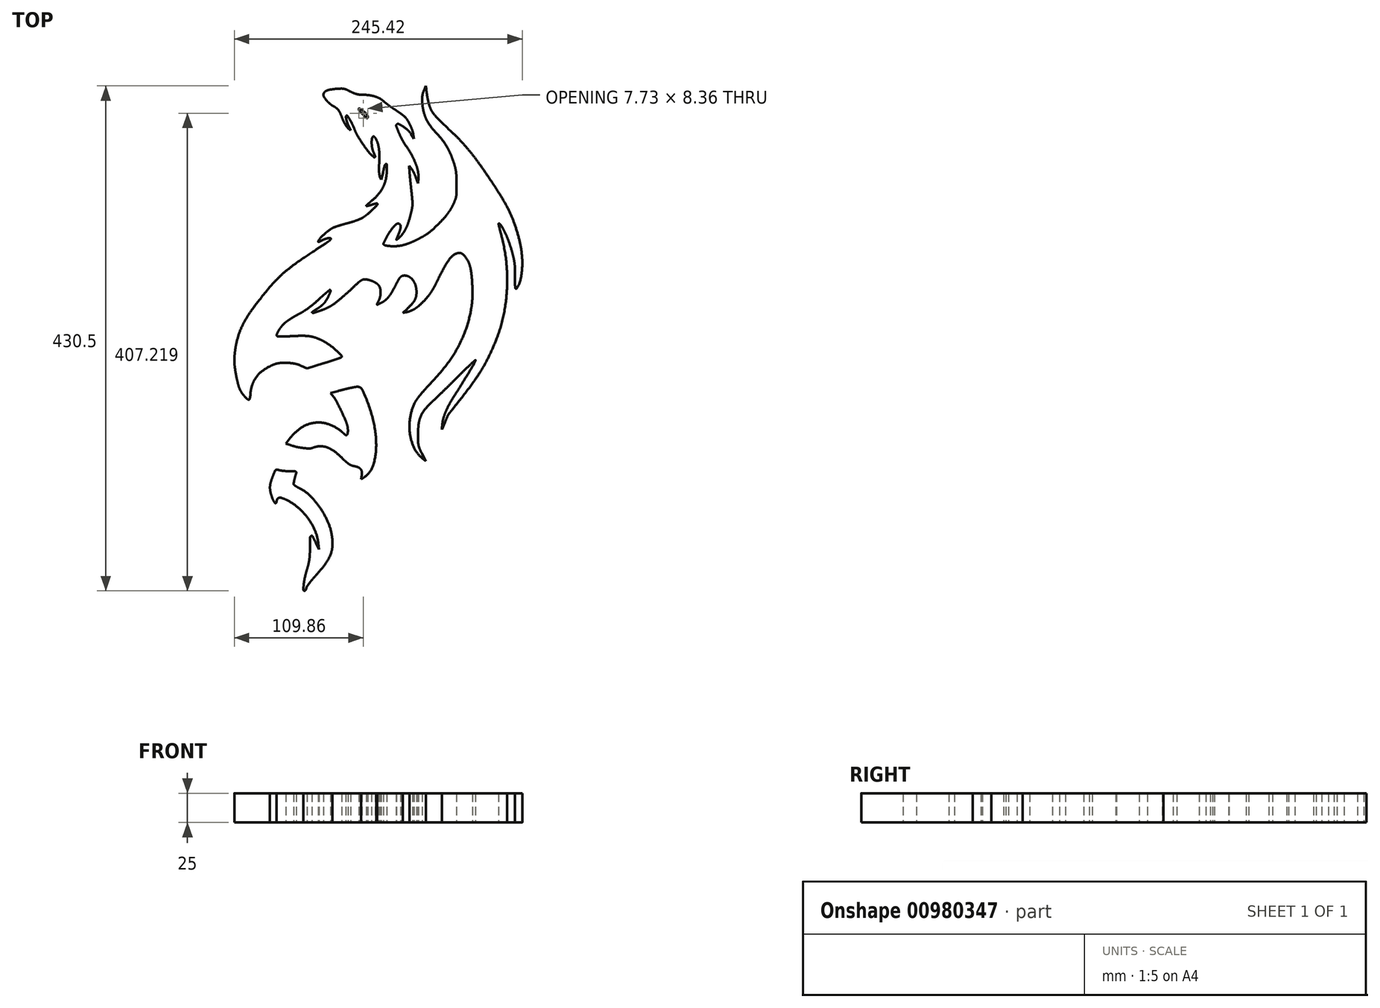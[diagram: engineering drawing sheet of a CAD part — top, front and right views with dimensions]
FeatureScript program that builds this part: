
annotation { "Feature Type Name" : "Feature", "Feature Type Description" : "" }
export const myFeature = defineFeature(function(context is Context, id is Id, definition is map)
    precondition{}
    {
        {
            var Q0;
            Q0=qCreatedBy(makeId("Top.planeOp"),FACE);
            var sketch = newSketch(context, id + "F0", { "sketchPlane" : qUnion([Q0])});
            skArc(sketch, "E0", {"start": v(-99.45, 218.84) * mm, "mid": v(-100.08, 215.3) * mm, "end": v(-100.96, 211.83) * mm});
            skArc(sketch, "E1", {"start": v(-100.96, 211.83) * mm, "mid": v(-102.01, 208.72) * mm, "end": v(-103.34, 205.71) * mm});
            skArc(sketch, "E2", {"start": v(-103.34, 205.71) * mm, "mid": v(-104.82, 203.07) * mm, "end": v(-106.56, 200.58) * mm});
            skArc(sketch, "E3", {"start": v(-106.56, 200.58) * mm, "mid": v(-108.44, 198.42) * mm, "end": v(-110.57, 196.5) * mm});
            skArc(sketch, "E4", {"start": v(-110.57, 196.5) * mm, "mid": v(-116.32, 191.62) * mm, "end": v(-121.83, 186.47) * mm});
            skArc(sketch, "E5", {"start": v(-121.83, 186.47) * mm, "mid": v(-127.23, 180.92) * mm, "end": v(-132.38, 175.14) * mm});
            skArc(sketch, "E6", {"start": v(-132.38, 175.14) * mm, "mid": v(-137.89, 168.4) * mm, "end": v(-143.13, 161.47) * mm});
            skArc(sketch, "E7", {"start": v(-143.13, 161.47) * mm, "mid": v(-149.17, 152.93) * mm, "end": v(-155.02, 144.26) * mm});
            skArc(sketch, "E8", {"start": v(-155.02, 144.26) * mm, "mid": v(-158.95, 138.2) * mm, "end": v(-162.8, 132.1) * mm});
            skArc(sketch, "E9", {"start": v(-162.8, 132.1) * mm, "mid": v(-165.38, 127.8) * mm, "end": v(-167.8, 123.4) * mm});
            skArc(sketch, "E10", {"start": v(-167.8, 123.4) * mm, "mid": v(-169.72, 119.51) * mm, "end": v(-171.47, 115.55) * mm});
            skArc(sketch, "E11", {"start": v(-171.47, 115.55) * mm, "mid": v(-173.24, 111.05) * mm, "end": v(-174.86, 106.5) * mm});
            skArc(sketch, "E12", {"start": v(-174.86, 106.5) * mm, "mid": v(-177.2, 98.78) * mm, "end": v(-179.04, 90.92) * mm});
            skArc(sketch, "E13", {"start": v(-179.04, 90.92) * mm, "mid": v(-180.15, 83.72) * mm, "end": v(-180.64, 76.45) * mm});
            skArc(sketch, "E14", {"start": v(-180.64, 76.45) * mm, "mid": v(-180.47, 70.2) * mm, "end": v(-179.66, 64) * mm});
            skArc(sketch, "E15", {"start": v(-179.66, 64) * mm, "mid": v(-178.3, 59.07) * mm, "end": v(-176.06, 54.49) * mm});
            skArc(sketch, "E16", {"start": v(-176.06, 54.49) * mm, "mid": v(-175.6, 53.86) * mm, "end": v(-175.06, 53.32) * mm});
            skArc(sketch, "E17", {"start": v(-175.06, 53.32) * mm, "mid": v(-174.72, 53.26) * mm, "end": v(-174.5, 53.53) * mm});
            skArc(sketch, "E18", {"start": v(-174.5, 53.53) * mm, "mid": v(-174.34, 54.59) * mm, "end": v(-174.29, 55.66) * mm});
            skArc(sketch, "E19", {"start": v(-174.29, 55.66) * mm, "mid": v(-174.25, 59.9) * mm, "end": v(-174.24, 64.16) * mm});
            skArc(sketch, "E20", {"start": v(-174.24, 64.16) * mm, "mid": v(-174.13, 68.8) * mm, "end": v(-173.83, 73.43) * mm});
            skArc(sketch, "E21", {"start": v(-173.83, 73.43) * mm, "mid": v(-173.35, 77.66) * mm, "end": v(-172.66, 81.86) * mm});
            skArc(sketch, "E22", {"start": v(-172.66, 81.86) * mm, "mid": v(-171.76, 85.9) * mm, "end": v(-170.64, 89.88) * mm});
            skArc(sketch, "E23", {"start": v(-170.64, 89.88) * mm, "mid": v(-169.27, 93.92) * mm, "end": v(-167.7, 97.9) * mm});
            skArc(sketch, "E24", {"start": v(-167.7, 97.9) * mm, "mid": v(-166.81, 99.86) * mm, "end": v(-165.84, 101.79) * mm});
            skArc(sketch, "E25", {"start": v(-165.84, 101.79) * mm, "mid": v(-164.65, 103.93) * mm, "end": v(-163.39, 106.04) * mm});
            skArc(sketch, "E26", {"start": v(-163.39, 106.04) * mm, "mid": v(-162.15, 108.01) * mm, "end": v(-160.9, 109.96) * mm});
            skArc(sketch, "E27", {"start": v(-160.9, 109.96) * mm, "mid": v(-160.57, 110.16) * mm, "end": v(-160.21, 110.03) * mm});
            skArc(sketch, "E28", {"start": v(-160.21, 110.03) * mm, "mid": v(-160.1, 109.86) * mm, "end": v(-160.1, 109.66) * mm});
            skArc(sketch, "E29", {"start": v(-160.1, 109.66) * mm, "mid": v(-160.37, 108.42) * mm, "end": v(-160.65, 107.19) * mm});
            skArc(sketch, "E30", {"start": v(-160.65, 107.19) * mm, "mid": v(-161, 105.74) * mm, "end": v(-161.37, 104.3) * mm});
            skArc(sketch, "E31", {"start": v(-161.37, 104.3) * mm, "mid": v(-161.83, 102.61) * mm, "end": v(-162.3, 100.94) * mm});
            skArc(sketch, "E32", {"start": v(-162.3, 100.94) * mm, "mid": v(-164.82, 90.83) * mm, "end": v(-166.55, 80.56) * mm});
            skArc(sketch, "E33", {"start": v(-166.55, 80.56) * mm, "mid": v(-167.54, 69.86) * mm, "end": v(-167.78, 59.13) * mm});
            skArc(sketch, "E34", {"start": v(-167.78, 59.13) * mm, "mid": v(-167.26, 48.52) * mm, "end": v(-166, 37.98) * mm});
            skArc(sketch, "E35", {"start": v(-166, 37.98) * mm, "mid": v(-164.03, 28.1) * mm, "end": v(-161.24, 18.42) * mm});
            skArc(sketch, "E36", {"start": v(-161.24, 18.42) * mm, "mid": v(-158.4, 10.5) * mm, "end": v(-155.21, 2.72) * mm});
            skArc(sketch, "E37", {"start": v(-155.21, 2.72) * mm, "mid": v(-151.85, -4.45) * mm, "end": v(-148.11, -11.43) * mm});
            skArc(sketch, "E38", {"start": v(-148.11, -11.43) * mm, "mid": v(-143.76, -18.65) * mm, "end": v(-139.05, -25.64) * mm});
            skArc(sketch, "E39", {"start": v(-139.05, -25.64) * mm, "mid": v(-133.15, -33.7) * mm, "end": v(-127.02, -41.57) * mm});
            skArc(sketch, "E40", {"start": v(-127.02, -41.57) * mm, "mid": v(-125.2, -43.88) * mm, "end": v(-123.4, -46.21) * mm});
            skArc(sketch, "E41", {"start": v(-123.4, -46.21) * mm, "mid": v(-121.7, -48.5) * mm, "end": v(-120.04, -50.8) * mm});
            skArc(sketch, "E42", {"start": v(-120.04, -50.8) * mm, "mid": v(-118.65, -52.78) * mm, "end": v(-117.3, -54.79) * mm});
            skArc(sketch, "E43", {"start": v(-117.3, -54.79) * mm, "mid": v(-116.62, -55.9) * mm, "end": v(-116.03, -57.07) * mm});
            skArc(sketch, "E44", {"start": v(-116.03, -57.07) * mm, "mid": v(-115.63, -57.96) * mm, "end": v(-115.23, -58.85) * mm});
            skArc(sketch, "E45", {"start": v(-115.23, -58.85) * mm, "mid": v(-114.8, -59.8) * mm, "end": v(-114.38, -60.75) * mm});
            skArc(sketch, "E46", {"start": v(-114.38, -60.75) * mm, "mid": v(-113.98, -61.62) * mm, "end": v(-113.6, -62.5) * mm});
            skArc(sketch, "E47", {"start": v(-113.6, -62.5) * mm, "mid": v(-113.31, -63.11) * mm, "end": v(-113.03, -63.74) * mm});
            skLineSegment(sketch, "E48", {"start": v(-113.03, -63.74) * mm, "end": v(-111.9, -66.24) * mm});
            skLineSegment(sketch, "E49", {"start": v(-111.9, -66.24) * mm, "end": v(-111.84, -63.6) * mm});
            skArc(sketch, "E50", {"start": v(-111.84, -63.6) * mm, "mid": v(-111.94, -61.46) * mm, "end": v(-112.34, -59.35) * mm});
            skArc(sketch, "E51", {"start": v(-112.34, -59.35) * mm, "mid": v(-113.21, -56.34) * mm, "end": v(-114.23, -53.36) * mm});
            skArc(sketch, "E52", {"start": v(-114.23, -53.36) * mm, "mid": v(-115.5, -50.13) * mm, "end": v(-116.93, -46.97) * mm});
            skArc(sketch, "E53", {"start": v(-116.93, -46.97) * mm, "mid": v(-118.42, -44.06) * mm, "end": v(-120.08, -41.24) * mm});
            skArc(sketch, "E54", {"start": v(-120.08, -41.24) * mm, "mid": v(-121.13, -39.55) * mm, "end": v(-122.19, -37.86) * mm});
            skArc(sketch, "E55", {"start": v(-122.19, -37.86) * mm, "mid": v(-123.59, -35.62) * mm, "end": v(-124.99, -33.39) * mm});
            skArc(sketch, "E56", {"start": v(-124.99, -33.39) * mm, "mid": v(-126.48, -31.01) * mm, "end": v(-127.96, -28.64) * mm});
            skArc(sketch, "E57", {"start": v(-127.96, -28.64) * mm, "mid": v(-129.31, -26.49) * mm, "end": v(-130.67, -24.34) * mm});
            skArc(sketch, "E58", {"start": v(-130.67, -24.34) * mm, "mid": v(-132.7, -21.07) * mm, "end": v(-134.7, -17.79) * mm});
            skArc(sketch, "E59", {"start": v(-134.7, -17.79) * mm, "mid": v(-136.33, -15.02) * mm, "end": v(-137.93, -12.23) * mm});
            skArc(sketch, "E60", {"start": v(-137.93, -12.23) * mm, "mid": v(-139.2, -9.95) * mm, "end": v(-140.43, -7.66) * mm});
            skArc(sketch, "E61", {"start": v(-140.43, -7.66) * mm, "mid": v(-140.69, -7) * mm, "end": v(-140.77, -6.3) * mm});
            skArc(sketch, "E62", {"start": v(-140.77, -6.3) * mm, "mid": v(-140.72, -6.23) * mm, "end": v(-140.64, -6.25) * mm});
            skArc(sketch, "E63", {"start": v(-140.64, -6.25) * mm, "mid": v(-139.25, -7.67) * mm, "end": v(-137.88, -9.1) * mm});
            skArc(sketch, "E64", {"start": v(-137.88, -9.1) * mm, "mid": v(-136.28, -10.76) * mm, "end": v(-134.7, -12.44) * mm});
            skArc(sketch, "E65", {"start": v(-134.7, -12.44) * mm, "mid": v(-132.8, -14.48) * mm, "end": v(-130.9, -16.52) * mm});
            skArc(sketch, "E66", {"start": v(-130.9, -16.52) * mm, "mid": v(-128.75, -18.83) * mm, "end": v(-126.56, -21.1) * mm});
            skArc(sketch, "E67", {"start": v(-126.56, -21.1) * mm, "mid": v(-124.1, -23.56) * mm, "end": v(-121.63, -26) * mm});
            skArc(sketch, "E68", {"start": v(-121.63, -26) * mm, "mid": v(-119.27, -28.26) * mm, "end": v(-116.89, -30.5) * mm});
            skArc(sketch, "E69", {"start": v(-116.89, -30.5) * mm, "mid": v(-115.06, -32.14) * mm, "end": v(-113.18, -33.74) * mm});
            skArc(sketch, "E70", {"start": v(-113.18, -33.74) * mm, "mid": v(-108.13, -38.06) * mm, "end": v(-103.23, -42.55) * mm});
            skArc(sketch, "E71", {"start": v(-103.23, -42.55) * mm, "mid": v(-100.1, -45.84) * mm, "end": v(-97.34, -49.44) * mm});
            skArc(sketch, "E72", {"start": v(-97.34, -49.44) * mm, "mid": v(-95.33, -52.8) * mm, "end": v(-93.78, -56.4) * mm});
            skArc(sketch, "E73", {"start": v(-93.78, -56.4) * mm, "mid": v(-92.45, -60.73) * mm, "end": v(-91.5, -65.15) * mm});
            skArc(sketch, "E74", {"start": v(-91.5, -65.15) * mm, "mid": v(-91.15, -68.11) * mm, "end": v(-91.11, -71.1) * mm});
            skArc(sketch, "E75", {"start": v(-91.11, -71.1) * mm, "mid": v(-91.37, -74.36) * mm, "end": v(-91.9, -77.6) * mm});
            skArc(sketch, "E76", {"start": v(-91.9, -77.6) * mm, "mid": v(-92.66, -80.74) * mm, "end": v(-93.68, -83.82) * mm});
            skArc(sketch, "E77", {"start": v(-93.68, -83.82) * mm, "mid": v(-94.85, -86.46) * mm, "end": v(-96.3, -88.96) * mm});
            skArc(sketch, "E78", {"start": v(-96.3, -88.96) * mm, "mid": v(-97.27, -90.48) * mm, "end": v(-98.17, -92.03) * mm});
            skArc(sketch, "E79", {"start": v(-98.17, -92.03) * mm, "mid": v(-98.14, -92.43) * mm, "end": v(-97.77, -92.59) * mm});
            skArc(sketch, "E80", {"start": v(-97.77, -92.59) * mm, "mid": v(-97, -92.33) * mm, "end": v(-96.34, -91.84) * mm});
            skArc(sketch, "E81", {"start": v(-96.34, -91.84) * mm, "mid": v(-94.67, -90.14) * mm, "end": v(-93.04, -88.4) * mm});
            skArc(sketch, "E82", {"start": v(-93.04, -88.4) * mm, "mid": v(-90.57, -85.33) * mm, "end": v(-88.55, -81.95) * mm});
            skArc(sketch, "E83", {"start": v(-88.55, -81.95) * mm, "mid": v(-86.84, -78.05) * mm, "end": v(-85.56, -74) * mm});
            skArc(sketch, "E84", {"start": v(-85.56, -74) * mm, "mid": v(-84.68, -69.61) * mm, "end": v(-84.26, -65.17) * mm});
            skArc(sketch, "E85", {"start": v(-84.26, -65.17) * mm, "mid": v(-84.3, -60.64) * mm, "end": v(-84.8, -56.14) * mm});
            skArc(sketch, "E86", {"start": v(-84.8, -56.14) * mm, "mid": v(-85.56, -52.3) * mm, "end": v(-86.64, -48.53) * mm});
            skArc(sketch, "E87", {"start": v(-86.64, -48.53) * mm, "mid": v(-87.93, -45.26) * mm, "end": v(-89.57, -42.15) * mm});
            skArc(sketch, "E88", {"start": v(-89.57, -42.15) * mm, "mid": v(-91.86, -38.67) * mm, "end": v(-94.44, -35.4) * mm});
            skArc(sketch, "E89", {"start": v(-94.44, -35.4) * mm, "mid": v(-98.54, -30.75) * mm, "end": v(-102.76, -26.21) * mm});
            skArc(sketch, "E90", {"start": v(-102.76, -26.21) * mm, "mid": v(-108.64, -19.8) * mm, "end": v(-114.24, -13.15) * mm});
            skArc(sketch, "E91", {"start": v(-114.24, -13.15) * mm, "mid": v(-118.72, -7.2) * mm, "end": v(-122.79, -0.97) * mm});
            skArc(sketch, "E92", {"start": v(-122.79, -0.97) * mm, "mid": v(-126.22, 5.19) * mm, "end": v(-129.2, 11.58) * mm});
            skArc(sketch, "E93", {"start": v(-129.2, 11.58) * mm, "mid": v(-131.93, 18.58) * mm, "end": v(-134.24, 25.73) * mm});
            skArc(sketch, "E94", {"start": v(-134.24, 25.73) * mm, "mid": v(-136.2, 33.78) * mm, "end": v(-137.48, 41.96) * mm});
            skArc(sketch, "E95", {"start": v(-137.48, 41.96) * mm, "mid": v(-138.1, 50.37) * mm, "end": v(-138.03, 58.8) * mm});
            skArc(sketch, "E96", {"start": v(-138.03, 58.8) * mm, "mid": v(-137.38, 66.14) * mm, "end": v(-136.1, 73.39) * mm});
            skArc(sketch, "E97", {"start": v(-136.1, 73.39) * mm, "mid": v(-134.41, 78) * mm, "end": v(-131.57, 81.98) * mm});
            skArc(sketch, "E98", {"start": v(-131.57, 81.98) * mm, "mid": v(-130.3, 83.09) * mm, "end": v(-128.84, 83.92) * mm});
            skArc(sketch, "E99", {"start": v(-128.84, 83.92) * mm, "mid": v(-127.47, 84.27) * mm, "end": v(-126.06, 84.16) * mm});
            skArc(sketch, "E100", {"start": v(-126.06, 84.16) * mm, "mid": v(-124.42, 83.55) * mm, "end": v(-122.95, 82.58) * mm});
            skArc(sketch, "E101", {"start": v(-122.95, 82.58) * mm, "mid": v(-120.97, 80.81) * mm, "end": v(-119.12, 78.9) * mm});
            skArc(sketch, "E102", {"start": v(-119.12, 78.9) * mm, "mid": v(-117.45, 77) * mm, "end": v(-115.85, 75.04) * mm});
            skArc(sketch, "E103", {"start": v(-115.85, 75.04) * mm, "mid": v(-114.67, 73.45) * mm, "end": v(-113.6, 71.78) * mm});
            skArc(sketch, "E104", {"start": v(-113.6, 71.78) * mm, "mid": v(-112.41, 69.67) * mm, "end": v(-111.32, 67.5) * mm});
            skArc(sketch, "E105", {"start": v(-111.32, 67.5) * mm, "mid": v(-109.38, 63.4) * mm, "end": v(-107.47, 59.26) * mm});
            skArc(sketch, "E106", {"start": v(-107.47, 59.26) * mm, "mid": v(-105.9, 56) * mm, "end": v(-104.2, 52.79) * mm});
            skArc(sketch, "E107", {"start": v(-104.2, 52.79) * mm, "mid": v(-102.63, 50.16) * mm, "end": v(-100.89, 47.64) * mm});
            skArc(sketch, "E108", {"start": v(-100.89, 47.64) * mm, "mid": v(-99.12, 45.42) * mm, "end": v(-97.2, 43.32) * mm});
            skArc(sketch, "E109", {"start": v(-97.2, 43.32) * mm, "mid": v(-95.03, 41.26) * mm, "end": v(-92.75, 39.34) * mm});
            skArc(sketch, "E110", {"start": v(-92.75, 39.34) * mm, "mid": v(-90.94, 38) * mm, "end": v(-89.03, 36.79) * mm});
            skArc(sketch, "E111", {"start": v(-89.03, 36.79) * mm, "mid": v(-87.04, 35.7) * mm, "end": v(-84.98, 34.74) * mm});
            skArc(sketch, "E112", {"start": v(-84.98, 34.74) * mm, "mid": v(-83.2, 34.04) * mm, "end": v(-81.4, 33.45) * mm});
            skArc(sketch, "E113", {"start": v(-81.4, 33.45) * mm, "mid": v(-80.57, 33.44) * mm, "end": v(-79.85, 33.85) * mm});
            skArc(sketch, "E114", {"start": v(-79.85, 33.85) * mm, "mid": v(-79.77, 34.03) * mm, "end": v(-79.82, 34.21) * mm});
            skArc(sketch, "E115", {"start": v(-79.82, 34.21) * mm, "mid": v(-80.18, 34.7) * mm, "end": v(-80.55, 35.16) * mm});
            skArc(sketch, "E116", {"start": v(-80.55, 35.16) * mm, "mid": v(-81.07, 35.75) * mm, "end": v(-81.62, 36.31) * mm});
            skArc(sketch, "E117", {"start": v(-81.62, 36.31) * mm, "mid": v(-82.3, 36.95) * mm, "end": v(-82.99, 37.57) * mm});
            skArc(sketch, "E118", {"start": v(-82.99, 37.57) * mm, "mid": v(-85.28, 39.78) * mm, "end": v(-87.34, 42.21) * mm});
            skArc(sketch, "E119", {"start": v(-87.34, 42.21) * mm, "mid": v(-88.82, 44.51) * mm, "end": v(-89.92, 47.02) * mm});
            skArc(sketch, "E120", {"start": v(-89.92, 47.02) * mm, "mid": v(-90.52, 49.45) * mm, "end": v(-90.69, 51.95) * mm});
            skArc(sketch, "E121", {"start": v(-90.69, 51.95) * mm, "mid": v(-90.4, 54.49) * mm, "end": v(-89.7, 56.95) * mm});
            skArc(sketch, "E122", {"start": v(-89.7, 56.95) * mm, "mid": v(-89, 58.56) * mm, "end": v(-88.12, 60.1) * mm});
            skArc(sketch, "E123", {"start": v(-88.12, 60.1) * mm, "mid": v(-87.2, 61.32) * mm, "end": v(-86.08, 62.4) * mm});
            skArc(sketch, "E124", {"start": v(-86.08, 62.4) * mm, "mid": v(-84.91, 63.2) * mm, "end": v(-83.63, 63.78) * mm});
            skArc(sketch, "E125", {"start": v(-83.63, 63.78) * mm, "mid": v(-82.24, 64.14) * mm, "end": v(-80.82, 64.26) * mm});
            skArc(sketch, "E126", {"start": v(-80.82, 64.26) * mm, "mid": v(-79.16, 64.15) * mm, "end": v(-77.53, 63.8) * mm});
            skArc(sketch, "E127", {"start": v(-77.53, 63.8) * mm, "mid": v(-76.14, 63.25) * mm, "end": v(-74.88, 62.45) * mm});
            skArc(sketch, "E128", {"start": v(-74.88, 62.45) * mm, "mid": v(-73.56, 61.25) * mm, "end": v(-72.42, 59.87) * mm});
            skArc(sketch, "E129", {"start": v(-72.42, 59.87) * mm, "mid": v(-70.97, 57.72) * mm, "end": v(-69.63, 55.5) * mm});
            skArc(sketch, "E130", {"start": v(-69.63, 55.5) * mm, "mid": v(-68.1, 52.98) * mm, "end": v(-66.43, 50.54) * mm});
            skArc(sketch, "E131", {"start": v(-66.43, 50.54) * mm, "mid": v(-64.59, 48.13) * mm, "end": v(-62.63, 45.8) * mm});
            skArc(sketch, "E132", {"start": v(-62.63, 45.8) * mm, "mid": v(-60.76, 43.81) * mm, "end": v(-58.8, 41.91) * mm});
            skArc(sketch, "E133", {"start": v(-58.8, 41.91) * mm, "mid": v(-57.26, 40.68) * mm, "end": v(-55.58, 39.66) * mm});
            skArc(sketch, "E134", {"start": v(-55.58, 39.66) * mm, "mid": v(-54.58, 39.18) * mm, "end": v(-53.57, 38.76) * mm});
            skArc(sketch, "E135", {"start": v(-53.57, 38.76) * mm, "mid": v(-53.2, 38.78) * mm, "end": v(-52.97, 39.06) * mm});
            skArc(sketch, "E136", {"start": v(-52.97, 39.06) * mm, "mid": v(-52.9, 39.62) * mm, "end": v(-53, 40.17) * mm});
            skArc(sketch, "E137", {"start": v(-53, 40.17) * mm, "mid": v(-53.65, 42.17) * mm, "end": v(-54.34, 44.16) * mm});
            skArc(sketch, "E138", {"start": v(-54.34, 44.16) * mm, "mid": v(-54.65, 45.16) * mm, "end": v(-54.91, 46.16) * mm});
            skArc(sketch, "E139", {"start": v(-54.91, 46.16) * mm, "mid": v(-55.12, 47.18) * mm, "end": v(-55.27, 48.2) * mm});
            skArc(sketch, "E140", {"start": v(-55.27, 48.2) * mm, "mid": v(-55.35, 49.15) * mm, "end": v(-55.38, 50.1) * mm});
            skArc(sketch, "E141", {"start": v(-55.38, 50.1) * mm, "mid": v(-55.34, 50.89) * mm, "end": v(-55.21, 51.66) * mm});
            skArc(sketch, "E142", {"start": v(-55.21, 51.66) * mm, "mid": v(-54.32, 54.66) * mm, "end": v(-52.96, 57.47) * mm});
            skArc(sketch, "E143", {"start": v(-52.96, 57.47) * mm, "mid": v(-51.3, 59.62) * mm, "end": v(-49.18, 61.3) * mm});
            skArc(sketch, "E144", {"start": v(-49.18, 61.3) * mm, "mid": v(-46.7, 62.44) * mm, "end": v(-44, 62.94) * mm});
            skArc(sketch, "E145", {"start": v(-44, 62.94) * mm, "mid": v(-40.84, 62.89) * mm, "end": v(-37.72, 62.34) * mm});
            skLineSegment(sketch, "E146", {"start": v(-37.72, 62.34) * mm, "end": v(-32.77, 61.08) * mm});
            skLineSegment(sketch, "E147", {"start": v(-32.77, 61.08) * mm, "end": v(-25.7, 67.63) * mm});
            skArc(sketch, "E148", {"start": v(-25.7, 67.63) * mm, "mid": v(-24.05, 69.11) * mm, "end": v(-22.36, 70.56) * mm});
            skArc(sketch, "E149", {"start": v(-22.36, 70.56) * mm, "mid": v(-20.27, 72.27) * mm, "end": v(-18.15, 73.95) * mm});
            skArc(sketch, "E150", {"start": v(-18.15, 73.95) * mm, "mid": v(-15.98, 75.63) * mm, "end": v(-13.78, 77.27) * mm});
            skArc(sketch, "E151", {"start": v(-13.78, 77.27) * mm, "mid": v(-11.88, 78.64) * mm, "end": v(-9.95, 79.96) * mm});
            skArc(sketch, "E152", {"start": v(-9.95, 79.96) * mm, "mid": v(-8.27, 81.08) * mm, "end": v(-6.59, 82.2) * mm});
            skArc(sketch, "E153", {"start": v(-6.59, 82.2) * mm, "mid": v(-5.13, 83.17) * mm, "end": v(-3.67, 84.15) * mm});
            skArc(sketch, "E154", {"start": v(-3.67, 84.15) * mm, "mid": v(-2.42, 84.99) * mm, "end": v(-1.16, 85.83) * mm});
            skArc(sketch, "E155", {"start": v(-1.16, 85.83) * mm, "mid": v(-0.96, 85.96) * mm, "end": v(-0.77, 86.1) * mm});
            skArc(sketch, "E156", {"start": v(-0.77, 86.1) * mm, "mid": v(-0.7, 86.24) * mm, "end": v(-0.74, 86.4) * mm});
            skArc(sketch, "E157", {"start": v(-0.74, 86.4) * mm, "mid": v(-1.36, 87.1) * mm, "end": v(-2, 87.8) * mm});
            skArc(sketch, "E158", {"start": v(-2, 87.8) * mm, "mid": v(-2.8, 88.65) * mm, "end": v(-3.61, 89.47) * mm});
            skArc(sketch, "E159", {"start": v(-3.61, 89.47) * mm, "mid": v(-4.62, 90.44) * mm, "end": v(-5.63, 91.4) * mm});
            skArc(sketch, "E160", {"start": v(-5.63, 91.4) * mm, "mid": v(-7.1, 92.67) * mm, "end": v(-8.62, 93.85) * mm});
            skArc(sketch, "E161", {"start": v(-8.62, 93.85) * mm, "mid": v(-10.45, 95.14) * mm, "end": v(-12.33, 96.35) * mm});
            skArc(sketch, "E162", {"start": v(-12.33, 96.35) * mm, "mid": v(-14.48, 97.64) * mm, "end": v(-16.68, 98.86) * mm});
            skArc(sketch, "E163", {"start": v(-16.68, 98.86) * mm, "mid": v(-19.14, 100.14) * mm, "end": v(-21.63, 101.35) * mm});
            skArc(sketch, "E164", {"start": v(-21.63, 101.35) * mm, "mid": v(-28.13, 104.44) * mm, "end": v(-34.6, 107.57) * mm});
            skArc(sketch, "E165", {"start": v(-34.6, 107.57) * mm, "mid": v(-37.72, 109.18) * mm, "end": v(-40.78, 110.91) * mm});
            skArc(sketch, "E166", {"start": v(-40.78, 110.91) * mm, "mid": v(-43.03, 112.37) * mm, "end": v(-45.16, 113.99) * mm});
            skArc(sketch, "E167", {"start": v(-45.16, 113.99) * mm, "mid": v(-47.63, 116.1) * mm, "end": v(-50.01, 118.3) * mm});
            skArc(sketch, "E168", {"start": v(-50.01, 118.3) * mm, "mid": v(-52.33, 120.59) * mm, "end": v(-54.6, 122.92) * mm});
            skArc(sketch, "E169", {"start": v(-54.6, 122.92) * mm, "mid": v(-55.63, 124.15) * mm, "end": v(-56.47, 125.52) * mm});
            skArc(sketch, "E170", {"start": v(-56.47, 125.52) * mm, "mid": v(-56.48, 126.07) * mm, "end": v(-56.05, 126.4) * mm});
            skArc(sketch, "E171", {"start": v(-56.05, 126.4) * mm, "mid": v(-55.12, 126.45) * mm, "end": v(-54.2, 126.24) * mm});
            skArc(sketch, "E172", {"start": v(-54.2, 126.24) * mm, "mid": v(-53.64, 126.04) * mm, "end": v(-53.07, 125.87) * mm});
            skArc(sketch, "E173", {"start": v(-53.07, 125.87) * mm, "mid": v(-52.41, 125.7) * mm, "end": v(-51.76, 125.56) * mm});
            skArc(sketch, "E174", {"start": v(-51.76, 125.56) * mm, "mid": v(-51.12, 125.45) * mm, "end": v(-50.48, 125.36) * mm});
            skArc(sketch, "E175", {"start": v(-50.48, 125.36) * mm, "mid": v(-49.97, 125.32) * mm, "end": v(-49.46, 125.31) * mm});
            skArc(sketch, "E176", {"start": v(-49.46, 125.31) * mm, "mid": v(-48.76, 125.34) * mm, "end": v(-48.07, 125.38) * mm});
            skArc(sketch, "E177", {"start": v(-48.07, 125.38) * mm, "mid": v(-47.94, 125.44) * mm, "end": v(-47.9, 125.59) * mm});
            skArc(sketch, "E178", {"start": v(-47.9, 125.59) * mm, "mid": v(-47.98, 125.77) * mm, "end": v(-48.12, 125.9) * mm});
            skArc(sketch, "E179", {"start": v(-48.12, 125.9) * mm, "mid": v(-48.94, 126.48) * mm, "end": v(-49.77, 127.04) * mm});
            skArc(sketch, "E180", {"start": v(-49.77, 127.04) * mm, "mid": v(-53.46, 129.9) * mm, "end": v(-56.7, 133.26) * mm});
            skArc(sketch, "E181", {"start": v(-56.7, 133.26) * mm, "mid": v(-59.6, 137.2) * mm, "end": v(-62, 141.48) * mm});
            skArc(sketch, "E182", {"start": v(-62, 141.48) * mm, "mid": v(-63.76, 145.8) * mm, "end": v(-64.94, 150.31) * mm});
            skArc(sketch, "E183", {"start": v(-64.94, 150.31) * mm, "mid": v(-65.3, 154.31) * mm, "end": v(-64.87, 158.31) * mm});
            skLineSegment(sketch, "E184", {"start": v(-64.87, 158.31) * mm, "end": v(-64.14, 161.76) * mm});
            skLineSegment(sketch, "E185", {"start": v(-64.14, 161.76) * mm, "end": v(-63, 156.76) * mm});
            skArc(sketch, "E186", {"start": v(-63, 156.76) * mm, "mid": v(-62.76, 155.68) * mm, "end": v(-62.52, 154.6) * mm});
            skArc(sketch, "E187", {"start": v(-62.52, 154.6) * mm, "mid": v(-62.25, 153.4) * mm, "end": v(-62, 152.2) * mm});
            skArc(sketch, "E188", {"start": v(-62, 152.2) * mm, "mid": v(-61.75, 151.08) * mm, "end": v(-61.5, 149.95) * mm});
            skArc(sketch, "E189", {"start": v(-61.5, 149.95) * mm, "mid": v(-61.33, 149.1) * mm, "end": v(-61.15, 148.26) * mm});
            skArc(sketch, "E190", {"start": v(-61.15, 148.26) * mm, "mid": v(-60.91, 147.1) * mm, "end": v(-60.66, 145.95) * mm});
            skArc(sketch, "E191", {"start": v(-60.66, 145.95) * mm, "mid": v(-60.58, 145.76) * mm, "end": v(-60.43, 145.6) * mm});
            skArc(sketch, "E192", {"start": v(-60.43, 145.6) * mm, "mid": v(-60.3, 145.59) * mm, "end": v(-60.2, 145.69) * mm});
            skArc(sketch, "E193", {"start": v(-60.2, 145.69) * mm, "mid": v(-59.94, 146.47) * mm, "end": v(-59.7, 147.26) * mm});
            skArc(sketch, "E194", {"start": v(-59.7, 147.26) * mm, "mid": v(-59.52, 148.05) * mm, "end": v(-59.41, 148.85) * mm});
            skArc(sketch, "E195", {"start": v(-59.41, 148.85) * mm, "mid": v(-59.27, 150.7) * mm, "end": v(-59.15, 152.55) * mm});
            skArc(sketch, "E196", {"start": v(-59.15, 152.55) * mm, "mid": v(-59.03, 154.77) * mm, "end": v(-58.94, 156.98) * mm});
            skArc(sketch, "E197", {"start": v(-58.94, 156.98) * mm, "mid": v(-58.87, 159.37) * mm, "end": v(-58.83, 161.76) * mm});
            skArc(sketch, "E198", {"start": v(-58.83, 161.76) * mm, "mid": v(-58.7, 165.95) * mm, "end": v(-58.42, 170.14) * mm});
            skArc(sketch, "E199", {"start": v(-58.42, 170.14) * mm, "mid": v(-58.02, 173.63) * mm, "end": v(-57.4, 177.1) * mm});
            skArc(sketch, "E200", {"start": v(-57.4, 177.1) * mm, "mid": v(-56.76, 179.7) * mm, "end": v(-55.95, 182.24) * mm});
            skArc(sketch, "E201", {"start": v(-55.95, 182.24) * mm, "mid": v(-55.25, 183.33) * mm, "end": v(-54.14, 183.99) * mm});
            skArc(sketch, "E202", {"start": v(-54.14, 183.99) * mm, "mid": v(-53.53, 183.94) * mm, "end": v(-53.12, 183.48) * mm});
            skArc(sketch, "E203", {"start": v(-53.12, 183.48) * mm, "mid": v(-52.68, 182.08) * mm, "end": v(-52.35, 180.64) * mm});
            skArc(sketch, "E204", {"start": v(-52.35, 180.64) * mm, "mid": v(-52.11, 178.88) * mm, "end": v(-52.02, 177.1) * mm});
            skArc(sketch, "E205", {"start": v(-52.02, 177.1) * mm, "mid": v(-52.09, 175.5) * mm, "end": v(-52.33, 173.93) * mm});
            skArc(sketch, "E206", {"start": v(-52.33, 173.93) * mm, "mid": v(-52.5, 173.22) * mm, "end": v(-52.7, 172.52) * mm});
            skArc(sketch, "E207", {"start": v(-52.7, 172.52) * mm, "mid": v(-52.95, 171.7) * mm, "end": v(-53.23, 170.88) * mm});
            skArc(sketch, "E208", {"start": v(-53.23, 170.88) * mm, "mid": v(-53.52, 170.09) * mm, "end": v(-53.83, 169.3) * mm});
            skArc(sketch, "E209", {"start": v(-53.83, 169.3) * mm, "mid": v(-54.11, 168.65) * mm, "end": v(-54.42, 168.01) * mm});
            skArc(sketch, "E210", {"start": v(-54.42, 168.01) * mm, "mid": v(-54.67, 167.5) * mm, "end": v(-54.9, 166.96) * mm});
            skArc(sketch, "E211", {"start": v(-54.9, 166.96) * mm, "mid": v(-55.05, 166.52) * mm, "end": v(-55.17, 166.07) * mm});
            skArc(sketch, "E212", {"start": v(-55.17, 166.07) * mm, "mid": v(-55.21, 165.77) * mm, "end": v(-55.21, 165.46) * mm});
            skArc(sketch, "E213", {"start": v(-55.21, 165.46) * mm, "mid": v(-55.14, 165.32) * mm, "end": v(-55, 165.26) * mm});
            skArc(sketch, "E214", {"start": v(-55, 165.26) * mm, "mid": v(-53.4, 165.64) * mm, "end": v(-52.15, 166.7) * mm});
            skArc(sketch, "E215", {"start": v(-52.15, 166.7) * mm, "mid": v(-48.82, 171.3) * mm, "end": v(-45.58, 175.98) * mm});
            skArc(sketch, "E216", {"start": v(-45.58, 175.98) * mm, "mid": v(-42.49, 180.73) * mm, "end": v(-39.56, 185.58) * mm});
            skArc(sketch, "E217", {"start": v(-39.56, 185.58) * mm, "mid": v(-37.89, 188.91) * mm, "end": v(-36.6, 192.42) * mm});
            skArc(sketch, "E218", {"start": v(-36.6, 192.42) * mm, "mid": v(-36.32, 193.27) * mm, "end": v(-35.97, 194.1) * mm});
            skArc(sketch, "E219", {"start": v(-35.97, 194.1) * mm, "mid": v(-35.48, 195.09) * mm, "end": v(-34.96, 196.05) * mm});
            skArc(sketch, "E220", {"start": v(-34.96, 196.05) * mm, "mid": v(-34.38, 197) * mm, "end": v(-33.77, 197.94) * mm});
            skArc(sketch, "E221", {"start": v(-33.77, 197.94) * mm, "mid": v(-33.2, 198.73) * mm, "end": v(-32.57, 199.48) * mm});
            skLineSegment(sketch, "E222", {"start": v(-32.57, 199.48) * mm, "end": v(-29.67, 202.76) * mm});
            skLineSegment(sketch, "E223", {"start": v(-29.67, 202.76) * mm, "end": v(-30.3, 197.9) * mm});
            skArc(sketch, "E224", {"start": v(-30.3, 197.9) * mm, "mid": v(-30.5, 196.05) * mm, "end": v(-30.6, 194.18) * mm});
            skArc(sketch, "E225", {"start": v(-30.6, 194.18) * mm, "mid": v(-30.39, 193.78) * mm, "end": v(-29.93, 193.8) * mm});
            skArc(sketch, "E226", {"start": v(-29.93, 193.8) * mm, "mid": v(-29.25, 194.42) * mm, "end": v(-28.77, 195.21) * mm});
            skArc(sketch, "E227", {"start": v(-28.77, 195.21) * mm, "mid": v(-27.75, 197.74) * mm, "end": v(-26.77, 200.27) * mm});
            skArc(sketch, "E228", {"start": v(-26.77, 200.27) * mm, "mid": v(-25.97, 202.25) * mm, "end": v(-25.06, 204.17) * mm});
            skArc(sketch, "E229", {"start": v(-25.06, 204.17) * mm, "mid": v(-24.24, 205.57) * mm, "end": v(-23.25, 206.86) * mm});
            skArc(sketch, "E230", {"start": v(-23.25, 206.86) * mm, "mid": v(-22.1, 208.02) * mm, "end": v(-20.82, 209.03) * mm});
            skArc(sketch, "E231", {"start": v(-20.82, 209.03) * mm, "mid": v(-19, 210.23) * mm, "end": v(-17.12, 211.33) * mm});
            skArc(sketch, "E232", {"start": v(-17.12, 211.33) * mm, "mid": v(-16.48, 211.72) * mm, "end": v(-15.89, 212.19) * mm});
            skArc(sketch, "E233", {"start": v(-15.89, 212.19) * mm, "mid": v(-15.2, 212.83) * mm, "end": v(-14.53, 213.51) * mm});
            skArc(sketch, "E234", {"start": v(-14.53, 213.51) * mm, "mid": v(-13.88, 214.26) * mm, "end": v(-13.27, 215.05) * mm});
            skArc(sketch, "E235", {"start": v(-13.27, 215.05) * mm, "mid": v(-12.76, 215.79) * mm, "end": v(-12.3, 216.57) * mm});
            skArc(sketch, "E236", {"start": v(-12.3, 216.57) * mm, "mid": v(-11.73, 217.66) * mm, "end": v(-11.19, 218.77) * mm});
            skArc(sketch, "E237", {"start": v(-11.19, 218.77) * mm, "mid": v(-10.99, 219.33) * mm, "end": v(-10.89, 219.92) * mm});
            skArc(sketch, "E238", {"start": v(-10.89, 219.92) * mm, "mid": v(-10.93, 220.38) * mm, "end": v(-11.1, 220.8) * mm});
            skArc(sketch, "E239", {"start": v(-11.1, 220.8) * mm, "mid": v(-11.48, 221.34) * mm, "end": v(-11.92, 221.83) * mm});
            skArc(sketch, "E240", {"start": v(-11.92, 221.83) * mm, "mid": v(-12.42, 222.24) * mm, "end": v(-13, 222.54) * mm});
            skArc(sketch, "E241", {"start": v(-13, 222.54) * mm, "mid": v(-14.07, 222.91) * mm, "end": v(-15.15, 223.24) * mm});
            skArc(sketch, "E242", {"start": v(-15.15, 223.24) * mm, "mid": v(-16.5, 223.58) * mm, "end": v(-17.88, 223.87) * mm});
            skArc(sketch, "E243", {"start": v(-17.88, 223.87) * mm, "mid": v(-19.44, 224.14) * mm, "end": v(-21.01, 224.36) * mm});
            skArc(sketch, "E244", {"start": v(-21.01, 224.36) * mm, "mid": v(-23.38, 224.62) * mm, "end": v(-25.75, 224.84) * mm});
            skArc(sketch, "E245", {"start": v(-25.75, 224.84) * mm, "mid": v(-27.02, 224.87) * mm, "end": v(-28.28, 224.75) * mm});
            skArc(sketch, "E246", {"start": v(-28.28, 224.75) * mm, "mid": v(-29.46, 224.48) * mm, "end": v(-30.59, 224.06) * mm});
            skArc(sketch, "E247", {"start": v(-30.59, 224.06) * mm, "mid": v(-32.43, 223.2) * mm, "end": v(-34.25, 222.27) * mm});
            skArc(sketch, "E248", {"start": v(-34.25, 222.27) * mm, "mid": v(-35.88, 221.46) * mm, "end": v(-37.55, 220.7) * mm});
            skArc(sketch, "E249", {"start": v(-37.55, 220.7) * mm, "mid": v(-38.86, 220.2) * mm, "end": v(-40.21, 219.82) * mm});
            skArc(sketch, "E250", {"start": v(-40.21, 219.82) * mm, "mid": v(-41.63, 219.55) * mm, "end": v(-43.06, 219.4) * mm});
            skArc(sketch, "E251", {"start": v(-43.06, 219.4) * mm, "mid": v(-45.02, 219.3) * mm, "end": v(-46.97, 219.26) * mm});
            skArc(sketch, "E252", {"start": v(-46.97, 219.26) * mm, "mid": v(-49.6, 219.18) * mm, "end": v(-52.22, 218.92) * mm});
            skArc(sketch, "E253", {"start": v(-52.22, 218.92) * mm, "mid": v(-54.44, 218.52) * mm, "end": v(-56.62, 217.89) * mm});
            skArc(sketch, "E254", {"start": v(-56.62, 217.89) * mm, "mid": v(-58.35, 217.17) * mm, "end": v(-59.99, 216.24) * mm});
            skArc(sketch, "E255", {"start": v(-59.99, 216.24) * mm, "mid": v(-61.17, 215.26) * mm, "end": v(-62.11, 214.04) * mm});
            skArc(sketch, "E256", {"start": v(-62.11, 214.04) * mm, "mid": v(-62.48, 213.54) * mm, "end": v(-62.92, 213.1) * mm});
            skArc(sketch, "E257", {"start": v(-62.92, 213.1) * mm, "mid": v(-63.8, 212.36) * mm, "end": v(-64.7, 211.65) * mm});
            skArc(sketch, "E258", {"start": v(-64.7, 211.65) * mm, "mid": v(-65.78, 210.84) * mm, "end": v(-66.9, 210.06) * mm});
            skArc(sketch, "E259", {"start": v(-66.9, 210.06) * mm, "mid": v(-68.07, 209.3) * mm, "end": v(-69.27, 208.55) * mm});
            skArc(sketch, "E260", {"start": v(-69.27, 208.55) * mm, "mid": v(-70.58, 207.75) * mm, "end": v(-71.85, 206.92) * mm});
            skArc(sketch, "E261", {"start": v(-71.85, 206.92) * mm, "mid": v(-73.26, 205.95) * mm, "end": v(-74.65, 204.96) * mm});
            skArc(sketch, "E262", {"start": v(-74.65, 204.96) * mm, "mid": v(-75.95, 204) * mm, "end": v(-77.24, 203) * mm});
            skArc(sketch, "E263", {"start": v(-77.24, 203) * mm, "mid": v(-78.2, 202.2) * mm, "end": v(-79.14, 201.36) * mm});
            skArc(sketch, "E264", {"start": v(-79.14, 201.36) * mm, "mid": v(-80.82, 199.63) * mm, "end": v(-82.32, 197.74) * mm});
            skArc(sketch, "E265", {"start": v(-82.32, 197.74) * mm, "mid": v(-83.8, 195.49) * mm, "end": v(-85.13, 193.13) * mm});
            skArc(sketch, "E266", {"start": v(-85.13, 193.13) * mm, "mid": v(-86.2, 190.83) * mm, "end": v(-87.12, 188.46) * mm});
            skArc(sketch, "E267", {"start": v(-87.12, 188.46) * mm, "mid": v(-87.56, 186.64) * mm, "end": v(-87.69, 184.76) * mm});
            skArc(sketch, "E268", {"start": v(-87.69, 184.76) * mm, "mid": v(-87.66, 184.23) * mm, "end": v(-87.63, 183.7) * mm});
            skArc(sketch, "E269", {"start": v(-87.63, 183.7) * mm, "mid": v(-87.57, 183.38) * mm, "end": v(-87.48, 183.08) * mm});
            skArc(sketch, "E270", {"start": v(-87.48, 183.08) * mm, "mid": v(-87.4, 183) * mm, "end": v(-87.28, 183.02) * mm});
            skArc(sketch, "E271", {"start": v(-87.28, 183.02) * mm, "mid": v(-87.15, 183.12) * mm, "end": v(-87.07, 183.26) * mm});
            skArc(sketch, "E272", {"start": v(-87.07, 183.26) * mm, "mid": v(-86.23, 184.99) * mm, "end": v(-85.05, 186.5) * mm});
            skArc(sketch, "E273", {"start": v(-85.05, 186.5) * mm, "mid": v(-82.89, 188.6) * mm, "end": v(-80.6, 190.58) * mm});
            skArc(sketch, "E274", {"start": v(-80.6, 190.58) * mm, "mid": v(-78.3, 192.38) * mm, "end": v(-75.92, 194.06) * mm});
            skArc(sketch, "E275", {"start": v(-75.92, 194.06) * mm, "mid": v(-74.96, 194.3) * mm, "end": v(-74.06, 193.88) * mm});
            skArc(sketch, "E276", {"start": v(-74.06, 193.88) * mm, "mid": v(-73.6, 193.09) * mm, "end": v(-73.58, 192.17) * mm});
            skArc(sketch, "E277", {"start": v(-73.58, 192.17) * mm, "mid": v(-74.1, 190.26) * mm, "end": v(-74.75, 188.38) * mm});
            skArc(sketch, "E278", {"start": v(-74.75, 188.38) * mm, "mid": v(-75.76, 186) * mm, "end": v(-76.91, 183.7) * mm});
            skArc(sketch, "E279", {"start": v(-76.91, 183.7) * mm, "mid": v(-78.38, 181.12) * mm, "end": v(-79.96, 178.6) * mm});
            skArc(sketch, "E280", {"start": v(-79.96, 178.6) * mm, "mid": v(-83.2, 173.43) * mm, "end": v(-86.22, 168.14) * mm});
            skArc(sketch, "E281", {"start": v(-86.22, 168.14) * mm, "mid": v(-88.48, 163.65) * mm, "end": v(-90.42, 159.01) * mm});
            skArc(sketch, "E282", {"start": v(-90.42, 159.01) * mm, "mid": v(-91.64, 155.3) * mm, "end": v(-92.55, 151.48) * mm});
            skArc(sketch, "E283", {"start": v(-92.55, 151.48) * mm, "mid": v(-92.72, 148.78) * mm, "end": v(-92.23, 146.12) * mm});
            skArc(sketch, "E284", {"start": v(-92.23, 146.12) * mm, "mid": v(-92.03, 145.58) * mm, "end": v(-91.78, 145.06) * mm});
            skArc(sketch, "E285", {"start": v(-91.78, 145.06) * mm, "mid": v(-91.6, 144.94) * mm, "end": v(-91.4, 145.03) * mm});
            skArc(sketch, "E286", {"start": v(-91.4, 145.03) * mm, "mid": v(-91.16, 145.4) * mm, "end": v(-91, 145.82) * mm});
            skArc(sketch, "E287", {"start": v(-91, 145.82) * mm, "mid": v(-90.62, 147.22) * mm, "end": v(-90.26, 148.62) * mm});
            skArc(sketch, "E288", {"start": v(-90.26, 148.62) * mm, "mid": v(-89.96, 149.66) * mm, "end": v(-89.6, 150.67) * mm});
            skArc(sketch, "E289", {"start": v(-89.6, 150.67) * mm, "mid": v(-89.14, 151.75) * mm, "end": v(-88.62, 152.8) * mm});
            skArc(sketch, "E290", {"start": v(-88.62, 152.8) * mm, "mid": v(-88.09, 153.79) * mm, "end": v(-87.5, 154.74) * mm});
            skArc(sketch, "E291", {"start": v(-87.5, 154.74) * mm, "mid": v(-86.99, 155.44) * mm, "end": v(-86.4, 156.09) * mm});
            skArc(sketch, "E292", {"start": v(-86.4, 156.09) * mm, "mid": v(-85.56, 156.84) * mm, "end": v(-84.64, 157.49) * mm});
            skArc(sketch, "E293", {"start": v(-84.64, 157.49) * mm, "mid": v(-84.2, 157.51) * mm, "end": v(-83.94, 157.15) * mm});
            skArc(sketch, "E294", {"start": v(-83.94, 157.15) * mm, "mid": v(-83.88, 156.05) * mm, "end": v(-83.96, 154.95) * mm});
            skArc(sketch, "E295", {"start": v(-83.96, 154.95) * mm, "mid": v(-84.6, 150.35) * mm, "end": v(-85.26, 145.76) * mm});
            skArc(sketch, "E296", {"start": v(-85.26, 145.76) * mm, "mid": v(-85.9, 140.84) * mm, "end": v(-86.4, 135.9) * mm});
            skArc(sketch, "E297", {"start": v(-86.4, 135.9) * mm, "mid": v(-86.65, 131.9) * mm, "end": v(-86.68, 127.88) * mm});
            skArc(sketch, "E298", {"start": v(-86.68, 127.88) * mm, "mid": v(-86.5, 124.42) * mm, "end": v(-86.1, 120.98) * mm});
            skArc(sketch, "E299", {"start": v(-86.1, 120.98) * mm, "mid": v(-85.5, 117.77) * mm, "end": v(-84.66, 114.62) * mm});
            skArc(sketch, "E300", {"start": v(-84.66, 114.62) * mm, "mid": v(-83.69, 111.62) * mm, "end": v(-82.63, 108.64) * mm});
            skArc(sketch, "E301", {"start": v(-82.63, 108.64) * mm, "mid": v(-81.71, 106.4) * mm, "end": v(-80.65, 104.23) * mm});
            skArc(sketch, "E302", {"start": v(-80.65, 104.23) * mm, "mid": v(-79.63, 102.45) * mm, "end": v(-78.47, 100.76) * mm});
            skArc(sketch, "E303", {"start": v(-78.47, 100.76) * mm, "mid": v(-77.2, 99.2) * mm, "end": v(-75.8, 97.77) * mm});
            skLineSegment(sketch, "E304", {"start": v(-75.8, 97.77) * mm, "end": v(-72.65, 94.77) * mm});
            skLineSegment(sketch, "E305", {"start": v(-72.65, 94.77) * mm, "end": v(-74.7, 99.27) * mm});
            skArc(sketch, "E306", {"start": v(-74.7, 99.27) * mm, "mid": v(-75.45, 101.1) * mm, "end": v(-76.1, 102.97) * mm});
            skArc(sketch, "E307", {"start": v(-76.1, 102.97) * mm, "mid": v(-76.47, 104.53) * mm, "end": v(-76.67, 106.12) * mm});
            skArc(sketch, "E308", {"start": v(-76.67, 106.12) * mm, "mid": v(-76.64, 107.29) * mm, "end": v(-76.42, 108.43) * mm});
            skArc(sketch, "E309", {"start": v(-76.42, 108.43) * mm, "mid": v(-76.02, 109.14) * mm, "end": v(-75.34, 109.6) * mm});
            skArc(sketch, "E310", {"start": v(-75.34, 109.6) * mm, "mid": v(-73.96, 109.7) * mm, "end": v(-72.76, 109) * mm});
            skArc(sketch, "E311", {"start": v(-72.76, 109) * mm, "mid": v(-70.34, 106.21) * mm, "end": v(-68.06, 103.32) * mm});
            skArc(sketch, "E312", {"start": v(-68.06, 103.32) * mm, "mid": v(-65.89, 100.24) * mm, "end": v(-63.9, 97.04) * mm});
            skArc(sketch, "E313", {"start": v(-63.9, 97.04) * mm, "mid": v(-63.06, 95) * mm, "end": v(-62.77, 92.82) * mm});
            skArc(sketch, "E314", {"start": v(-62.77, 92.82) * mm, "mid": v(-63.59, 90.85) * mm, "end": v(-65.55, 90.03) * mm});
            skArc(sketch, "E315", {"start": v(-65.55, 90.03) * mm, "mid": v(-70.64, 90.21) * mm, "end": v(-75.7, 90.84) * mm});
            skArc(sketch, "E316", {"start": v(-75.7, 90.84) * mm, "mid": v(-81.95, 92.15) * mm, "end": v(-88.08, 93.96) * mm});
            skArc(sketch, "E317", {"start": v(-88.08, 93.96) * mm, "mid": v(-93.85, 96.2) * mm, "end": v(-99.4, 98.96) * mm});
            skArc(sketch, "E318", {"start": v(-99.4, 98.96) * mm, "mid": v(-102.4, 100.81) * mm, "end": v(-105.19, 102.96) * mm});
            skArc(sketch, "E319", {"start": v(-105.19, 102.96) * mm, "mid": v(-108.56, 106) * mm, "end": v(-111.78, 109.19) * mm});
            skArc(sketch, "E320", {"start": v(-111.78, 109.19) * mm, "mid": v(-114.83, 112.5) * mm, "end": v(-117.72, 115.98) * mm});
            skArc(sketch, "E321", {"start": v(-117.72, 115.98) * mm, "mid": v(-119.7, 118.77) * mm, "end": v(-121.35, 121.76) * mm});
            skArc(sketch, "E322", {"start": v(-121.35, 121.76) * mm, "mid": v(-122.24, 123.69) * mm, "end": v(-123.03, 125.65) * mm});
            skArc(sketch, "E323", {"start": v(-123.03, 125.65) * mm, "mid": v(-123.52, 127.16) * mm, "end": v(-123.84, 128.7) * mm});
            skArc(sketch, "E324", {"start": v(-123.84, 128.7) * mm, "mid": v(-124.07, 130.63) * mm, "end": v(-124.17, 132.56) * mm});
            skArc(sketch, "E325", {"start": v(-124.17, 132.56) * mm, "mid": v(-124.22, 136.41) * mm, "end": v(-124.22, 140.26) * mm});
            skArc(sketch, "E326", {"start": v(-124.22, 140.26) * mm, "mid": v(-124.18, 144) * mm, "end": v(-124.08, 147.73) * mm});
            skArc(sketch, "E327", {"start": v(-124.08, 147.73) * mm, "mid": v(-123.94, 150.02) * mm, "end": v(-123.66, 152.29) * mm});
            skArc(sketch, "E328", {"start": v(-123.66, 152.29) * mm, "mid": v(-123.27, 154.39) * mm, "end": v(-122.75, 156.45) * mm});
            skArc(sketch, "E329", {"start": v(-122.75, 156.45) * mm, "mid": v(-121.86, 159.37) * mm, "end": v(-120.91, 162.26) * mm});
            skArc(sketch, "E330", {"start": v(-120.91, 162.26) * mm, "mid": v(-119.46, 166.3) * mm, "end": v(-117.89, 170.28) * mm});
            skArc(sketch, "E331", {"start": v(-117.89, 170.28) * mm, "mid": v(-116.53, 173.28) * mm, "end": v(-114.97, 176.19) * mm});
            skArc(sketch, "E332", {"start": v(-114.97, 176.19) * mm, "mid": v(-113.3, 178.86) * mm, "end": v(-111.43, 181.41) * mm});
            skArc(sketch, "E333", {"start": v(-111.43, 181.41) * mm, "mid": v(-109.01, 184.35) * mm, "end": v(-106.48, 187.2) * mm});
            skArc(sketch, "E334", {"start": v(-106.48, 187.2) * mm, "mid": v(-105.24, 188.57) * mm, "end": v(-104.05, 189.98) * mm});
            skArc(sketch, "E335", {"start": v(-104.05, 189.98) * mm, "mid": v(-102.85, 191.48) * mm, "end": v(-101.7, 193.01) * mm});
            skArc(sketch, "E336", {"start": v(-101.7, 193.01) * mm, "mid": v(-100.69, 194.42) * mm, "end": v(-99.72, 195.86) * mm});
            skArc(sketch, "E337", {"start": v(-99.72, 195.86) * mm, "mid": v(-99.1, 196.9) * mm, "end": v(-98.58, 197.97) * mm});
            skArc(sketch, "E338", {"start": v(-98.58, 197.97) * mm, "mid": v(-97.28, 201.38) * mm, "end": v(-96.35, 204.92) * mm});
            skArc(sketch, "E339", {"start": v(-96.35, 204.92) * mm, "mid": v(-95.67, 208.94) * mm, "end": v(-95.3, 213) * mm});
            skArc(sketch, "E340", {"start": v(-95.3, 213) * mm, "mid": v(-95.26, 216.7) * mm, "end": v(-95.5, 220.4) * mm});
            skArc(sketch, "E341", {"start": v(-95.5, 220.4) * mm, "mid": v(-96.05, 222.72) * mm, "end": v(-97.2, 224.82) * mm});
            skArc(sketch, "E342", {"start": v(-97.2, 224.82) * mm, "mid": v(-97.46, 225.03) * mm, "end": v(-97.8, 225.06) * mm});
            skArc(sketch, "E343", {"start": v(-97.8, 225.06) * mm, "mid": v(-98.13, 224.91) * mm, "end": v(-98.34, 224.62) * mm});
            skArc(sketch, "E344", {"start": v(-98.34, 224.62) * mm, "mid": v(-98.62, 223.74) * mm, "end": v(-98.82, 222.84) * mm});
            skArc(sketch, "E345", {"start": v(-98.82, 222.84) * mm, "mid": v(-99.14, 220.84) * mm, "end": v(-99.45, 218.84) * mm});
            skArc(sketch, "E346", {"start": v(-41.65, 206.51) * mm, "mid": v(-42.31, 205.43) * mm, "end": v(-43.1, 204.44) * mm});
            skArc(sketch, "E347", {"start": v(-43.1, 204.44) * mm, "mid": v(-44.17, 203.31) * mm, "end": v(-45.3, 202.26) * mm});
            skArc(sketch, "E348", {"start": v(-45.3, 202.26) * mm, "mid": v(-46.4, 201.37) * mm, "end": v(-47.52, 200.53) * mm});
            skArc(sketch, "E349", {"start": v(-47.52, 200.53) * mm, "mid": v(-48, 200.4) * mm, "end": v(-48.45, 200.6) * mm});
            skArc(sketch, "E350", {"start": v(-48.45, 200.6) * mm, "mid": v(-48.56, 200.83) * mm, "end": v(-48.53, 201.07) * mm});
            skArc(sketch, "E351", {"start": v(-48.53, 201.07) * mm, "mid": v(-48.25, 201.6) * mm, "end": v(-47.94, 202.11) * mm});
            skArc(sketch, "E352", {"start": v(-47.94, 202.11) * mm, "mid": v(-47.5, 202.77) * mm, "end": v(-47, 203.4) * mm});
            skArc(sketch, "E353", {"start": v(-47, 203.4) * mm, "mid": v(-46.4, 204.1) * mm, "end": v(-45.76, 204.78) * mm});
            skArc(sketch, "E354", {"start": v(-45.76, 204.78) * mm, "mid": v(-44.57, 205.97) * mm, "end": v(-43.34, 207.12) * mm});
            skArc(sketch, "E355", {"start": v(-43.34, 207.12) * mm, "mid": v(-42.6, 207.68) * mm, "end": v(-41.77, 208.12) * mm});
            skArc(sketch, "E356", {"start": v(-41.77, 208.12) * mm, "mid": v(-41.43, 208.08) * mm, "end": v(-41.29, 207.78) * mm});
            skArc(sketch, "E357", {"start": v(-41.29, 207.78) * mm, "mid": v(-41.4, 207.13) * mm, "end": v(-41.65, 206.51) * mm});
            skArc(sketch, "E358", {"start": v(96.78, 222.76) * mm, "mid": v(96.3, 221.6) * mm, "end": v(95.92, 220.42) * mm});
            skArc(sketch, "E359", {"start": v(95.92, 220.42) * mm, "mid": v(95.64, 219.27) * mm, "end": v(95.46, 218.1) * mm});
            skArc(sketch, "E360", {"start": v(95.46, 218.1) * mm, "mid": v(95.36, 216.71) * mm, "end": v(95.34, 215.33) * mm});
            skArc(sketch, "E361", {"start": v(95.34, 215.33) * mm, "mid": v(95.4, 213.42) * mm, "end": v(95.53, 211.52) * mm});
            skArc(sketch, "E362", {"start": v(95.53, 211.52) * mm, "mid": v(95.93, 208.09) * mm, "end": v(96.61, 204.7) * mm});
            skArc(sketch, "E363", {"start": v(96.61, 204.7) * mm, "mid": v(97.54, 201.59) * mm, "end": v(98.78, 198.58) * mm});
            skArc(sketch, "E364", {"start": v(98.78, 198.58) * mm, "mid": v(100.35, 195.6) * mm, "end": v(102.2, 192.8) * mm});
            skArc(sketch, "E365", {"start": v(102.2, 192.8) * mm, "mid": v(104.54, 189.8) * mm, "end": v(107.08, 186.96) * mm});
            skArc(sketch, "E366", {"start": v(107.08, 186.96) * mm, "mid": v(109.65, 184.14) * mm, "end": v(112.1, 181.22) * mm});
            skArc(sketch, "E367", {"start": v(112.1, 181.22) * mm, "mid": v(114.1, 178.53) * mm, "end": v(115.95, 175.72) * mm});
            skArc(sketch, "E368", {"start": v(115.95, 175.72) * mm, "mid": v(117.6, 172.81) * mm, "end": v(119.05, 169.8) * mm});
            skArc(sketch, "E369", {"start": v(119.05, 169.8) * mm, "mid": v(120.52, 166.31) * mm, "end": v(121.83, 162.76) * mm});
            skArc(sketch, "E370", {"start": v(121.83, 162.76) * mm, "mid": v(122.6, 160.4) * mm, "end": v(123.28, 158.03) * mm});
            skArc(sketch, "E371", {"start": v(123.28, 158.03) * mm, "mid": v(123.75, 156.1) * mm, "end": v(124.1, 154.13) * mm});
            skArc(sketch, "E372", {"start": v(124.1, 154.13) * mm, "mid": v(124.35, 151.95) * mm, "end": v(124.5, 149.75) * mm});
            skArc(sketch, "E373", {"start": v(124.5, 149.75) * mm, "mid": v(124.6, 146.5) * mm, "end": v(124.65, 143.26) * mm});
            skArc(sketch, "E374", {"start": v(124.65, 143.26) * mm, "mid": v(124.65, 139.64) * mm, "end": v(124.6, 136.02) * mm});
            skArc(sketch, "E375", {"start": v(124.6, 136.02) * mm, "mid": v(124.5, 134.19) * mm, "end": v(124.25, 132.37) * mm});
            skArc(sketch, "E376", {"start": v(124.25, 132.37) * mm, "mid": v(123.88, 130.8) * mm, "end": v(123.34, 129.27) * mm});
            skArc(sketch, "E377", {"start": v(123.34, 129.27) * mm, "mid": v(122.36, 127) * mm, "end": v(121.32, 124.76) * mm});
            skArc(sketch, "E378", {"start": v(121.32, 124.76) * mm, "mid": v(120.32, 122.85) * mm, "end": v(119.23, 120.99) * mm});
            skArc(sketch, "E379", {"start": v(119.23, 120.99) * mm, "mid": v(118.03, 119.16) * mm, "end": v(116.75, 117.4) * mm});
            skArc(sketch, "E380", {"start": v(116.75, 117.4) * mm, "mid": v(115.2, 115.47) * mm, "end": v(113.56, 113.6) * mm});
            skArc(sketch, "E381", {"start": v(113.56, 113.6) * mm, "mid": v(111.46, 111.36) * mm, "end": v(109.32, 109.16) * mm});
            skArc(sketch, "E382", {"start": v(109.32, 109.16) * mm, "mid": v(106.9, 106.79) * mm, "end": v(104.42, 104.47) * mm});
            skArc(sketch, "E383", {"start": v(104.42, 104.47) * mm, "mid": v(102.52, 102.83) * mm, "end": v(100.54, 101.29) * mm});
            skArc(sketch, "E384", {"start": v(100.54, 101.29) * mm, "mid": v(98.56, 99.92) * mm, "end": v(96.5, 98.67) * mm});
            skArc(sketch, "E385", {"start": v(96.5, 98.67) * mm, "mid": v(93.84, 97.2) * mm, "end": v(91.14, 95.82) * mm});
            skArc(sketch, "E386", {"start": v(91.14, 95.82) * mm, "mid": v(88.85, 94.72) * mm, "end": v(86.52, 93.67) * mm});
            skArc(sketch, "E387", {"start": v(86.52, 93.67) * mm, "mid": v(84.5, 92.83) * mm, "end": v(82.46, 92.07) * mm});
            skArc(sketch, "E388", {"start": v(82.46, 92.07) * mm, "mid": v(80.66, 91.49) * mm, "end": v(78.85, 90.98) * mm});
            skArc(sketch, "E389", {"start": v(78.85, 90.98) * mm, "mid": v(77.25, 90.63) * mm, "end": v(75.63, 90.38) * mm});
            skArc(sketch, "E390", {"start": v(75.63, 90.38) * mm, "mid": v(73.6, 90.2) * mm, "end": v(71.56, 90.11) * mm});
            skArc(sketch, "E391", {"start": v(71.56, 90.11) * mm, "mid": v(69.54, 90.13) * mm, "end": v(67.53, 90.26) * mm});
            skArc(sketch, "E392", {"start": v(67.53, 90.26) * mm, "mid": v(65.84, 90.45) * mm, "end": v(64.15, 90.73) * mm});
            skArc(sketch, "E393", {"start": v(64.15, 90.73) * mm, "mid": v(63.32, 91.02) * mm, "end": v(62.6, 91.55) * mm});
            skArc(sketch, "E394", {"start": v(62.6, 91.55) * mm, "mid": v(62.35, 92.05) * mm, "end": v(62.42, 92.6) * mm});
            skArc(sketch, "E395", {"start": v(62.42, 92.6) * mm, "mid": v(63.4, 94.64) * mm, "end": v(64.43, 96.66) * mm});
            skArc(sketch, "E396", {"start": v(64.43, 96.66) * mm, "mid": v(65.63, 98.87) * mm, "end": v(66.9, 101.03) * mm});
            skArc(sketch, "E397", {"start": v(66.9, 101.03) * mm, "mid": v(68.2, 103.03) * mm, "end": v(69.6, 104.98) * mm});
            skArc(sketch, "E398", {"start": v(69.6, 104.98) * mm, "mid": v(71.3, 107.03) * mm, "end": v(73.22, 108.87) * mm});
            skArc(sketch, "E399", {"start": v(73.22, 108.87) * mm, "mid": v(74.5, 109.41) * mm, "end": v(75.87, 109.1) * mm});
            skArc(sketch, "E400", {"start": v(75.87, 109.1) * mm, "mid": v(76.83, 108.06) * mm, "end": v(77.03, 106.66) * mm});
            skArc(sketch, "E401", {"start": v(77.03, 106.66) * mm, "mid": v(76.45, 104.03) * mm, "end": v(75.6, 101.48) * mm});
            skArc(sketch, "E402", {"start": v(75.6, 101.48) * mm, "mid": v(75.22, 100.54) * mm, "end": v(74.85, 99.6) * mm});
            skArc(sketch, "E403", {"start": v(74.85, 99.6) * mm, "mid": v(74.5, 98.73) * mm, "end": v(74.16, 97.86) * mm});
            skArc(sketch, "E404", {"start": v(74.16, 97.86) * mm, "mid": v(73.87, 97.13) * mm, "end": v(73.58, 96.4) * mm});
            skArc(sketch, "E405", {"start": v(73.58, 96.4) * mm, "mid": v(73.46, 96.08) * mm, "end": v(73.34, 95.77) * mm});
            skArc(sketch, "E406", {"start": v(73.34, 95.77) * mm, "mid": v(73.36, 95.66) * mm, "end": v(73.45, 95.63) * mm});
            skArc(sketch, "E407", {"start": v(73.45, 95.63) * mm, "mid": v(73.67, 95.7) * mm, "end": v(73.87, 95.8) * mm});
            skArc(sketch, "E408", {"start": v(73.87, 95.8) * mm, "mid": v(74.27, 96.07) * mm, "end": v(74.66, 96.37) * mm});
            skArc(sketch, "E409", {"start": v(74.66, 96.37) * mm, "mid": v(75.18, 96.8) * mm, "end": v(75.68, 97.26) * mm});
            skArc(sketch, "E410", {"start": v(75.68, 97.26) * mm, "mid": v(77.25, 98.85) * mm, "end": v(78.66, 100.6) * mm});
            skArc(sketch, "E411", {"start": v(78.66, 100.6) * mm, "mid": v(80, 102.62) * mm, "end": v(81.2, 104.75) * mm});
            skArc(sketch, "E412", {"start": v(81.2, 104.75) * mm, "mid": v(82.37, 107.3) * mm, "end": v(83.38, 109.9) * mm});
            skArc(sketch, "E413", {"start": v(83.38, 109.9) * mm, "mid": v(84.4, 113.06) * mm, "end": v(85.3, 116.26) * mm});
            skArc(sketch, "E414", {"start": v(85.3, 116.26) * mm, "mid": v(85.96, 118.92) * mm, "end": v(86.56, 121.6) * mm});
            skArc(sketch, "E415", {"start": v(86.56, 121.6) * mm, "mid": v(86.86, 123.39) * mm, "end": v(87.01, 125.2) * mm});
            skArc(sketch, "E416", {"start": v(87.01, 125.2) * mm, "mid": v(87.04, 127.18) * mm, "end": v(86.94, 129.16) * mm});
            skArc(sketch, "E417", {"start": v(86.94, 129.16) * mm, "mid": v(86.62, 132.72) * mm, "end": v(86.26, 136.26) * mm});
            skArc(sketch, "E418", {"start": v(86.26, 136.26) * mm, "mid": v(86, 138.67) * mm, "end": v(85.74, 141.07) * mm});
            skArc(sketch, "E419", {"start": v(85.74, 141.07) * mm, "mid": v(85.48, 143.53) * mm, "end": v(85.23, 146) * mm});
            skArc(sketch, "E420", {"start": v(85.23, 146) * mm, "mid": v(85.02, 148.2) * mm, "end": v(84.8, 150.39) * mm});
            skArc(sketch, "E421", {"start": v(84.8, 150.39) * mm, "mid": v(84.67, 151.83) * mm, "end": v(84.55, 153.26) * mm});
            skLineSegment(sketch, "E422", {"start": v(84.55, 153.26) * mm, "end": v(84.1, 158.76) * mm});
            skLineSegment(sketch, "E423", {"start": v(84.1, 158.76) * mm, "end": v(86.14, 156.26) * mm});
            skArc(sketch, "E424", {"start": v(86.14, 156.26) * mm, "mid": v(86.62, 155.63) * mm, "end": v(87.05, 154.96) * mm});
            skArc(sketch, "E425", {"start": v(87.05, 154.96) * mm, "mid": v(87.59, 154) * mm, "end": v(88.1, 153.03) * mm});
            skArc(sketch, "E426", {"start": v(88.1, 153.03) * mm, "mid": v(88.63, 151.95) * mm, "end": v(89.13, 150.86) * mm});
            skArc(sketch, "E427", {"start": v(89.13, 150.86) * mm, "mid": v(89.56, 149.82) * mm, "end": v(89.95, 148.76) * mm});
            skLineSegment(sketch, "E428", {"start": v(89.95, 148.76) * mm, "end": v(91.73, 143.76) * mm});
            skLineSegment(sketch, "E429", {"start": v(91.73, 143.76) * mm, "end": v(92.05, 148.26) * mm});
            skArc(sketch, "E430", {"start": v(92.05, 148.26) * mm, "mid": v(92.07, 151.2) * mm, "end": v(91.69, 154.13) * mm});
            skArc(sketch, "E431", {"start": v(91.69, 154.13) * mm, "mid": v(90.88, 157.43) * mm, "end": v(89.79, 160.66) * mm});
            skArc(sketch, "E432", {"start": v(89.79, 160.66) * mm, "mid": v(88.19, 164.37) * mm, "end": v(86.32, 167.96) * mm});
            skArc(sketch, "E433", {"start": v(86.32, 167.96) * mm, "mid": v(83.83, 172.15) * mm, "end": v(81.17, 176.22) * mm});
            skArc(sketch, "E434", {"start": v(81.17, 176.22) * mm, "mid": v(79.59, 178.69) * mm, "end": v(78.15, 181.24) * mm});
            skArc(sketch, "E435", {"start": v(78.15, 181.24) * mm, "mid": v(76.71, 184.1) * mm, "end": v(75.4, 187) * mm});
            skArc(sketch, "E436", {"start": v(75.4, 187) * mm, "mid": v(74.3, 189.7) * mm, "end": v(73.28, 192.41) * mm});
            skArc(sketch, "E437", {"start": v(73.28, 192.41) * mm, "mid": v(73.22, 193.26) * mm, "end": v(73.63, 194) * mm});
            skArc(sketch, "E438", {"start": v(73.63, 194) * mm, "mid": v(74.46, 194.43) * mm, "end": v(75.38, 194.28) * mm});
            skArc(sketch, "E439", {"start": v(75.38, 194.28) * mm, "mid": v(77.39, 193.2) * mm, "end": v(79.33, 191.99) * mm});
            skArc(sketch, "E440", {"start": v(79.33, 191.99) * mm, "mid": v(81.36, 190.52) * mm, "end": v(83.29, 188.9) * mm});
            skArc(sketch, "E441", {"start": v(83.29, 188.9) * mm, "mid": v(84.67, 187.47) * mm, "end": v(85.84, 185.85) * mm});
            skLineSegment(sketch, "E442", {"start": v(85.84, 185.85) * mm, "end": v(88.39, 181.76) * mm});
            skLineSegment(sketch, "E443", {"start": v(88.39, 181.76) * mm, "end": v(87.72, 185.7) * mm});
            skArc(sketch, "E444", {"start": v(87.72, 185.7) * mm, "mid": v(87.3, 187.71) * mm, "end": v(86.67, 189.67) * mm});
            skArc(sketch, "E445", {"start": v(86.67, 189.67) * mm, "mid": v(85.77, 191.92) * mm, "end": v(84.74, 194.12) * mm});
            skArc(sketch, "E446", {"start": v(84.74, 194.12) * mm, "mid": v(83.62, 196.18) * mm, "end": v(82.4, 198.18) * mm});
            skArc(sketch, "E447", {"start": v(82.4, 198.18) * mm, "mid": v(81.32, 199.6) * mm, "end": v(80.07, 200.89) * mm});
            skArc(sketch, "E448", {"start": v(80.07, 200.89) * mm, "mid": v(79.44, 201.43) * mm, "end": v(78.78, 201.95) * mm});
            skArc(sketch, "E449", {"start": v(78.78, 201.95) * mm, "mid": v(77.72, 202.74) * mm, "end": v(76.65, 203.5) * mm});
            skArc(sketch, "E450", {"start": v(76.65, 203.5) * mm, "mid": v(75.43, 204.37) * mm, "end": v(74.2, 205.21) * mm});
            skArc(sketch, "E451", {"start": v(74.2, 205.21) * mm, "mid": v(72.97, 206.03) * mm, "end": v(71.73, 206.83) * mm});
            skArc(sketch, "E452", {"start": v(71.73, 206.83) * mm, "mid": v(70.44, 207.67) * mm, "end": v(69.17, 208.53) * mm});
            skArc(sketch, "E453", {"start": v(69.17, 208.53) * mm, "mid": v(67.8, 209.5) * mm, "end": v(66.45, 210.5) * mm});
            skArc(sketch, "E454", {"start": v(66.45, 210.5) * mm, "mid": v(65.2, 211.44) * mm, "end": v(63.97, 212.41) * mm});
            skArc(sketch, "E455", {"start": v(63.97, 212.41) * mm, "mid": v(63.07, 213.16) * mm, "end": v(62.2, 213.94) * mm});
            skArc(sketch, "E456", {"start": v(62.2, 213.94) * mm, "mid": v(60.64, 215.2) * mm, "end": v(58.91, 216.24) * mm});
            skArc(sketch, "E457", {"start": v(58.91, 216.24) * mm, "mid": v(56.83, 217.18) * mm, "end": v(54.66, 217.91) * mm});
            skArc(sketch, "E458", {"start": v(54.66, 217.91) * mm, "mid": v(52.11, 218.53) * mm, "end": v(49.53, 218.93) * mm});
            skArc(sketch, "E459", {"start": v(49.53, 218.93) * mm, "mid": v(46.55, 219.18) * mm, "end": v(43.57, 219.26) * mm});
            skArc(sketch, "E460", {"start": v(43.57, 219.26) * mm, "mid": v(42.45, 219.3) * mm, "end": v(41.34, 219.44) * mm});
            skArc(sketch, "E461", {"start": v(41.34, 219.44) * mm, "mid": v(40.14, 219.67) * mm, "end": v(38.97, 219.97) * mm});
            skArc(sketch, "E462", {"start": v(38.97, 219.97) * mm, "mid": v(37.71, 220.38) * mm, "end": v(36.49, 220.85) * mm});
            skArc(sketch, "E463", {"start": v(36.49, 220.85) * mm, "mid": v(35.2, 221.43) * mm, "end": v(33.92, 222.07) * mm});
            skArc(sketch, "E464", {"start": v(33.92, 222.07) * mm, "mid": v(32.31, 222.9) * mm, "end": v(30.67, 223.65) * mm});
            skArc(sketch, "E465", {"start": v(30.67, 223.65) * mm, "mid": v(29.54, 224.07) * mm, "end": v(28.36, 224.34) * mm});
            skArc(sketch, "E466", {"start": v(28.36, 224.34) * mm, "mid": v(27.09, 224.5) * mm, "end": v(25.8, 224.51) * mm});
            skArc(sketch, "E467", {"start": v(25.8, 224.51) * mm, "mid": v(23.64, 224.4) * mm, "end": v(21.48, 224.22) * mm});
            skArc(sketch, "E468", {"start": v(21.48, 224.22) * mm, "mid": v(19.01, 223.94) * mm, "end": v(16.57, 223.57) * mm});
            skArc(sketch, "E469", {"start": v(16.57, 223.57) * mm, "mid": v(15, 223.18) * mm, "end": v(13.52, 222.58) * mm});
            skArc(sketch, "E470", {"start": v(13.52, 222.58) * mm, "mid": v(12.6, 221.97) * mm, "end": v(11.84, 221.16) * mm});
            skArc(sketch, "E471", {"start": v(11.84, 221.16) * mm, "mid": v(11.38, 220.24) * mm, "end": v(11.23, 219.22) * mm});
            skArc(sketch, "E472", {"start": v(11.23, 219.22) * mm, "mid": v(11.38, 218.1) * mm, "end": v(11.84, 217.09) * mm});
            skArc(sketch, "E473", {"start": v(11.84, 217.09) * mm, "mid": v(12.85, 215.62) * mm, "end": v(13.97, 214.22) * mm});
            skArc(sketch, "E474", {"start": v(13.97, 214.22) * mm, "mid": v(15.3, 212.8) * mm, "end": v(16.75, 211.48) * mm});
            skArc(sketch, "E475", {"start": v(16.75, 211.48) * mm, "mid": v(18.12, 210.44) * mm, "end": v(19.6, 209.57) * mm});
            skArc(sketch, "E476", {"start": v(19.6, 209.57) * mm, "mid": v(20.92, 208.82) * mm, "end": v(22.18, 207.96) * mm});
            skArc(sketch, "E477", {"start": v(22.18, 207.96) * mm, "mid": v(23.12, 207.13) * mm, "end": v(23.93, 206.18) * mm});
            skArc(sketch, "E478", {"start": v(23.93, 206.18) * mm, "mid": v(24.75, 204.93) * mm, "end": v(25.42, 203.6) * mm});
            skArc(sketch, "E479", {"start": v(25.42, 203.6) * mm, "mid": v(26.37, 201.37) * mm, "end": v(27.26, 199.1) * mm});
            skArc(sketch, "E480", {"start": v(27.26, 199.1) * mm, "mid": v(27.74, 197.93) * mm, "end": v(28.26, 196.77) * mm});
            skArc(sketch, "E481", {"start": v(28.26, 196.77) * mm, "mid": v(28.85, 195.59) * mm, "end": v(29.5, 194.43) * mm});
            skArc(sketch, "E482", {"start": v(29.5, 194.43) * mm, "mid": v(30.1, 193.41) * mm, "end": v(30.76, 192.42) * mm});
            skArc(sketch, "E483", {"start": v(30.76, 192.42) * mm, "mid": v(31.27, 191.75) * mm, "end": v(31.85, 191.15) * mm});
            skLineSegment(sketch, "E484", {"start": v(31.85, 191.15) * mm, "end": v(34.3, 188.85) * mm});
            skLineSegment(sketch, "E485", {"start": v(34.3, 188.85) * mm, "end": v(32.2, 193.6) * mm});
            skArc(sketch, "E486", {"start": v(32.2, 193.6) * mm, "mid": v(31.79, 194.57) * mm, "end": v(31.42, 195.57) * mm});
            skArc(sketch, "E487", {"start": v(31.42, 195.57) * mm, "mid": v(31.1, 196.57) * mm, "end": v(30.8, 197.58) * mm});
            skArc(sketch, "E488", {"start": v(30.8, 197.58) * mm, "mid": v(30.6, 198.46) * mm, "end": v(30.43, 199.36) * mm});
            skArc(sketch, "E489", {"start": v(30.43, 199.36) * mm, "mid": v(30.37, 199.92) * mm, "end": v(30.41, 200.5) * mm});
            skArc(sketch, "E490", {"start": v(30.41, 200.5) * mm, "mid": v(30.52, 200.99) * mm, "end": v(30.7, 201.46) * mm});
            skArc(sketch, "E491", {"start": v(30.7, 201.46) * mm, "mid": v(30.87, 201.62) * mm, "end": v(31.11, 201.6) * mm});
            skArc(sketch, "E492", {"start": v(31.11, 201.6) * mm, "mid": v(31.48, 201.3) * mm, "end": v(31.78, 200.95) * mm});
            skArc(sketch, "E493", {"start": v(31.78, 200.95) * mm, "mid": v(32.54, 199.83) * mm, "end": v(33.28, 198.7) * mm});
            skArc(sketch, "E494", {"start": v(33.28, 198.7) * mm, "mid": v(33.85, 197.78) * mm, "end": v(34.4, 196.83) * mm});
            skArc(sketch, "E495", {"start": v(34.4, 196.83) * mm, "mid": v(35.02, 195.65) * mm, "end": v(35.63, 194.45) * mm});
            skArc(sketch, "E496", {"start": v(35.63, 194.45) * mm, "mid": v(36.22, 193.21) * mm, "end": v(36.79, 191.96) * mm});
            skArc(sketch, "E497", {"start": v(36.79, 191.96) * mm, "mid": v(37.25, 190.87) * mm, "end": v(37.68, 189.76) * mm});
            skArc(sketch, "E498", {"start": v(37.68, 189.76) * mm, "mid": v(38.73, 187.24) * mm, "end": v(40, 184.82) * mm});
            skArc(sketch, "E499", {"start": v(40, 184.82) * mm, "mid": v(41.97, 181.5) * mm, "end": v(44.04, 178.26) * mm});
            skArc(sketch, "E500", {"start": v(44.04, 178.26) * mm, "mid": v(46.22, 175.07) * mm, "end": v(48.5, 171.95) * mm});
            skArc(sketch, "E501", {"start": v(48.5, 171.95) * mm, "mid": v(50.27, 169.79) * mm, "end": v(52.21, 167.77) * mm});
            skArc(sketch, "E502", {"start": v(52.21, 167.77) * mm, "mid": v(53.28, 166.8) * mm, "end": v(54.38, 165.85) * mm});
            skArc(sketch, "E503", {"start": v(54.38, 165.85) * mm, "mid": v(54.75, 165.76) * mm, "end": v(55.06, 165.99) * mm});
            skArc(sketch, "E504", {"start": v(55.06, 165.99) * mm, "mid": v(55.21, 166.51) * mm, "end": v(55.13, 167.05) * mm});
            skArc(sketch, "E505", {"start": v(55.13, 167.05) * mm, "mid": v(54.45, 168.84) * mm, "end": v(53.73, 170.6) * mm});
            skArc(sketch, "E506", {"start": v(53.73, 170.6) * mm, "mid": v(53.16, 172.2) * mm, "end": v(52.75, 173.83) * mm});
            skArc(sketch, "E507", {"start": v(52.75, 173.83) * mm, "mid": v(52.45, 175.68) * mm, "end": v(52.3, 177.55) * mm});
            skArc(sketch, "E508", {"start": v(52.3, 177.55) * mm, "mid": v(52.28, 179.27) * mm, "end": v(52.39, 180.99) * mm});
            skArc(sketch, "E509", {"start": v(52.39, 180.99) * mm, "mid": v(52.63, 182.1) * mm, "end": v(53.13, 183.14) * mm});
            skArc(sketch, "E510", {"start": v(53.13, 183.14) * mm, "mid": v(53.36, 183.45) * mm, "end": v(53.64, 183.7) * mm});
            skArc(sketch, "E511", {"start": v(53.64, 183.7) * mm, "mid": v(53.89, 183.8) * mm, "end": v(54.14, 183.76) * mm});
            skArc(sketch, "E512", {"start": v(54.14, 183.76) * mm, "mid": v(54.46, 183.58) * mm, "end": v(54.72, 183.32) * mm});
            skArc(sketch, "E513", {"start": v(54.72, 183.32) * mm, "mid": v(55.15, 182.74) * mm, "end": v(55.56, 182.14) * mm});
            skArc(sketch, "E514", {"start": v(55.56, 182.14) * mm, "mid": v(56.56, 180.36) * mm, "end": v(57.3, 178.45) * mm});
            skArc(sketch, "E515", {"start": v(57.3, 178.45) * mm, "mid": v(57.95, 176.02) * mm, "end": v(58.43, 173.54) * mm});
            skArc(sketch, "E516", {"start": v(58.43, 173.54) * mm, "mid": v(58.77, 170.63) * mm, "end": v(58.93, 167.7) * mm});
            skArc(sketch, "E517", {"start": v(58.93, 167.7) * mm, "mid": v(58.92, 164.47) * mm, "end": v(58.75, 161.23) * mm});
            skArc(sketch, "E518", {"start": v(58.75, 161.23) * mm, "mid": v(58.63, 159.27) * mm, "end": v(58.54, 157.31) * mm});
            skArc(sketch, "E519", {"start": v(58.54, 157.31) * mm, "mid": v(58.52, 155.7) * mm, "end": v(58.57, 154.1) * mm});
            skArc(sketch, "E520", {"start": v(58.57, 154.1) * mm, "mid": v(58.66, 152.81) * mm, "end": v(58.8, 151.54) * mm});
            skArc(sketch, "E521", {"start": v(58.8, 151.54) * mm, "mid": v(59, 150.62) * mm, "end": v(59.3, 149.73) * mm});
            skLineSegment(sketch, "E522", {"start": v(59.3, 149.73) * mm, "end": v(60.47, 146.76) * mm});
            skLineSegment(sketch, "E523", {"start": v(60.47, 146.76) * mm, "end": v(61.84, 152.6) * mm});
            skArc(sketch, "E524", {"start": v(61.84, 152.6) * mm, "mid": v(62.6, 155.72) * mm, "end": v(63.4, 158.83) * mm});
            skArc(sketch, "E525", {"start": v(63.4, 158.83) * mm, "mid": v(63.75, 159.61) * mm, "end": v(64.33, 160.24) * mm});
            skArc(sketch, "E526", {"start": v(64.33, 160.24) * mm, "mid": v(64.79, 160.29) * mm, "end": v(65.05, 159.9) * mm});
            skArc(sketch, "E527", {"start": v(65.05, 159.9) * mm, "mid": v(65.15, 157.52) * mm, "end": v(65.2, 155.14) * mm});
            skArc(sketch, "E528", {"start": v(65.2, 155.14) * mm, "mid": v(65, 151.2) * mm, "end": v(64.38, 147.33) * mm});
            skArc(sketch, "E529", {"start": v(64.38, 147.33) * mm, "mid": v(63.37, 143.74) * mm, "end": v(61.91, 140.3) * mm});
            skArc(sketch, "E530", {"start": v(61.91, 140.3) * mm, "mid": v(60, 137.02) * mm, "end": v(57.7, 134) * mm});
            skArc(sketch, "E531", {"start": v(57.7, 134) * mm, "mid": v(54.85, 131) * mm, "end": v(51.73, 128.3) * mm});
            skArc(sketch, "E532", {"start": v(51.73, 128.3) * mm, "mid": v(50.89, 127.63) * mm, "end": v(50.06, 126.95) * mm});
            skArc(sketch, "E533", {"start": v(50.06, 126.95) * mm, "mid": v(49.39, 126.35) * mm, "end": v(48.73, 125.74) * mm});
            skArc(sketch, "E534", {"start": v(48.73, 125.74) * mm, "mid": v(48.21, 125.24) * mm, "end": v(47.71, 124.72) * mm});
            skArc(sketch, "E535", {"start": v(47.71, 124.72) * mm, "mid": v(47.66, 124.58) * mm, "end": v(47.72, 124.44) * mm});
            skArc(sketch, "E536", {"start": v(47.72, 124.44) * mm, "mid": v(47.87, 124.35) * mm, "end": v(48.05, 124.34) * mm});
            skArc(sketch, "E537", {"start": v(48.05, 124.34) * mm, "mid": v(48.7, 124.47) * mm, "end": v(49.34, 124.61) * mm});
            skArc(sketch, "E538", {"start": v(49.34, 124.61) * mm, "mid": v(50.12, 124.8) * mm, "end": v(50.9, 125.02) * mm});
            skArc(sketch, "E539", {"start": v(50.9, 125.02) * mm, "mid": v(51.79, 125.3) * mm, "end": v(52.67, 125.59) * mm});
            skArc(sketch, "E540", {"start": v(52.67, 125.59) * mm, "mid": v(53.54, 125.87) * mm, "end": v(54.42, 126.13) * mm});
            skArc(sketch, "E541", {"start": v(54.42, 126.13) * mm, "mid": v(55.15, 126.3) * mm, "end": v(55.89, 126.44) * mm});
            skArc(sketch, "E542", {"start": v(55.89, 126.44) * mm, "mid": v(56.43, 126.52) * mm, "end": v(56.98, 126.56) * mm});
            skArc(sketch, "E543", {"start": v(56.98, 126.56) * mm, "mid": v(57.15, 126.5) * mm, "end": v(57.23, 126.32) * mm});
            skArc(sketch, "E544", {"start": v(57.23, 126.32) * mm, "mid": v(57.07, 125.55) * mm, "end": v(56.64, 124.9) * mm});
            skArc(sketch, "E545", {"start": v(56.64, 124.9) * mm, "mid": v(54.65, 122.9) * mm, "end": v(52.62, 120.93) * mm});
            skArc(sketch, "E546", {"start": v(52.62, 120.93) * mm, "mid": v(50.53, 119) * mm, "end": v(48.38, 117.11) * mm});
            skArc(sketch, "E547", {"start": v(48.38, 117.11) * mm, "mid": v(46.7, 115.79) * mm, "end": v(44.93, 114.58) * mm});
            skArc(sketch, "E548", {"start": v(44.93, 114.58) * mm, "mid": v(43.91, 114) * mm, "end": v(42.85, 113.5) * mm});
            skArc(sketch, "E549", {"start": v(42.85, 113.5) * mm, "mid": v(41.16, 112.8) * mm, "end": v(39.45, 112.16) * mm});
            skArc(sketch, "E550", {"start": v(39.45, 112.16) * mm, "mid": v(37.5, 111.47) * mm, "end": v(35.53, 110.83) * mm});
            skArc(sketch, "E551", {"start": v(35.53, 110.83) * mm, "mid": v(33.57, 110.24) * mm, "end": v(31.6, 109.7) * mm});
            skArc(sketch, "E552", {"start": v(31.6, 109.7) * mm, "mid": v(29.66, 109.19) * mm, "end": v(27.72, 108.64) * mm});
            skArc(sketch, "E553", {"start": v(27.72, 108.64) * mm, "mid": v(25.85, 108.08) * mm, "end": v(23.98, 107.5) * mm});
            skArc(sketch, "E554", {"start": v(23.98, 107.5) * mm, "mid": v(22.39, 106.98) * mm, "end": v(20.8, 106.43) * mm});
            skArc(sketch, "E555", {"start": v(20.8, 106.43) * mm, "mid": v(19.93, 106.09) * mm, "end": v(19.08, 105.69) * mm});
            skArc(sketch, "E556", {"start": v(19.08, 105.69) * mm, "mid": v(17.51, 104.79) * mm, "end": v(16.03, 103.75) * mm});
            skArc(sketch, "E557", {"start": v(16.03, 103.75) * mm, "mid": v(14.11, 102.22) * mm, "end": v(12.25, 100.63) * mm});
            skArc(sketch, "E558", {"start": v(12.25, 100.63) * mm, "mid": v(10.5, 99.02) * mm, "end": v(8.8, 97.34) * mm});
            skArc(sketch, "E559", {"start": v(8.8, 97.34) * mm, "mid": v(7.87, 96.26) * mm, "end": v(7.1, 95.05) * mm});
            skArc(sketch, "E560", {"start": v(7.1, 95.05) * mm, "mid": v(6.86, 94.54) * mm, "end": v(6.65, 94.01) * mm});
            skArc(sketch, "E561", {"start": v(6.65, 94.01) * mm, "mid": v(6.68, 93.83) * mm, "end": v(6.86, 93.75) * mm});
            skArc(sketch, "E562", {"start": v(6.86, 93.75) * mm, "mid": v(7.24, 93.81) * mm, "end": v(7.6, 93.95) * mm});
            skArc(sketch, "E563", {"start": v(7.6, 93.95) * mm, "mid": v(8.92, 94.6) * mm, "end": v(10.24, 95.27) * mm});
            skArc(sketch, "E564", {"start": v(10.24, 95.27) * mm, "mid": v(11.12, 95.69) * mm, "end": v(12.02, 96.05) * mm});
            skArc(sketch, "E565", {"start": v(12.02, 96.05) * mm, "mid": v(12.97, 96.39) * mm, "end": v(13.95, 96.67) * mm});
            skArc(sketch, "E566", {"start": v(13.95, 96.67) * mm, "mid": v(14.84, 96.88) * mm, "end": v(15.74, 97.05) * mm});
            skArc(sketch, "E567", {"start": v(15.74, 97.05) * mm, "mid": v(16.39, 97.1) * mm, "end": v(17.05, 97.07) * mm});
            skArc(sketch, "E568", {"start": v(17.05, 97.07) * mm, "mid": v(17.44, 96.82) * mm, "end": v(17.48, 96.36) * mm});
            skArc(sketch, "E569", {"start": v(17.48, 96.36) * mm, "mid": v(17.12, 95.67) * mm, "end": v(16.59, 95.1) * mm});
            skArc(sketch, "E570", {"start": v(16.59, 95.1) * mm, "mid": v(14.94, 93.82) * mm, "end": v(13.22, 92.62) * mm});
            skArc(sketch, "E571", {"start": v(13.22, 92.62) * mm, "mid": v(9.23, 89.98) * mm, "end": v(5.22, 87.37) * mm});
            skArc(sketch, "E572", {"start": v(5.22, 87.37) * mm, "mid": v(-3.07, 81.89) * mm, "end": v(-11.27, 76.26) * mm});
            skArc(sketch, "E573", {"start": v(-11.27, 76.26) * mm, "mid": v(-16.79, 72.2) * mm, "end": v(-22.1, 67.85) * mm});
            skArc(sketch, "E574", {"start": v(-22.1, 67.85) * mm, "mid": v(-26.67, 63.67) * mm, "end": v(-30.98, 59.22) * mm});
            skArc(sketch, "E575", {"start": v(-30.98, 59.22) * mm, "mid": v(-35.96, 53.58) * mm, "end": v(-40.75, 47.77) * mm});
            skArc(sketch, "E576", {"start": v(-40.75, 47.77) * mm, "mid": v(-45.6, 41.51) * mm, "end": v(-50.31, 35.14) * mm});
            skArc(sketch, "E577", {"start": v(-50.31, 35.14) * mm, "mid": v(-53.53, 30.37) * mm, "end": v(-56.44, 25.4) * mm});
            skArc(sketch, "E578", {"start": v(-56.44, 25.4) * mm, "mid": v(-58.62, 21.03) * mm, "end": v(-60.44, 16.5) * mm});
            skArc(sketch, "E579", {"start": v(-60.44, 16.5) * mm, "mid": v(-61.98, 11.66) * mm, "end": v(-63.19, 6.73) * mm});
            skArc(sketch, "E580", {"start": v(-63.19, 6.73) * mm, "mid": v(-63.51, 5.05) * mm, "end": v(-63.8, 3.36) * mm});
            skArc(sketch, "E581", {"start": v(-63.8, 3.36) * mm, "mid": v(-64.07, 1.46) * mm, "end": v(-64.3, -0.44) * mm});
            skArc(sketch, "E582", {"start": v(-64.3, -0.44) * mm, "mid": v(-64.5, -2.25) * mm, "end": v(-64.66, -4.07) * mm});
            skArc(sketch, "E583", {"start": v(-64.66, -4.07) * mm, "mid": v(-64.75, -5.48) * mm, "end": v(-64.77, -6.89) * mm});
            skArc(sketch, "E584", {"start": v(-64.77, -6.89) * mm, "mid": v(-64.69, -9.73) * mm, "end": v(-64.42, -12.56) * mm});
            skArc(sketch, "E585", {"start": v(-64.42, -12.56) * mm, "mid": v(-63.9, -16.18) * mm, "end": v(-63.3, -19.78) * mm});
            skArc(sketch, "E586", {"start": v(-63.3, -19.78) * mm, "mid": v(-62.58, -23.3) * mm, "end": v(-61.76, -26.8) * mm});
            skArc(sketch, "E587", {"start": v(-61.76, -26.8) * mm, "mid": v(-61.04, -29.3) * mm, "end": v(-60.13, -31.74) * mm});
            skArc(sketch, "E588", {"start": v(-60.13, -31.74) * mm, "mid": v(-59.42, -33.23) * mm, "end": v(-58.57, -34.65) * mm});
            skArc(sketch, "E589", {"start": v(-58.57, -34.65) * mm, "mid": v(-57.47, -36.2) * mm, "end": v(-56.27, -37.67) * mm});
            skArc(sketch, "E590", {"start": v(-56.27, -37.67) * mm, "mid": v(-55.11, -38.93) * mm, "end": v(-53.89, -40.13) * mm});
            skArc(sketch, "E591", {"start": v(-53.89, -40.13) * mm, "mid": v(-53.17, -40.58) * mm, "end": v(-52.34, -40.73) * mm});
            skArc(sketch, "E592", {"start": v(-52.34, -40.73) * mm, "mid": v(-52.08, -40.65) * mm, "end": v(-51.91, -40.45) * mm});
            skArc(sketch, "E593", {"start": v(-51.91, -40.45) * mm, "mid": v(-51.7, -39.88) * mm, "end": v(-51.52, -39.3) * mm});
            skArc(sketch, "E594", {"start": v(-51.52, -39.3) * mm, "mid": v(-51.34, -38.53) * mm, "end": v(-51.2, -37.75) * mm});
            skArc(sketch, "E595", {"start": v(-51.2, -37.75) * mm, "mid": v(-51.1, -36.83) * mm, "end": v(-51.04, -35.9) * mm});
            skArc(sketch, "E596", {"start": v(-51.04, -35.9) * mm, "mid": v(-50.62, -32.22) * mm, "end": v(-49.72, -28.63) * mm});
            skArc(sketch, "E597", {"start": v(-49.72, -28.63) * mm, "mid": v(-48.37, -25.3) * mm, "end": v(-46.56, -22.2) * mm});
            skArc(sketch, "E598", {"start": v(-46.56, -22.2) * mm, "mid": v(-44.27, -19.31) * mm, "end": v(-41.6, -16.78) * mm});
            skArc(sketch, "E599", {"start": v(-41.6, -16.78) * mm, "mid": v(-38.43, -14.47) * mm, "end": v(-35, -12.53) * mm});
            skArc(sketch, "E600", {"start": v(-35, -12.53) * mm, "mid": v(-33.06, -11.6) * mm, "end": v(-31.08, -10.75) * mm});
            skArc(sketch, "E601", {"start": v(-31.08, -10.75) * mm, "mid": v(-29.66, -10.23) * mm, "end": v(-28.2, -9.83) * mm});
            skArc(sketch, "E602", {"start": v(-28.2, -9.83) * mm, "mid": v(-26.7, -9.56) * mm, "end": v(-25.18, -9.42) * mm});
            skArc(sketch, "E603", {"start": v(-25.18, -9.42) * mm, "mid": v(-23, -9.35) * mm, "end": v(-20.81, -9.34) * mm});
            skArc(sketch, "E604", {"start": v(-20.81, -9.34) * mm, "mid": v(-18.89, -9.39) * mm, "end": v(-16.97, -9.5) * mm});
            skArc(sketch, "E605", {"start": v(-16.97, -9.5) * mm, "mid": v(-15.37, -9.67) * mm, "end": v(-13.77, -9.92) * mm});
            skArc(sketch, "E606", {"start": v(-13.77, -9.92) * mm, "mid": v(-12.32, -10.24) * mm, "end": v(-10.88, -10.64) * mm});
            skArc(sketch, "E607", {"start": v(-10.88, -10.64) * mm, "mid": v(-9.4, -11.15) * mm, "end": v(-7.96, -11.73) * mm});
            skLineSegment(sketch, "E608", {"start": v(-7.96, -11.73) * mm, "end": v(-2.65, -14.04) * mm});
            skLineSegment(sketch, "E609", {"start": v(-2.65, -14.04) * mm, "end": v(11.21, -9.74) * mm});
            skArc(sketch, "E610", {"start": v(11.21, -9.74) * mm, "mid": v(13.92, -8.9) * mm, "end": v(16.62, -8.04) * mm});
            skArc(sketch, "E611", {"start": v(16.62, -8.04) * mm, "mid": v(19, -7.27) * mm, "end": v(21.38, -6.48) * mm});
            skArc(sketch, "E612", {"start": v(21.38, -6.48) * mm, "mid": v(23.4, -5.8) * mm, "end": v(25.4, -5.11) * mm});
            skArc(sketch, "E613", {"start": v(25.4, -5.11) * mm, "mid": v(25.89, -4.91) * mm, "end": v(26.36, -4.66) * mm});
            skArc(sketch, "E614", {"start": v(26.36, -4.66) * mm, "mid": v(26.82, -3.94) * mm, "end": v(26.56, -3.13) * mm});
            skArc(sketch, "E615", {"start": v(26.56, -3.13) * mm, "mid": v(24.37, -0.9) * mm, "end": v(22.1, 1.25) * mm});
            skArc(sketch, "E616", {"start": v(22.1, 1.25) * mm, "mid": v(19.35, 3.6) * mm, "end": v(16.5, 5.8) * mm});
            skArc(sketch, "E617", {"start": v(16.5, 5.8) * mm, "mid": v(13.76, 7.66) * mm, "end": v(10.9, 9.33) * mm});
            skArc(sketch, "E618", {"start": v(10.9, 9.33) * mm, "mid": v(7.9, 10.8) * mm, "end": v(4.78, 12.04) * mm});
            skArc(sketch, "E619", {"start": v(4.78, 12.04) * mm, "mid": v(1.96, 12.88) * mm, "end": v(-0.94, 13.4) * mm});
            skArc(sketch, "E620", {"start": v(-0.94, 13.4) * mm, "mid": v(-4.63, 13.7) * mm, "end": v(-8.34, 13.74) * mm});
            skArc(sketch, "E621", {"start": v(-8.34, 13.74) * mm, "mid": v(-14.65, 13.51) * mm, "end": v(-20.95, 13.18) * mm});
            skArc(sketch, "E622", {"start": v(-20.95, 13.18) * mm, "mid": v(-22.25, 13.12) * mm, "end": v(-23.55, 13.07) * mm});
            skArc(sketch, "E623", {"start": v(-23.55, 13.07) * mm, "mid": v(-24.7, 13.06) * mm, "end": v(-25.85, 13.08) * mm});
            skArc(sketch, "E624", {"start": v(-25.85, 13.08) * mm, "mid": v(-26.8, 13.12) * mm, "end": v(-27.74, 13.18) * mm});
            skArc(sketch, "E625", {"start": v(-27.74, 13.18) * mm, "mid": v(-28.02, 13.25) * mm, "end": v(-28.26, 13.41) * mm});
            skArc(sketch, "E626", {"start": v(-28.26, 13.41) * mm, "mid": v(-28.64, 14.11) * mm, "end": v(-28.58, 14.9) * mm});
            skArc(sketch, "E627", {"start": v(-28.58, 14.9) * mm, "mid": v(-27.9, 16.5) * mm, "end": v(-27.1, 18.03) * mm});
            skArc(sketch, "E628", {"start": v(-27.1, 18.03) * mm, "mid": v(-26.02, 19.8) * mm, "end": v(-24.8, 21.46) * mm});
            skArc(sketch, "E629", {"start": v(-24.8, 21.46) * mm, "mid": v(-23.49, 22.99) * mm, "end": v(-22.05, 24.4) * mm});
            skArc(sketch, "E630", {"start": v(-22.05, 24.4) * mm, "mid": v(-21.02, 25.27) * mm, "end": v(-19.94, 26.09) * mm});
            skArc(sketch, "E631", {"start": v(-19.94, 26.09) * mm, "mid": v(-18.37, 27.18) * mm, "end": v(-16.78, 28.23) * mm});
            skArc(sketch, "E632", {"start": v(-16.78, 28.23) * mm, "mid": v(-15, 29.34) * mm, "end": v(-13.21, 30.42) * mm});
            skArc(sketch, "E633", {"start": v(-13.21, 30.42) * mm, "mid": v(-11.5, 31.4) * mm, "end": v(-9.75, 32.34) * mm});
            skArc(sketch, "E634", {"start": v(-9.75, 32.34) * mm, "mid": v(-7.6, 33.5) * mm, "end": v(-5.52, 34.76) * mm});
            skArc(sketch, "E635", {"start": v(-5.52, 34.76) * mm, "mid": v(-3.39, 36.16) * mm, "end": v(-1.3, 37.63) * mm});
            skArc(sketch, "E636", {"start": v(-1.3, 37.63) * mm, "mid": v(0.87, 39.3) * mm, "end": v(3, 41.02) * mm});
            skArc(sketch, "E637", {"start": v(3, 41.02) * mm, "mid": v(5.27, 42.99) * mm, "end": v(7.49, 45) * mm});
            skArc(sketch, "E638", {"start": v(7.49, 45) * mm, "mid": v(9.22, 46.6) * mm, "end": v(10.96, 48.18) * mm});
            skArc(sketch, "E639", {"start": v(10.96, 48.18) * mm, "mid": v(12.45, 49.48) * mm, "end": v(13.97, 50.76) * mm});
            skArc(sketch, "E640", {"start": v(13.97, 50.76) * mm, "mid": v(15.26, 51.82) * mm, "end": v(16.56, 52.87) * mm});
            skArc(sketch, "E641", {"start": v(16.56, 52.87) * mm, "mid": v(16.77, 52.94) * mm, "end": v(16.97, 52.85) * mm});
            skArc(sketch, "E642", {"start": v(16.97, 52.85) * mm, "mid": v(17.25, 52.35) * mm, "end": v(17.22, 51.79) * mm});
            skArc(sketch, "E643", {"start": v(17.22, 51.79) * mm, "mid": v(16.67, 50.27) * mm, "end": v(16.06, 48.77) * mm});
            skArc(sketch, "E644", {"start": v(16.06, 48.77) * mm, "mid": v(15.28, 47.1) * mm, "end": v(14.42, 45.47) * mm});
            skArc(sketch, "E645", {"start": v(14.42, 45.47) * mm, "mid": v(13.52, 43.97) * mm, "end": v(12.53, 42.53) * mm});
            skArc(sketch, "E646", {"start": v(12.53, 42.53) * mm, "mid": v(11.94, 41.8) * mm, "end": v(11.3, 41.1) * mm});
            skArc(sketch, "E647", {"start": v(11.3, 41.1) * mm, "mid": v(10.43, 40.28) * mm, "end": v(9.53, 39.48) * mm});
            skArc(sketch, "E648", {"start": v(9.53, 39.48) * mm, "mid": v(8.55, 38.68) * mm, "end": v(7.55, 37.91) * mm});
            skArc(sketch, "E649", {"start": v(7.55, 37.91) * mm, "mid": v(6.61, 37.26) * mm, "end": v(5.65, 36.66) * mm});
            skArc(sketch, "E650", {"start": v(5.65, 36.66) * mm, "mid": v(4.8, 36.15) * mm, "end": v(3.94, 35.62) * mm});
            skArc(sketch, "E651", {"start": v(3.94, 35.62) * mm, "mid": v(3.25, 35.17) * mm, "end": v(2.57, 34.69) * mm});
            skArc(sketch, "E652", {"start": v(2.57, 34.69) * mm, "mid": v(2.04, 34.3) * mm, "end": v(1.52, 33.9) * mm});
            skArc(sketch, "E653", {"start": v(1.52, 33.9) * mm, "mid": v(1.46, 33.77) * mm, "end": v(1.5, 33.65) * mm});
            skArc(sketch, "E654", {"start": v(1.5, 33.65) * mm, "mid": v(2.15, 33.29) * mm, "end": v(2.89, 33.3) * mm});
            skArc(sketch, "E655", {"start": v(2.89, 33.3) * mm, "mid": v(5.5, 34.12) * mm, "end": v(8.08, 35) * mm});
            skArc(sketch, "E656", {"start": v(8.08, 35) * mm, "mid": v(10.78, 36) * mm, "end": v(13.44, 37.11) * mm});
            skArc(sketch, "E657", {"start": v(13.44, 37.11) * mm, "mid": v(15.64, 38.16) * mm, "end": v(17.77, 39.35) * mm});
            skArc(sketch, "E658", {"start": v(17.77, 39.35) * mm, "mid": v(19.23, 40.29) * mm, "end": v(20.64, 41.3) * mm});
            skArc(sketch, "E659", {"start": v(20.64, 41.3) * mm, "mid": v(22.76, 42.96) * mm, "end": v(24.85, 44.65) * mm});
            skArc(sketch, "E660", {"start": v(24.85, 44.65) * mm, "mid": v(27.19, 46.6) * mm, "end": v(29.5, 48.59) * mm});
            skArc(sketch, "E661", {"start": v(29.5, 48.59) * mm, "mid": v(31.72, 50.58) * mm, "end": v(33.92, 52.6) * mm});
            skArc(sketch, "E662", {"start": v(33.92, 52.6) * mm, "mid": v(37.27, 55.74) * mm, "end": v(40.65, 58.85) * mm});
            skArc(sketch, "E663", {"start": v(40.65, 58.85) * mm, "mid": v(42.01, 60) * mm, "end": v(43.46, 61.03) * mm});
            skArc(sketch, "E664", {"start": v(43.46, 61.03) * mm, "mid": v(44.47, 61.54) * mm, "end": v(45.56, 61.82) * mm});
            skArc(sketch, "E665", {"start": v(45.56, 61.82) * mm, "mid": v(46.8, 61.9) * mm, "end": v(48.02, 61.77) * mm});
            skArc(sketch, "E666", {"start": v(48.02, 61.77) * mm, "mid": v(49.59, 61.43) * mm, "end": v(51.13, 60.98) * mm});
            skArc(sketch, "E667", {"start": v(51.13, 60.98) * mm, "mid": v(52.6, 60.45) * mm, "end": v(54.02, 59.82) * mm});
            skArc(sketch, "E668", {"start": v(54.02, 59.82) * mm, "mid": v(55.27, 59.16) * mm, "end": v(56.45, 58.4) * mm});
            skArc(sketch, "E669", {"start": v(56.45, 58.4) * mm, "mid": v(57.35, 57.7) * mm, "end": v(58.14, 56.87) * mm});
            skArc(sketch, "E670", {"start": v(58.14, 56.87) * mm, "mid": v(58.92, 55.69) * mm, "end": v(59.43, 54.37) * mm});
            skArc(sketch, "E671", {"start": v(59.43, 54.37) * mm, "mid": v(59.77, 52.67) * mm, "end": v(59.91, 50.95) * mm});
            skArc(sketch, "E672", {"start": v(59.91, 50.95) * mm, "mid": v(59.84, 49.1) * mm, "end": v(59.57, 47.28) * mm});
            skArc(sketch, "E673", {"start": v(59.57, 47.28) * mm, "mid": v(59.1, 45.6) * mm, "end": v(58.4, 44.01) * mm});
            skArc(sketch, "E674", {"start": v(58.4, 44.01) * mm, "mid": v(58.03, 43.3) * mm, "end": v(57.68, 42.57) * mm});
            skArc(sketch, "E675", {"start": v(57.68, 42.57) * mm, "mid": v(57.4, 41.97) * mm, "end": v(57.14, 41.36) * mm});
            skArc(sketch, "E676", {"start": v(57.14, 41.36) * mm, "mid": v(56.95, 40.89) * mm, "end": v(56.77, 40.4) * mm});
            skArc(sketch, "E677", {"start": v(56.77, 40.4) * mm, "mid": v(56.79, 40.3) * mm, "end": v(56.87, 40.26) * mm});
            skArc(sketch, "E678", {"start": v(56.87, 40.26) * mm, "mid": v(57.02, 40.28) * mm, "end": v(57.17, 40.33) * mm});
            skArc(sketch, "E679", {"start": v(57.17, 40.33) * mm, "mid": v(57.76, 40.59) * mm, "end": v(58.34, 40.86) * mm});
            skArc(sketch, "E680", {"start": v(58.34, 40.86) * mm, "mid": v(59.03, 41.18) * mm, "end": v(59.72, 41.5) * mm});
            skArc(sketch, "E681", {"start": v(59.72, 41.5) * mm, "mid": v(60.5, 41.9) * mm, "end": v(61.26, 42.28) * mm});
            skArc(sketch, "E682", {"start": v(61.26, 42.28) * mm, "mid": v(62.85, 43.22) * mm, "end": v(64.3, 44.35) * mm});
            skArc(sketch, "E683", {"start": v(64.3, 44.35) * mm, "mid": v(65.73, 45.74) * mm, "end": v(67.01, 47.26) * mm});
            skArc(sketch, "E684", {"start": v(67.01, 47.26) * mm, "mid": v(68.51, 49.38) * mm, "end": v(69.86, 51.59) * mm});
            skArc(sketch, "E685", {"start": v(69.86, 51.59) * mm, "mid": v(71.69, 54.9) * mm, "end": v(73.44, 58.26) * mm});
            skArc(sketch, "E686", {"start": v(73.44, 58.26) * mm, "mid": v(74.35, 60.01) * mm, "end": v(75.3, 61.74) * mm});
            skArc(sketch, "E687", {"start": v(75.3, 61.74) * mm, "mid": v(75.92, 62.71) * mm, "end": v(76.64, 63.6) * mm});
            skArc(sketch, "E688", {"start": v(76.64, 63.6) * mm, "mid": v(77.24, 64.17) * mm, "end": v(77.94, 64.6) * mm});
            skArc(sketch, "E689", {"start": v(77.94, 64.6) * mm, "mid": v(78.72, 64.92) * mm, "end": v(79.54, 65.08) * mm});
            skArc(sketch, "E690", {"start": v(79.54, 65.08) * mm, "mid": v(81.65, 65.03) * mm, "end": v(83.66, 64.38) * mm});
            skArc(sketch, "E691", {"start": v(83.66, 64.38) * mm, "mid": v(85.6, 63.15) * mm, "end": v(87.2, 61.52) * mm});
            skArc(sketch, "E692", {"start": v(87.2, 61.52) * mm, "mid": v(88.62, 59.32) * mm, "end": v(89.61, 56.9) * mm});
            skArc(sketch, "E693", {"start": v(89.61, 56.9) * mm, "mid": v(90.25, 54.07) * mm, "end": v(90.5, 51.19) * mm});
            skArc(sketch, "E694", {"start": v(90.5, 51.19) * mm, "mid": v(90.42, 49.3) * mm, "end": v(90.14, 47.42) * mm});
            skArc(sketch, "E695", {"start": v(90.14, 47.42) * mm, "mid": v(89.7, 45.8) * mm, "end": v(89, 44.26) * mm});
            skArc(sketch, "E696", {"start": v(89, 44.26) * mm, "mid": v(87.97, 42.6) * mm, "end": v(86.76, 41.07) * mm});
            skArc(sketch, "E697", {"start": v(86.76, 41.07) * mm, "mid": v(84.85, 39.03) * mm, "end": v(82.85, 37.07) * mm});
            skLineSegment(sketch, "E698", {"start": v(82.85, 37.07) * mm, "end": v(78.73, 33.18) * mm});
            skLineSegment(sketch, "E699", {"start": v(78.73, 33.18) * mm, "end": v(81.73, 33.85) * mm});
            skArc(sketch, "E700", {"start": v(81.73, 33.85) * mm, "mid": v(83.77, 34.39) * mm, "end": v(85.77, 35.09) * mm});
            skArc(sketch, "E701", {"start": v(85.77, 35.09) * mm, "mid": v(87.58, 35.91) * mm, "end": v(89.3, 36.9) * mm});
            skArc(sketch, "E702", {"start": v(89.3, 36.9) * mm, "mid": v(91.15, 38.2) * mm, "end": v(92.88, 39.62) * mm});
            skArc(sketch, "E703", {"start": v(92.88, 39.62) * mm, "mid": v(95.02, 41.63) * mm, "end": v(97.1, 43.7) * mm});
            skArc(sketch, "E704", {"start": v(97.1, 43.7) * mm, "mid": v(98.78, 45.54) * mm, "end": v(100.39, 47.45) * mm});
            skArc(sketch, "E705", {"start": v(100.39, 47.45) * mm, "mid": v(101.8, 49.31) * mm, "end": v(103.13, 51.25) * mm});
            skArc(sketch, "E706", {"start": v(103.13, 51.25) * mm, "mid": v(104.53, 53.55) * mm, "end": v(105.84, 55.9) * mm});
            skArc(sketch, "E707", {"start": v(105.84, 55.9) * mm, "mid": v(107.5, 59.13) * mm, "end": v(109.1, 62.38) * mm});
            skArc(sketch, "E708", {"start": v(109.1, 62.38) * mm, "mid": v(113.05, 70.05) * mm, "end": v(117.4, 77.5) * mm});
            skArc(sketch, "E709", {"start": v(117.4, 77.5) * mm, "mid": v(120.44, 81.16) * mm, "end": v(124.36, 83.86) * mm});
            skArc(sketch, "E710", {"start": v(124.36, 83.86) * mm, "mid": v(127.46, 84.35) * mm, "end": v(130.28, 82.98) * mm});
            skArc(sketch, "E711", {"start": v(130.28, 82.98) * mm, "mid": v(133.2, 79.52) * mm, "end": v(135.29, 75.49) * mm});
            skArc(sketch, "E712", {"start": v(135.29, 75.49) * mm, "mid": v(136.37, 72.06) * mm, "end": v(137.05, 68.52) * mm});
            skArc(sketch, "E713", {"start": v(137.05, 68.52) * mm, "mid": v(137.63, 63.28) * mm, "end": v(138, 58.03) * mm});
            skArc(sketch, "E714", {"start": v(138, 58.03) * mm, "mid": v(138.18, 52.47) * mm, "end": v(138.14, 46.9) * mm});
            skArc(sketch, "E715", {"start": v(138.14, 46.9) * mm, "mid": v(137.85, 42.22) * mm, "end": v(137.26, 37.56) * mm});
            skArc(sketch, "E716", {"start": v(137.26, 37.56) * mm, "mid": v(135.5, 28.93) * mm, "end": v(133.02, 20.47) * mm});
            skArc(sketch, "E717", {"start": v(133.02, 20.47) * mm, "mid": v(129.87, 12.3) * mm, "end": v(126.04, 4.4) * mm});
            skArc(sketch, "E718", {"start": v(126.04, 4.4) * mm, "mid": v(121.31, -3.58) * mm, "end": v(115.97, -11.18) * mm});
            skArc(sketch, "E719", {"start": v(115.97, -11.18) * mm, "mid": v(109.45, -19.23) * mm, "end": v(102.49, -26.9) * mm});
            skArc(sketch, "E720", {"start": v(102.49, -26.9) * mm, "mid": v(99.84, -29.7) * mm, "end": v(97.24, -32.52) * mm});
            skArc(sketch, "E721", {"start": v(97.24, -32.52) * mm, "mid": v(95.23, -34.8) * mm, "end": v(93.29, -37.15) * mm});
            skArc(sketch, "E722", {"start": v(93.29, -37.15) * mm, "mid": v(91.82, -39.04) * mm, "end": v(90.43, -40.99) * mm});
            skArc(sketch, "E723", {"start": v(90.43, -40.99) * mm, "mid": v(89.48, -42.5) * mm, "end": v(88.67, -44.08) * mm});
            skArc(sketch, "E724", {"start": v(88.67, -44.08) * mm, "mid": v(86.33, -50.36) * mm, "end": v(84.93, -56.9) * mm});
            skArc(sketch, "E725", {"start": v(84.93, -56.9) * mm, "mid": v(84.48, -63.62) * mm, "end": v(85, -70.33) * mm});
            skArc(sketch, "E726", {"start": v(85, -70.33) * mm, "mid": v(86.4, -76.46) * mm, "end": v(88.72, -82.3) * mm});
            skArc(sketch, "E727", {"start": v(88.72, -82.3) * mm, "mid": v(91.69, -86.95) * mm, "end": v(95.63, -90.84) * mm});
            skLineSegment(sketch, "E728", {"start": v(95.63, -90.84) * mm, "end": v(98.4, -93.02) * mm});
            skLineSegment(sketch, "E729", {"start": v(98.4, -93.02) * mm, "end": v(95.08, -86.63) * mm});
            skArc(sketch, "E730", {"start": v(95.08, -86.63) * mm, "mid": v(94.1, -84.65) * mm, "end": v(93.18, -82.65) * mm});
            skArc(sketch, "E731", {"start": v(93.18, -82.65) * mm, "mid": v(92.65, -81.23) * mm, "end": v(92.26, -79.76) * mm});
            skArc(sketch, "E732", {"start": v(92.26, -79.76) * mm, "mid": v(92, -78.12) * mm, "end": v(91.86, -76.47) * mm});
            skArc(sketch, "E733", {"start": v(91.86, -76.47) * mm, "mid": v(91.78, -73.6) * mm, "end": v(91.75, -70.74) * mm});
            skArc(sketch, "E734", {"start": v(91.75, -70.74) * mm, "mid": v(91.89, -66.18) * mm, "end": v(92.32, -61.65) * mm});
            skArc(sketch, "E735", {"start": v(92.32, -61.65) * mm, "mid": v(93, -58.21) * mm, "end": v(94.13, -54.9) * mm});
            skArc(sketch, "E736", {"start": v(94.13, -54.9) * mm, "mid": v(95.69, -51.84) * mm, "end": v(97.66, -49.03) * mm});
            skArc(sketch, "E737", {"start": v(97.66, -49.03) * mm, "mid": v(100.5, -45.78) * mm, "end": v(103.57, -42.74) * mm});
            skArc(sketch, "E738", {"start": v(103.57, -42.74) * mm, "mid": v(105.43, -41) * mm, "end": v(107.28, -39.24) * mm});
            skArc(sketch, "E739", {"start": v(107.28, -39.24) * mm, "mid": v(110.2, -36.43) * mm, "end": v(113.1, -33.62) * mm});
            skArc(sketch, "E740", {"start": v(113.1, -33.62) * mm, "mid": v(116.38, -30.4) * mm, "end": v(119.65, -27.2) * mm});
            skArc(sketch, "E741", {"start": v(119.65, -27.2) * mm, "mid": v(122.88, -24) * mm, "end": v(126.1, -20.81) * mm});
            skArc(sketch, "E742", {"start": v(126.1, -20.81) * mm, "mid": v(129.03, -17.9) * mm, "end": v(131.99, -15.02) * mm});
            skArc(sketch, "E743", {"start": v(131.99, -15.02) * mm, "mid": v(134.4, -12.72) * mm, "end": v(136.82, -10.45) * mm});
            skArc(sketch, "E744", {"start": v(136.82, -10.45) * mm, "mid": v(138.7, -8.73) * mm, "end": v(140.6, -7.03) * mm});
            skArc(sketch, "E745", {"start": v(140.6, -7.03) * mm, "mid": v(140.81, -7.01) * mm, "end": v(140.87, -7.2) * mm});
            skArc(sketch, "E746", {"start": v(140.87, -7.2) * mm, "mid": v(140.22, -8.72) * mm, "end": v(139.44, -10.17) * mm});
            skArc(sketch, "E747", {"start": v(139.44, -10.17) * mm, "mid": v(136.44, -15.24) * mm, "end": v(133.41, -20.3) * mm});
            skArc(sketch, "E748", {"start": v(133.41, -20.3) * mm, "mid": v(130.4, -25.29) * mm, "end": v(127.35, -30.25) * mm});
            skArc(sketch, "E749", {"start": v(127.35, -30.25) * mm, "mid": v(125.2, -33.68) * mm, "end": v(122.96, -37.06) * mm});
            skArc(sketch, "E750", {"start": v(122.96, -37.06) * mm, "mid": v(120.93, -40.24) * mm, "end": v(119.02, -43.5) * mm});
            skArc(sketch, "E751", {"start": v(119.02, -43.5) * mm, "mid": v(117.36, -46.66) * mm, "end": v(115.86, -49.9) * mm});
            skArc(sketch, "E752", {"start": v(115.86, -49.9) * mm, "mid": v(114.67, -52.84) * mm, "end": v(113.65, -55.84) * mm});
            skArc(sketch, "E753", {"start": v(113.65, -55.84) * mm, "mid": v(113.01, -58.32) * mm, "end": v(112.63, -60.85) * mm});
            skLineSegment(sketch, "E754", {"start": v(112.63, -60.85) * mm, "end": v(112.1, -66.24) * mm});
            skLineSegment(sketch, "E755", {"start": v(112.1, -66.24) * mm, "end": v(114.65, -60.24) * mm});
            skArc(sketch, "E756", {"start": v(114.65, -60.24) * mm, "mid": v(115.15, -59.08) * mm, "end": v(115.64, -57.92) * mm});
            skArc(sketch, "E757", {"start": v(115.64, -57.92) * mm, "mid": v(116.05, -56.93) * mm, "end": v(116.47, -55.94) * mm});
            skArc(sketch, "E758", {"start": v(116.47, -55.94) * mm, "mid": v(116.83, -55.06) * mm, "end": v(117.19, -54.19) * mm});
            skArc(sketch, "E759", {"start": v(117.19, -54.19) * mm, "mid": v(117.21, -54.11) * mm, "end": v(117.22, -54.03) * mm});
            skArc(sketch, "E760", {"start": v(117.22, -54.03) * mm, "mid": v(117.24, -53.95) * mm, "end": v(117.27, -53.88) * mm});
            skArc(sketch, "E761", {"start": v(117.27, -53.88) * mm, "mid": v(118.7, -52.08) * mm, "end": v(120.1, -50.27) * mm});
            skArc(sketch, "E762", {"start": v(120.1, -50.27) * mm, "mid": v(121.69, -48.26) * mm, "end": v(123.27, -46.26) * mm});
            skArc(sketch, "E763", {"start": v(123.27, -46.26) * mm, "mid": v(125.15, -43.89) * mm, "end": v(127.04, -41.53) * mm});
            skArc(sketch, "E764", {"start": v(127.04, -41.53) * mm, "mid": v(132.76, -34.18) * mm, "end": v(138.32, -26.71) * mm});
            skArc(sketch, "E765", {"start": v(138.32, -26.71) * mm, "mid": v(142.54, -20.64) * mm, "end": v(146.48, -14.38) * mm});
            skArc(sketch, "E766", {"start": v(146.48, -14.38) * mm, "mid": v(149.86, -8.44) * mm, "end": v(152.93, -2.33) * mm});
            skArc(sketch, "E767", {"start": v(152.93, -2.33) * mm, "mid": v(156.03, 4.53) * mm, "end": v(158.87, 11.5) * mm});
            skArc(sketch, "E768", {"start": v(158.87, 11.5) * mm, "mid": v(162.28, 21.57) * mm, "end": v(164.84, 31.9) * mm});
            skArc(sketch, "E769", {"start": v(164.84, 31.9) * mm, "mid": v(166.64, 42.76) * mm, "end": v(167.6, 53.73) * mm});
            skArc(sketch, "E770", {"start": v(167.6, 53.73) * mm, "mid": v(167.76, 64.88) * mm, "end": v(167.08, 76) * mm});
            skArc(sketch, "E771", {"start": v(167.08, 76) * mm, "mid": v(165.59, 86.9) * mm, "end": v(163.25, 97.66) * mm});
            skArc(sketch, "E772", {"start": v(163.25, 97.66) * mm, "mid": v(162.1, 102.18) * mm, "end": v(160.94, 106.7) * mm});
            skArc(sketch, "E773", {"start": v(160.94, 106.7) * mm, "mid": v(160.66, 107.98) * mm, "end": v(160.46, 109.26) * mm});
            skArc(sketch, "E774", {"start": v(160.46, 109.26) * mm, "mid": v(160.58, 109.54) * mm, "end": v(160.88, 109.56) * mm});
            skArc(sketch, "E775", {"start": v(160.88, 109.56) * mm, "mid": v(161.4, 109.21) * mm, "end": v(161.84, 108.76) * mm});
            skArc(sketch, "E776", {"start": v(161.84, 108.76) * mm, "mid": v(163.2, 106.83) * mm, "end": v(164.4, 104.8) * mm});
            skArc(sketch, "E777", {"start": v(164.4, 104.8) * mm, "mid": v(165.8, 102.01) * mm, "end": v(167.1, 99.18) * mm});
            skArc(sketch, "E778", {"start": v(167.1, 99.18) * mm, "mid": v(168.43, 95.93) * mm, "end": v(169.65, 92.64) * mm});
            skArc(sketch, "E779", {"start": v(169.65, 92.64) * mm, "mid": v(170.8, 89.2) * mm, "end": v(171.83, 85.7) * mm});
            skArc(sketch, "E780", {"start": v(171.83, 85.7) * mm, "mid": v(172.59, 82.84) * mm, "end": v(173.28, 79.96) * mm});
            skArc(sketch, "E781", {"start": v(173.28, 79.96) * mm, "mid": v(173.74, 77.7) * mm, "end": v(174.08, 75.42) * mm});
            skArc(sketch, "E782", {"start": v(174.08, 75.42) * mm, "mid": v(174.32, 73.03) * mm, "end": v(174.45, 70.63) * mm});
            skArc(sketch, "E783", {"start": v(174.45, 70.63) * mm, "mid": v(174.52, 67.3) * mm, "end": v(174.53, 63.96) * mm});
            skArc(sketch, "E784", {"start": v(174.53, 63.96) * mm, "mid": v(174.52, 60.53) * mm, "end": v(174.53, 57.1) * mm});
            skArc(sketch, "E785", {"start": v(174.53, 57.1) * mm, "mid": v(174.58, 55.8) * mm, "end": v(174.72, 54.5) * mm});
            skArc(sketch, "E786", {"start": v(174.72, 54.5) * mm, "mid": v(174.88, 54.14) * mm, "end": v(175.2, 53.94) * mm});
            skArc(sketch, "E787", {"start": v(175.2, 53.94) * mm, "mid": v(175.58, 53.95) * mm, "end": v(175.88, 54.18) * mm});
            skArc(sketch, "E788", {"start": v(175.88, 54.18) * mm, "mid": v(177.87, 57.7) * mm, "end": v(179.14, 61.54) * mm});
            skArc(sketch, "E789", {"start": v(179.14, 61.54) * mm, "mid": v(180.08, 66.78) * mm, "end": v(180.57, 72.08) * mm});
            skArc(sketch, "E790", {"start": v(180.57, 72.08) * mm, "mid": v(180.62, 78.15) * mm, "end": v(180.18, 84.2) * mm});
            skArc(sketch, "E791", {"start": v(180.18, 84.2) * mm, "mid": v(179.27, 90.38) * mm, "end": v(177.9, 96.48) * mm});
            skArc(sketch, "E792", {"start": v(177.9, 96.48) * mm, "mid": v(176, 103.18) * mm, "end": v(173.8, 109.8) * mm});
            skArc(sketch, "E793", {"start": v(173.8, 109.8) * mm, "mid": v(171.54, 115.57) * mm, "end": v(168.93, 121.2) * mm});
            skArc(sketch, "E794", {"start": v(168.93, 121.2) * mm, "mid": v(165.57, 127.52) * mm, "end": v(161.92, 133.67) * mm});
            skArc(sketch, "E795", {"start": v(161.92, 133.67) * mm, "mid": v(156.4, 142.3) * mm, "end": v(150.72, 150.83) * mm});
            skArc(sketch, "E796", {"start": v(150.72, 150.83) * mm, "mid": v(146.85, 156.43) * mm, "end": v(142.9, 161.96) * mm});
            skArc(sketch, "E797", {"start": v(142.9, 161.96) * mm, "mid": v(139.4, 166.62) * mm, "end": v(135.78, 171.18) * mm});
            skArc(sketch, "E798", {"start": v(135.78, 171.18) * mm, "mid": v(132.4, 175.19) * mm, "end": v(128.91, 179.1) * mm});
            skArc(sketch, "E799", {"start": v(128.91, 179.1) * mm, "mid": v(125.43, 182.74) * mm, "end": v(121.82, 186.26) * mm});
            skArc(sketch, "E800", {"start": v(121.82, 186.26) * mm, "mid": v(116.28, 191.51) * mm, "end": v(110.76, 196.8) * mm});
            skArc(sketch, "E801", {"start": v(110.76, 196.8) * mm, "mid": v(108.37, 199.2) * mm, "end": v(106.08, 201.72) * mm});
            skArc(sketch, "E802", {"start": v(106.08, 201.72) * mm, "mid": v(104.7, 203.46) * mm, "end": v(103.5, 205.34) * mm});
            skArc(sketch, "E803", {"start": v(103.5, 205.34) * mm, "mid": v(102.5, 207.3) * mm, "end": v(101.69, 209.35) * mm});
            skArc(sketch, "E804", {"start": v(101.69, 209.35) * mm, "mid": v(101.3, 210.6) * mm, "end": v(100.95, 211.86) * mm});
            skArc(sketch, "E805", {"start": v(100.95, 211.86) * mm, "mid": v(100.57, 213.4) * mm, "end": v(100.22, 214.94) * mm});
            skArc(sketch, "E806", {"start": v(100.22, 214.94) * mm, "mid": v(99.9, 216.5) * mm, "end": v(99.61, 218.07) * mm});
            skArc(sketch, "E807", {"start": v(99.61, 218.07) * mm, "mid": v(99.4, 219.41) * mm, "end": v(99.23, 220.76) * mm});
            skLineSegment(sketch, "E808", {"start": v(99.23, 220.76) * mm, "end": v(98.57, 226.76) * mm});
            skLineSegment(sketch, "E809", {"start": v(98.57, 226.76) * mm, "end": v(96.78, 222.76) * mm});
            skArc(sketch, "E810", {"start": v(48.66, 201.57) * mm, "mid": v(48.77, 201.25) * mm, "end": v(48.86, 200.92) * mm});
            skArc(sketch, "E811", {"start": v(48.86, 200.92) * mm, "mid": v(48.92, 200.61) * mm, "end": v(48.95, 200.3) * mm});
            skArc(sketch, "E812", {"start": v(48.95, 200.3) * mm, "mid": v(48.95, 200.04) * mm, "end": v(48.93, 199.78) * mm});
            skArc(sketch, "E813", {"start": v(48.93, 199.78) * mm, "mid": v(48.88, 199.62) * mm, "end": v(48.78, 199.49) * mm});
            skArc(sketch, "E814", {"start": v(48.78, 199.49) * mm, "mid": v(48.34, 199.3) * mm, "end": v(47.9, 199.47) * mm});
            skArc(sketch, "E815", {"start": v(47.9, 199.47) * mm, "mid": v(46.3, 201) * mm, "end": v(44.75, 202.57) * mm});
            skArc(sketch, "E816", {"start": v(44.75, 202.57) * mm, "mid": v(43.24, 204.15) * mm, "end": v(41.77, 205.77) * mm});
            skArc(sketch, "E817", {"start": v(41.77, 205.77) * mm, "mid": v(41.37, 206.44) * mm, "end": v(41.23, 207.21) * mm});
            skArc(sketch, "E818", {"start": v(41.23, 207.21) * mm, "mid": v(41.45, 207.6) * mm, "end": v(41.9, 207.6) * mm});
            skArc(sketch, "E819", {"start": v(41.9, 207.6) * mm, "mid": v(43.3, 206.7) * mm, "end": v(44.64, 205.73) * mm});
            skArc(sketch, "E820", {"start": v(44.64, 205.73) * mm, "mid": v(46.08, 204.58) * mm, "end": v(47.46, 203.36) * mm});
            skArc(sketch, "E821", {"start": v(47.46, 203.36) * mm, "mid": v(48.16, 202.53) * mm, "end": v(48.66, 201.57) * mm});
            skArc(sketch, "E822", {"start": v(31.23, 46.64) * mm, "mid": v(28.14, 44) * mm, "end": v(25, 41.43) * mm});
            skArc(sketch, "E823", {"start": v(25, 41.43) * mm, "mid": v(22.82, 39.78) * mm, "end": v(20.54, 38.26) * mm});
            skArc(sketch, "E824", {"start": v(20.54, 38.26) * mm, "mid": v(18.42, 37.03) * mm, "end": v(16.21, 35.97) * mm});
            skArc(sketch, "E825", {"start": v(16.21, 35.97) * mm, "mid": v(13.45, 34.81) * mm, "end": v(10.65, 33.77) * mm});
            skLineSegment(sketch, "E826", {"start": v(10.65, 33.77) * mm, "end": v(4.18, 31.51) * mm});
            skLineSegment(sketch, "E827", {"start": v(4.18, 31.51) * mm, "end": v(8.95, 30.31) * mm});
            skArc(sketch, "E828", {"start": v(8.95, 30.31) * mm, "mid": v(15.7, 28.15) * mm, "end": v(22.13, 25.14) * mm});
            skArc(sketch, "E829", {"start": v(22.13, 25.14) * mm, "mid": v(27.28, 21.64) * mm, "end": v(31.68, 17.24) * mm});
            skArc(sketch, "E830", {"start": v(31.68, 17.24) * mm, "mid": v(34.37, 13) * mm, "end": v(35.9, 8.22) * mm});
            skArc(sketch, "E831", {"start": v(35.9, 8.22) * mm, "mid": v(35.9, 3.8) * mm, "end": v(34.33, -0.34) * mm});
            skArc(sketch, "E832", {"start": v(34.33, -0.34) * mm, "mid": v(33.08, -2.04) * mm, "end": v(31.57, -3.51) * mm});
            skArc(sketch, "E833", {"start": v(31.57, -3.51) * mm, "mid": v(29.63, -4.93) * mm, "end": v(27.54, -6.11) * mm});
            skArc(sketch, "E834", {"start": v(27.54, -6.11) * mm, "mid": v(24.33, -7.57) * mm, "end": v(21.03, -8.83) * mm});
            skArc(sketch, "E835", {"start": v(21.03, -8.83) * mm, "mid": v(15.14, -10.82) * mm, "end": v(9.23, -12.74) * mm});
            skArc(sketch, "E836", {"start": v(9.23, -12.74) * mm, "mid": v(5.77, -13.86) * mm, "end": v(2.32, -15.02) * mm});
            skArc(sketch, "E837", {"start": v(2.32, -15.02) * mm, "mid": v(-1.24, -16.28) * mm, "end": v(-4.79, -17.57) * mm});
            skArc(sketch, "E838", {"start": v(-4.79, -17.57) * mm, "mid": v(-7.96, -18.78) * mm, "end": v(-11.12, -20.01) * mm});
            skArc(sketch, "E839", {"start": v(-11.12, -20.01) * mm, "mid": v(-13.23, -20.9) * mm, "end": v(-15.3, -21.87) * mm});
            skArc(sketch, "E840", {"start": v(-15.3, -21.87) * mm, "mid": v(-20.98, -24.9) * mm, "end": v(-26.41, -28.34) * mm});
            skArc(sketch, "E841", {"start": v(-26.41, -28.34) * mm, "mid": v(-31.45, -32.12) * mm, "end": v(-36.18, -36.3) * mm});
            skArc(sketch, "E842", {"start": v(-36.18, -36.3) * mm, "mid": v(-40.16, -40.44) * mm, "end": v(-43.76, -44.92) * mm});
            skArc(sketch, "E843", {"start": v(-43.76, -44.92) * mm, "mid": v(-46.32, -48.99) * mm, "end": v(-48.26, -53.39) * mm});
            skArc(sketch, "E844", {"start": v(-48.26, -53.39) * mm, "mid": v(-48.68, -54.56) * mm, "end": v(-49.13, -55.73) * mm});
            skArc(sketch, "E845", {"start": v(-49.13, -55.73) * mm, "mid": v(-49.74, -57.28) * mm, "end": v(-50.36, -58.83) * mm});
            skArc(sketch, "E846", {"start": v(-50.36, -58.83) * mm, "mid": v(-51.04, -60.48) * mm, "end": v(-51.73, -62.13) * mm});
            skArc(sketch, "E847", {"start": v(-51.73, -62.13) * mm, "mid": v(-52.36, -63.62) * mm, "end": v(-53.01, -65.11) * mm});
            skArc(sketch, "E848", {"start": v(-53.01, -65.11) * mm, "mid": v(-53.93, -67.29) * mm, "end": v(-54.78, -69.48) * mm});
            skArc(sketch, "E849", {"start": v(-54.78, -69.48) * mm, "mid": v(-55.24, -70.95) * mm, "end": v(-55.54, -72.45) * mm});
            skArc(sketch, "E850", {"start": v(-55.54, -72.45) * mm, "mid": v(-55.72, -74.13) * mm, "end": v(-55.75, -75.82) * mm});
            skArc(sketch, "E851", {"start": v(-55.75, -75.82) * mm, "mid": v(-55.66, -78.97) * mm, "end": v(-55.51, -82.11) * mm});
            skArc(sketch, "E852", {"start": v(-55.51, -82.11) * mm, "mid": v(-55.22, -85.9) * mm, "end": v(-54.75, -89.68) * mm});
            skArc(sketch, "E853", {"start": v(-54.75, -89.68) * mm, "mid": v(-54.12, -93.08) * mm, "end": v(-53.29, -96.44) * mm});
            skArc(sketch, "E854", {"start": v(-53.29, -96.44) * mm, "mid": v(-52.4, -99.17) * mm, "end": v(-51.33, -101.83) * mm});
            skArc(sketch, "E855", {"start": v(-51.33, -101.83) * mm, "mid": v(-50.33, -103.55) * mm, "end": v(-49, -105.03) * mm});
            skArc(sketch, "E856", {"start": v(-49, -105.03) * mm, "mid": v(-48.53, -105.4) * mm, "end": v(-48.02, -105.72) * mm});
            skArc(sketch, "E857", {"start": v(-48.02, -105.72) * mm, "mid": v(-47.74, -105.75) * mm, "end": v(-47.52, -105.56) * mm});
            skArc(sketch, "E858", {"start": v(-47.52, -105.56) * mm, "mid": v(-47.36, -105.07) * mm, "end": v(-47.29, -104.57) * mm});
            skArc(sketch, "E859", {"start": v(-47.29, -104.57) * mm, "mid": v(-47.25, -102.89) * mm, "end": v(-47.22, -101.21) * mm});
            skArc(sketch, "E860", {"start": v(-47.22, -101.21) * mm, "mid": v(-47, -98.3) * mm, "end": v(-46.4, -95.43) * mm});
            skArc(sketch, "E861", {"start": v(-46.4, -95.43) * mm, "mid": v(-45.49, -93.68) * mm, "end": v(-43.96, -92.43) * mm});
            skArc(sketch, "E862", {"start": v(-43.96, -92.43) * mm, "mid": v(-42.07, -91.9) * mm, "end": v(-40.11, -92.14) * mm});
            skArc(sketch, "E863", {"start": v(-40.11, -92.14) * mm, "mid": v(-37.41, -93.27) * mm, "end": v(-34.89, -94.75) * mm});
            skArc(sketch, "E864", {"start": v(-34.89, -94.75) * mm, "mid": v(-32.8, -96.05) * mm, "end": v(-30.64, -97.2) * mm});
            skArc(sketch, "E865", {"start": v(-30.64, -97.2) * mm, "mid": v(-28.63, -98.06) * mm, "end": v(-26.54, -98.7) * mm});
            skArc(sketch, "E866", {"start": v(-26.54, -98.7) * mm, "mid": v(-24.17, -99.2) * mm, "end": v(-21.76, -99.49) * mm});
            skArc(sketch, "E867", {"start": v(-21.76, -99.49) * mm, "mid": v(-18.52, -99.68) * mm, "end": v(-15.27, -99.74) * mm});
            skArc(sketch, "E868", {"start": v(-15.27, -99.74) * mm, "mid": v(-10.7, -99.94) * mm, "end": v(-6.15, -100.5) * mm});
            skArc(sketch, "E869", {"start": v(-6.15, -100.5) * mm, "mid": v(-1.84, -101.4) * mm, "end": v(2.37, -102.67) * mm});
            skArc(sketch, "E870", {"start": v(2.37, -102.67) * mm, "mid": v(5.94, -104.13) * mm, "end": v(9.34, -105.94) * mm});
            skArc(sketch, "E871", {"start": v(9.34, -105.94) * mm, "mid": v(11.72, -107.73) * mm, "end": v(13.68, -109.98) * mm});
            skArc(sketch, "E872", {"start": v(13.68, -109.98) * mm, "mid": v(14.41, -111.2) * mm, "end": v(14.95, -112.53) * mm});
            skArc(sketch, "E873", {"start": v(14.95, -112.53) * mm, "mid": v(15.1, -113.59) * mm, "end": v(14.86, -114.63) * mm});
            skArc(sketch, "E874", {"start": v(14.86, -114.63) * mm, "mid": v(14.21, -115.76) * mm, "end": v(13.32, -116.7) * mm});
            skArc(sketch, "E875", {"start": v(13.32, -116.7) * mm, "mid": v(11.56, -118.08) * mm, "end": v(9.73, -119.37) * mm});
            skArc(sketch, "E876", {"start": v(9.73, -119.37) * mm, "mid": v(8.67, -120.08) * mm, "end": v(7.62, -120.81) * mm});
            skArc(sketch, "E877", {"start": v(7.62, -120.81) * mm, "mid": v(6.72, -121.46) * mm, "end": v(5.84, -122.13) * mm});
            skArc(sketch, "E878", {"start": v(5.84, -122.13) * mm, "mid": v(5.12, -122.7) * mm, "end": v(4.4, -123.29) * mm});
            skArc(sketch, "E879", {"start": v(4.4, -123.29) * mm, "mid": v(4.27, -123.45) * mm, "end": v(4.23, -123.66) * mm});
            skArc(sketch, "E880", {"start": v(4.23, -123.66) * mm, "mid": v(4.26, -123.87) * mm, "end": v(4.35, -124.07) * mm});
            skArc(sketch, "E881", {"start": v(4.35, -124.07) * mm, "mid": v(4.85, -124.84) * mm, "end": v(5.35, -125.6) * mm});
            skArc(sketch, "E882", {"start": v(5.35, -125.6) * mm, "mid": v(5.97, -126.5) * mm, "end": v(6.6, -127.4) * mm});
            skArc(sketch, "E883", {"start": v(6.6, -127.4) * mm, "mid": v(7.33, -128.4) * mm, "end": v(8.07, -129.4) * mm});
            skLineSegment(sketch, "E884", {"start": v(8.07, -129.4) * mm, "end": v(11.9, -134.52) * mm});
            skLineSegment(sketch, "E885", {"start": v(11.9, -134.52) * mm, "end": v(17.32, -131.15) * mm});
            skArc(sketch, "E886", {"start": v(17.32, -131.15) * mm, "mid": v(20.85, -129.07) * mm, "end": v(24.47, -127.15) * mm});
            skArc(sketch, "E887", {"start": v(24.47, -127.15) * mm, "mid": v(26.59, -126.4) * mm, "end": v(28.83, -126.2) * mm});
            skArc(sketch, "E888", {"start": v(28.83, -126.2) * mm, "mid": v(30.27, -126.63) * mm, "end": v(31.29, -127.74) * mm});
            skArc(sketch, "E889", {"start": v(31.29, -127.74) * mm, "mid": v(32, -129.62) * mm, "end": v(32.26, -131.61) * mm});
            skLineSegment(sketch, "E890", {"start": v(32.26, -131.61) * mm, "end": v(32.3, -135.24) * mm});
            skLineSegment(sketch, "E891", {"start": v(32.3, -135.24) * mm, "end": v(34.35, -132.76) * mm});
            skArc(sketch, "E892", {"start": v(34.35, -132.76) * mm, "mid": v(34.94, -131.96) * mm, "end": v(35.43, -131.1) * mm});
            skArc(sketch, "E893", {"start": v(35.43, -131.1) * mm, "mid": v(35.77, -130.22) * mm, "end": v(35.99, -129.31) * mm});
            skArc(sketch, "E894", {"start": v(35.99, -129.31) * mm, "mid": v(36.14, -128.05) * mm, "end": v(36.18, -126.79) * mm});
            skArc(sketch, "E895", {"start": v(36.18, -126.79) * mm, "mid": v(36.14, -124.52) * mm, "end": v(36.06, -122.26) * mm});
            skArc(sketch, "E896", {"start": v(36.06, -122.26) * mm, "mid": v(35.78, -118.82) * mm, "end": v(35.24, -115.4) * mm});
            skArc(sketch, "E897", {"start": v(35.24, -115.4) * mm, "mid": v(34.5, -112.5) * mm, "end": v(33.44, -109.7) * mm});
            skArc(sketch, "E898", {"start": v(33.44, -109.7) * mm, "mid": v(32.06, -107.02) * mm, "end": v(30.39, -104.5) * mm});
            skArc(sketch, "E899", {"start": v(30.39, -104.5) * mm, "mid": v(28.18, -101.78) * mm, "end": v(25.78, -99.22) * mm});
            skArc(sketch, "E900", {"start": v(25.78, -99.22) * mm, "mid": v(22.44, -96.2) * mm, "end": v(18.83, -93.51) * mm});
            skArc(sketch, "E901", {"start": v(18.83, -93.51) * mm, "mid": v(14.92, -91.12) * mm, "end": v(10.81, -89.09) * mm});
            skArc(sketch, "E902", {"start": v(10.81, -89.09) * mm, "mid": v(5.7, -87.05) * mm, "end": v(0.44, -85.36) * mm});
            skArc(sketch, "E903", {"start": v(0.44, -85.36) * mm, "mid": v(-6.73, -83.45) * mm, "end": v(-13.95, -81.74) * mm});
            skArc(sketch, "E904", {"start": v(-13.95, -81.74) * mm, "mid": v(-17.64, -80.84) * mm, "end": v(-21.29, -79.77) * mm});
            skArc(sketch, "E905", {"start": v(-21.29, -79.77) * mm, "mid": v(-23.55, -78.84) * mm, "end": v(-25.63, -77.56) * mm});
            skArc(sketch, "E906", {"start": v(-25.63, -77.56) * mm, "mid": v(-26.97, -76.3) * mm, "end": v(-27.95, -74.72) * mm});
            skArc(sketch, "E907", {"start": v(-27.95, -74.72) * mm, "mid": v(-28.56, -72.87) * mm, "end": v(-28.77, -70.92) * mm});
            skArc(sketch, "E908", {"start": v(-28.77, -70.92) * mm, "mid": v(-27.81, -65.11) * mm, "end": v(-25.04, -59.93) * mm});
            skArc(sketch, "E909", {"start": v(-25.04, -59.93) * mm, "mid": v(-19.72, -53.9) * mm, "end": v(-13.65, -48.62) * mm});
            skArc(sketch, "E910", {"start": v(-13.65, -48.62) * mm, "mid": v(-5.47, -43.1) * mm, "end": v(3.26, -38.53) * mm});
            skArc(sketch, "E911", {"start": v(3.26, -38.53) * mm, "mid": v(13.34, -34.42) * mm, "end": v(23.73, -31.14) * mm});
            skArc(sketch, "E912", {"start": v(23.73, -31.14) * mm, "mid": v(27.44, -30.21) * mm, "end": v(31.18, -29.42) * mm});
            skArc(sketch, "E913", {"start": v(31.18, -29.42) * mm, "mid": v(34.98, -28.77) * mm, "end": v(38.8, -28.25) * mm});
            skArc(sketch, "E914", {"start": v(38.8, -28.25) * mm, "mid": v(42.16, -27.92) * mm, "end": v(45.52, -27.7) * mm});
            skArc(sketch, "E915", {"start": v(45.52, -27.7) * mm, "mid": v(47.57, -27.76) * mm, "end": v(49.6, -28.12) * mm});
            skArc(sketch, "E916", {"start": v(49.6, -28.12) * mm, "mid": v(50.78, -28.58) * mm, "end": v(51.8, -29.34) * mm});
            skArc(sketch, "E917", {"start": v(51.8, -29.34) * mm, "mid": v(52.84, -30.5) * mm, "end": v(53.7, -31.8) * mm});
            skArc(sketch, "E918", {"start": v(53.7, -31.8) * mm, "mid": v(54.38, -33.26) * mm, "end": v(54.86, -34.8) * mm});
            skArc(sketch, "E919", {"start": v(54.86, -34.8) * mm, "mid": v(55.03, -36.2) * mm, "end": v(54.92, -37.62) * mm});
            skArc(sketch, "E920", {"start": v(54.92, -37.62) * mm, "mid": v(54.78, -38.4) * mm, "end": v(54.67, -39.2) * mm});
            skArc(sketch, "E921", {"start": v(54.67, -39.2) * mm, "mid": v(54.73, -39.36) * mm, "end": v(54.9, -39.39) * mm});
            skArc(sketch, "E922", {"start": v(54.9, -39.39) * mm, "mid": v(55.18, -39.24) * mm, "end": v(55.4, -39.04) * mm});
            skArc(sketch, "E923", {"start": v(55.4, -39.04) * mm, "mid": v(56.4, -37.89) * mm, "end": v(57.36, -36.74) * mm});
            skArc(sketch, "E924", {"start": v(57.36, -36.74) * mm, "mid": v(59.17, -34.27) * mm, "end": v(60.62, -31.58) * mm});
            skArc(sketch, "E925", {"start": v(60.62, -31.58) * mm, "mid": v(61.91, -28.34) * mm, "end": v(62.9, -25) * mm});
            skArc(sketch, "E926", {"start": v(62.9, -25) * mm, "mid": v(63.74, -20.98) * mm, "end": v(64.26, -16.91) * mm});
            skArc(sketch, "E927", {"start": v(64.26, -16.91) * mm, "mid": v(64.58, -12.08) * mm, "end": v(64.68, -7.24) * mm});
            skArc(sketch, "E928", {"start": v(64.68, -7.24) * mm, "mid": v(64.52, -1.64) * mm, "end": v(64.11, 3.95) * mm});
            skArc(sketch, "E929", {"start": v(64.11, 3.95) * mm, "mid": v(63.46, 9.08) * mm, "end": v(62.52, 14.15) * mm});
            skArc(sketch, "E930", {"start": v(62.52, 14.15) * mm, "mid": v(61.32, 18.94) * mm, "end": v(59.82, 23.65) * mm});
            skArc(sketch, "E931", {"start": v(59.82, 23.65) * mm, "mid": v(58.04, 28.27) * mm, "end": v(55.97, 32.76) * mm});
            skArc(sketch, "E932", {"start": v(55.97, 32.76) * mm, "mid": v(54.16, 36.12) * mm, "end": v(52.14, 39.35) * mm});
            skArc(sketch, "E933", {"start": v(52.14, 39.35) * mm, "mid": v(49.66, 42.87) * mm, "end": v(47.01, 46.27) * mm});
            skArc(sketch, "E934", {"start": v(47.01, 46.27) * mm, "mid": v(44.48, 49.29) * mm, "end": v(41.85, 52.23) * mm});
            skArc(sketch, "E935", {"start": v(41.85, 52.23) * mm, "mid": v(40.7, 53) * mm, "end": v(39.34, 53.22) * mm});
            skArc(sketch, "E936", {"start": v(39.34, 53.22) * mm, "mid": v(39.12, 53.17) * mm, "end": v(38.93, 53.05) * mm});
            skArc(sketch, "E937", {"start": v(38.93, 53.05) * mm, "mid": v(37.81, 52.16) * mm, "end": v(36.7, 51.27) * mm});
            skArc(sketch, "E938", {"start": v(36.7, 51.27) * mm, "mid": v(35.42, 50.21) * mm, "end": v(34.14, 49.15) * mm});
            skArc(sketch, "E939", {"start": v(34.14, 49.15) * mm, "mid": v(32.68, 47.9) * mm, "end": v(31.23, 46.64) * mm});
            skArc(sketch, "E940", {"start": v(33.73, -30.82) * mm, "mid": v(32.74, -31.04) * mm, "end": v(31.76, -31.27) * mm});
            skArc(sketch, "E941", {"start": v(31.76, -31.27) * mm, "mid": v(30.42, -31.59) * mm, "end": v(29.07, -31.91) * mm});
            skArc(sketch, "E942", {"start": v(29.07, -31.91) * mm, "mid": v(27.63, -32.27) * mm, "end": v(26.18, -32.63) * mm});
            skArc(sketch, "E943", {"start": v(26.18, -32.63) * mm, "mid": v(24.84, -32.97) * mm, "end": v(23.5, -33.32) * mm});
            skLineSegment(sketch, "E944", {"start": v(23.5, -33.32) * mm, "end": v(17.28, -34.94) * mm});
            skLineSegment(sketch, "E945", {"start": v(17.28, -34.94) * mm, "end": v(19.73, -38.15) * mm});
            skArc(sketch, "E946", {"start": v(19.73, -38.15) * mm, "mid": v(21.28, -40.38) * mm, "end": v(22.63, -42.73) * mm});
            skArc(sketch, "E947", {"start": v(22.63, -42.73) * mm, "mid": v(24.69, -46.82) * mm, "end": v(26.67, -50.96) * mm});
            skArc(sketch, "E948", {"start": v(26.67, -50.96) * mm, "mid": v(28.56, -55.1) * mm, "end": v(30.37, -59.3) * mm});
            skArc(sketch, "E949", {"start": v(30.37, -59.3) * mm, "mid": v(31.18, -61.56) * mm, "end": v(31.75, -63.9) * mm});
            skArc(sketch, "E950", {"start": v(31.75, -63.9) * mm, "mid": v(31.87, -64.68) * mm, "end": v(31.95, -65.46) * mm});
            skArc(sketch, "E951", {"start": v(31.95, -65.46) * mm, "mid": v(32, -66.28) * mm, "end": v(32.02, -67.1) * mm});
            skArc(sketch, "E952", {"start": v(32.02, -67.1) * mm, "mid": v(32, -67.86) * mm, "end": v(31.96, -68.6) * mm});
            skArc(sketch, "E953", {"start": v(31.96, -68.6) * mm, "mid": v(31.88, -69.14) * mm, "end": v(31.75, -69.67) * mm});
            skArc(sketch, "E954", {"start": v(31.75, -69.67) * mm, "mid": v(31.52, -70.23) * mm, "end": v(31.22, -70.76) * mm});
            skArc(sketch, "E955", {"start": v(31.22, -70.76) * mm, "mid": v(30.95, -70.97) * mm, "end": v(30.6, -70.98) * mm});
            skArc(sketch, "E956", {"start": v(30.6, -70.98) * mm, "mid": v(30.08, -70.77) * mm, "end": v(29.6, -70.46) * mm});
            skArc(sketch, "E957", {"start": v(29.6, -70.46) * mm, "mid": v(28.29, -69.37) * mm, "end": v(26.98, -68.26) * mm});
            skArc(sketch, "E958", {"start": v(26.98, -68.26) * mm, "mid": v(21.7, -64.5) * mm, "end": v(15.82, -61.72) * mm});
            skArc(sketch, "E959", {"start": v(15.82, -61.72) * mm, "mid": v(10.05, -60.33) * mm, "end": v(4.11, -60.3) * mm});
            skArc(sketch, "E960", {"start": v(4.11, -60.3) * mm, "mid": v(-1.74, -61.63) * mm, "end": v(-7.14, -64.25) * mm});
            skArc(sketch, "E961", {"start": v(-7.14, -64.25) * mm, "mid": v(-12.44, -68.27) * mm, "end": v(-16.98, -73.12) * mm});
            skLineSegment(sketch, "E962", {"start": v(-16.98, -73.12) * mm, "end": v(-20.96, -78.15) * mm});
            skLineSegment(sketch, "E963", {"start": v(-20.96, -78.15) * mm, "end": v(-17.61, -79.3) * mm});
            skArc(sketch, "E964", {"start": v(-17.61, -79.3) * mm, "mid": v(-14.74, -80.2) * mm, "end": v(-11.83, -80.95) * mm});
            skArc(sketch, "E965", {"start": v(-11.83, -80.95) * mm, "mid": v(-8.92, -81.54) * mm, "end": v(-5.98, -81.98) * mm});
            skArc(sketch, "E966", {"start": v(-5.98, -81.98) * mm, "mid": v(-3.43, -82.22) * mm, "end": v(-0.87, -82.32) * mm});
            skArc(sketch, "E967", {"start": v(-0.87, -82.32) * mm, "mid": v(0.73, -82.18) * mm, "end": v(2.28, -81.72) * mm});
            skArc(sketch, "E968", {"start": v(2.28, -81.72) * mm, "mid": v(5.17, -80.81) * mm, "end": v(8.19, -80.44) * mm});
            skArc(sketch, "E969", {"start": v(8.19, -80.44) * mm, "mid": v(11.18, -80.62) * mm, "end": v(14.1, -81.35) * mm});
            skArc(sketch, "E970", {"start": v(14.1, -81.35) * mm, "mid": v(17.3, -82.76) * mm, "end": v(20.27, -84.63) * mm});
            skArc(sketch, "E971", {"start": v(20.27, -84.63) * mm, "mid": v(23.74, -87.41) * mm, "end": v(27, -90.44) * mm});
            skArc(sketch, "E972", {"start": v(27, -90.44) * mm, "mid": v(28.65, -92.05) * mm, "end": v(30.34, -93.62) * mm});
            skArc(sketch, "E973", {"start": v(30.34, -93.62) * mm, "mid": v(31.53, -94.63) * mm, "end": v(32.8, -95.56) * mm});
            skArc(sketch, "E974", {"start": v(32.8, -95.56) * mm, "mid": v(33.85, -96.2) * mm, "end": v(34.96, -96.72) * mm});
            skArc(sketch, "E975", {"start": v(34.96, -96.72) * mm, "mid": v(36.07, -97.1) * mm, "end": v(37.21, -97.35) * mm});
            skArc(sketch, "E976", {"start": v(37.21, -97.35) * mm, "mid": v(38.94, -97.73) * mm, "end": v(40.62, -98.3) * mm});
            skArc(sketch, "E977", {"start": v(40.62, -98.3) * mm, "mid": v(41.82, -98.98) * mm, "end": v(42.83, -99.91) * mm});
            skArc(sketch, "E978", {"start": v(42.83, -99.91) * mm, "mid": v(43.53, -101) * mm, "end": v(43.9, -102.22) * mm});
            skArc(sketch, "E979", {"start": v(43.9, -102.22) * mm, "mid": v(44.04, -103.73) * mm, "end": v(43.92, -105.24) * mm});
            skLineSegment(sketch, "E980", {"start": v(43.92, -105.24) * mm, "end": v(43.34, -108.8) * mm});
            skLineSegment(sketch, "E981", {"start": v(43.34, -108.8) * mm, "end": v(46.21, -106.75) * mm});
            skArc(sketch, "E982", {"start": v(46.21, -106.75) * mm, "mid": v(50.85, -102.11) * mm, "end": v(53.72, -96.22) * mm});
            skArc(sketch, "E983", {"start": v(53.72, -96.22) * mm, "mid": v(55.56, -87.73) * mm, "end": v(56.13, -79.07) * mm});
            skArc(sketch, "E984", {"start": v(56.13, -79.07) * mm, "mid": v(55.41, -68.36) * mm, "end": v(53.43, -57.8) * mm});
            skArc(sketch, "E985", {"start": v(53.43, -57.8) * mm, "mid": v(50, -46.23) * mm, "end": v(45.64, -34.99) * mm});
            skArc(sketch, "E986", {"start": v(45.64, -34.99) * mm, "mid": v(44.77, -33.2) * mm, "end": v(43.76, -31.48) * mm});
            skArc(sketch, "E987", {"start": v(43.76, -31.48) * mm, "mid": v(42.98, -30.6) * mm, "end": v(41.94, -30.04) * mm});
            skArc(sketch, "E988", {"start": v(41.94, -30.04) * mm, "mid": v(40.63, -29.75) * mm, "end": v(39.28, -29.79) * mm});
            skArc(sketch, "E989", {"start": v(39.28, -29.79) * mm, "mid": v(36.5, -30.26) * mm, "end": v(33.73, -30.82) * mm});
            skArc(sketch, "E990", {"start": v(-31.63, -105.08) * mm, "mid": v(-32.64, -107.8) * mm, "end": v(-33.55, -110.57) * mm});
            skArc(sketch, "E991", {"start": v(-33.55, -110.57) * mm, "mid": v(-34.05, -112.51) * mm, "end": v(-34.34, -114.5) * mm});
            skArc(sketch, "E992", {"start": v(-34.34, -114.5) * mm, "mid": v(-34.39, -116.28) * mm, "end": v(-34.22, -118.06) * mm});
            skArc(sketch, "E993", {"start": v(-34.22, -118.06) * mm, "mid": v(-33.8, -120.17) * mm, "end": v(-33.23, -122.25) * mm});
            skArc(sketch, "E994", {"start": v(-33.23, -122.25) * mm, "mid": v(-32.56, -124.2) * mm, "end": v(-31.8, -126.13) * mm});
            skArc(sketch, "E995", {"start": v(-31.8, -126.13) * mm, "mid": v(-31.13, -127.45) * mm, "end": v(-30.3, -128.67) * mm});
            skArc(sketch, "E996", {"start": v(-30.3, -128.67) * mm, "mid": v(-29.86, -128.95) * mm, "end": v(-29.35, -128.9) * mm});
            skArc(sketch, "E997", {"start": v(-29.35, -128.9) * mm, "mid": v(-28.93, -128.52) * mm, "end": v(-28.77, -127.98) * mm});
            skArc(sketch, "E998", {"start": v(-28.77, -127.98) * mm, "mid": v(-28.64, -126.76) * mm, "end": v(-28.23, -125.59) * mm});
            skArc(sketch, "E999", {"start": v(-28.23, -125.59) * mm, "mid": v(-27.63, -124.84) * mm, "end": v(-26.76, -124.43) * mm});
            skArc(sketch, "E1000", {"start": v(-26.76, -124.43) * mm, "mid": v(-25.47, -124.34) * mm, "end": v(-24.2, -124.58) * mm});
            skArc(sketch, "E1001", {"start": v(-24.2, -124.58) * mm, "mid": v(-22.21, -125.32) * mm, "end": v(-20.28, -126.2) * mm});
            skArc(sketch, "E1002", {"start": v(-20.28, -126.2) * mm, "mid": v(-15.15, -129.12) * mm, "end": v(-10.44, -132.69) * mm});
            skArc(sketch, "E1003", {"start": v(-10.44, -132.69) * mm, "mid": v(-6, -136.98) * mm, "end": v(-2.07, -141.74) * mm});
            skArc(sketch, "E1004", {"start": v(-2.07, -141.74) * mm, "mid": v(1.22, -146.8) * mm, "end": v(3.91, -152.21) * mm});
            skArc(sketch, "E1005", {"start": v(3.91, -152.21) * mm, "mid": v(5.7, -157.46) * mm, "end": v(6.71, -162.91) * mm});
            skLineSegment(sketch, "E1006", {"start": v(6.71, -162.91) * mm, "end": v(7.28, -168.24) * mm});
            skLineSegment(sketch, "E1007", {"start": v(7.28, -168.24) * mm, "end": v(4.92, -163.24) * mm});
            skArc(sketch, "E1008", {"start": v(4.92, -163.24) * mm, "mid": v(3.46, -160.24) * mm, "end": v(1.94, -157.27) * mm});
            skArc(sketch, "E1009", {"start": v(1.94, -157.27) * mm, "mid": v(1.38, -156.83) * mm, "end": v(0.68, -156.94) * mm});
            skArc(sketch, "E1010", {"start": v(0.68, -156.94) * mm, "mid": v(0.07, -157.6) * mm, "end": v(-0.18, -158.46) * mm});
            skArc(sketch, "E1011", {"start": v(-0.18, -158.46) * mm, "mid": v(-0.26, -162.52) * mm, "end": v(-0.3, -166.57) * mm});
            skArc(sketch, "E1012", {"start": v(-0.3, -166.57) * mm, "mid": v(-0.33, -169.52) * mm, "end": v(-0.43, -172.46) * mm});
            skArc(sketch, "E1013", {"start": v(-0.43, -172.46) * mm, "mid": v(-0.58, -174.7) * mm, "end": v(-0.84, -176.9) * mm});
            skArc(sketch, "E1014", {"start": v(-0.84, -176.9) * mm, "mid": v(-1.19, -179.02) * mm, "end": v(-1.65, -181.11) * mm});
            skArc(sketch, "E1015", {"start": v(-1.65, -181.11) * mm, "mid": v(-2.3, -183.66) * mm, "end": v(-3.04, -186.2) * mm});
            skArc(sketch, "E1016", {"start": v(-3.04, -186.2) * mm, "mid": v(-3.93, -189.34) * mm, "end": v(-4.7, -192.51) * mm});
            skArc(sketch, "E1017", {"start": v(-4.7, -192.51) * mm, "mid": v(-5.24, -195.37) * mm, "end": v(-5.63, -198.26) * mm});
            skArc(sketch, "E1018", {"start": v(-5.63, -198.26) * mm, "mid": v(-5.8, -200.5) * mm, "end": v(-5.86, -202.76) * mm});
            skArc(sketch, "E1019", {"start": v(-5.86, -202.76) * mm, "mid": v(-5.58, -203.45) * mm, "end": v(-4.88, -203.74) * mm});
            skArc(sketch, "E1020", {"start": v(-4.88, -203.74) * mm, "mid": v(-4.67, -203.7) * mm, "end": v(-4.5, -203.57) * mm});
            skArc(sketch, "E1021", {"start": v(-4.5, -203.57) * mm, "mid": v(-4.27, -203.3) * mm, "end": v(-4.07, -203) * mm});
            skArc(sketch, "E1022", {"start": v(-4.07, -203) * mm, "mid": v(-3.85, -202.61) * mm, "end": v(-3.67, -202.2) * mm});
            skArc(sketch, "E1023", {"start": v(-3.67, -202.2) * mm, "mid": v(-3.5, -201.73) * mm, "end": v(-3.37, -201.25) * mm});
            skArc(sketch, "E1024", {"start": v(-3.37, -201.25) * mm, "mid": v(-3.11, -200.52) * mm, "end": v(-2.73, -199.85) * mm});
            skArc(sketch, "E1025", {"start": v(-2.73, -199.85) * mm, "mid": v(-1.74, -198.45) * mm, "end": v(-0.72, -197.07) * mm});
            skArc(sketch, "E1026", {"start": v(-0.72, -197.07) * mm, "mid": v(0.55, -195.44) * mm, "end": v(1.86, -193.85) * mm});
            skArc(sketch, "E1027", {"start": v(1.86, -193.85) * mm, "mid": v(3.3, -192.16) * mm, "end": v(4.78, -190.5) * mm});
            skArc(sketch, "E1028", {"start": v(4.78, -190.5) * mm, "mid": v(8.96, -185.68) * mm, "end": v(12.9, -180.67) * mm});
            skArc(sketch, "E1029", {"start": v(12.9, -180.67) * mm, "mid": v(15.33, -176.9) * mm, "end": v(17.23, -172.83) * mm});
            skArc(sketch, "E1030", {"start": v(17.23, -172.83) * mm, "mid": v(18.35, -169.02) * mm, "end": v(18.83, -165.07) * mm});
            skArc(sketch, "E1031", {"start": v(18.83, -165.07) * mm, "mid": v(18.77, -160.4) * mm, "end": v(18.23, -155.77) * mm});
            skArc(sketch, "E1032", {"start": v(18.23, -155.77) * mm, "mid": v(16.88, -150.03) * mm, "end": v(14.8, -144.52) * mm});
            skArc(sketch, "E1033", {"start": v(14.8, -144.52) * mm, "mid": v(11.8, -138.54) * mm, "end": v(8.26, -132.86) * mm});
            skArc(sketch, "E1034", {"start": v(8.26, -132.86) * mm, "mid": v(4.36, -127.67) * mm, "end": v(0.02, -122.84) * mm});
            skArc(sketch, "E1035", {"start": v(0.02, -122.84) * mm, "mid": v(-3.99, -119.4) * mm, "end": v(-8.5, -116.64) * mm});
            skArc(sketch, "E1036", {"start": v(-8.5, -116.64) * mm, "mid": v(-9.44, -116.15) * mm, "end": v(-10.38, -115.66) * mm});
            skArc(sketch, "E1037", {"start": v(-10.38, -115.66) * mm, "mid": v(-11.22, -115.18) * mm, "end": v(-12.06, -114.7) * mm});
            skArc(sketch, "E1038", {"start": v(-12.06, -114.7) * mm, "mid": v(-12.74, -114.27) * mm, "end": v(-13.42, -113.84) * mm});
            skArc(sketch, "E1039", {"start": v(-13.42, -113.84) * mm, "mid": v(-13.68, -113.63) * mm, "end": v(-13.9, -113.39) * mm});
            skArc(sketch, "E1040", {"start": v(-13.9, -113.39) * mm, "mid": v(-14.11, -112.95) * mm, "end": v(-14.16, -112.46) * mm});
            skArc(sketch, "E1041", {"start": v(-14.16, -112.46) * mm, "mid": v(-14.07, -111.48) * mm, "end": v(-13.92, -110.51) * mm});
            skArc(sketch, "E1042", {"start": v(-13.92, -110.51) * mm, "mid": v(-13.64, -109.14) * mm, "end": v(-13.3, -107.77) * mm});
            skArc(sketch, "E1043", {"start": v(-13.3, -107.77) * mm, "mid": v(-12.78, -105.88) * mm, "end": v(-12.23, -103.99) * mm});
            skArc(sketch, "E1044", {"start": v(-12.23, -103.99) * mm, "mid": v(-12.08, -103.35) * mm, "end": v(-12.04, -102.7) * mm});
            skArc(sketch, "E1045", {"start": v(-12.04, -102.7) * mm, "mid": v(-12.16, -102.31) * mm, "end": v(-12.46, -102.05) * mm});
            skArc(sketch, "E1046", {"start": v(-12.46, -102.05) * mm, "mid": v(-13.07, -101.86) * mm, "end": v(-13.7, -101.78) * mm});
            skArc(sketch, "E1047", {"start": v(-13.7, -101.78) * mm, "mid": v(-15.55, -101.75) * mm, "end": v(-17.41, -101.74) * mm});
            skArc(sketch, "E1048", {"start": v(-17.41, -101.74) * mm, "mid": v(-18.66, -101.72) * mm, "end": v(-19.9, -101.67) * mm});
            skArc(sketch, "E1049", {"start": v(-19.9, -101.67) * mm, "mid": v(-21.2, -101.59) * mm, "end": v(-22.5, -101.47) * mm});
            skArc(sketch, "E1050", {"start": v(-22.5, -101.47) * mm, "mid": v(-23.67, -101.34) * mm, "end": v(-24.84, -101.18) * mm});
            skArc(sketch, "E1051", {"start": v(-24.84, -101.18) * mm, "mid": v(-25.65, -101.03) * mm, "end": v(-26.45, -100.83) * mm});
            skArc(sketch, "E1052", {"start": v(-26.45, -100.83) * mm, "mid": v(-27.44, -100.59) * mm, "end": v(-28.44, -100.42) * mm});
            skArc(sketch, "E1053", {"start": v(-28.44, -100.42) * mm, "mid": v(-28.99, -100.46) * mm, "end": v(-29.47, -100.71) * mm});
            skArc(sketch, "E1054", {"start": v(-29.47, -100.71) * mm, "mid": v(-29.93, -101.2) * mm, "end": v(-30.27, -101.77) * mm});
            skArc(sketch, "E1055", {"start": v(-30.27, -101.77) * mm, "mid": v(-30.97, -103.42) * mm, "end": v(-31.63, -105.08) * mm});
            skArc(sketch, "E1056", {"start": v(-11.3, -138.8) * mm, "mid": v(-12.11, -139.96) * mm, "end": v(-12.96, -141.09) * mm});
            skArc(sketch, "E1057", {"start": v(-12.96, -141.09) * mm, "mid": v(-13.38, -141.43) * mm, "end": v(-13.9, -141.58) * mm});
            skArc(sketch, "E1058", {"start": v(-13.9, -141.58) * mm, "mid": v(-14.32, -141.45) * mm, "end": v(-14.57, -141.09) * mm});
            skArc(sketch, "E1059", {"start": v(-14.57, -141.09) * mm, "mid": v(-14.8, -140.05) * mm, "end": v(-14.97, -138.99) * mm});
            skLineSegment(sketch, "E1060", {"start": v(-14.97, -138.99) * mm, "end": v(-15.3, -136.24) * mm});
            skLineSegment(sketch, "E1061", {"start": v(-15.3, -136.24) * mm, "end": v(-17.19, -139.73) * mm});
            skArc(sketch, "E1062", {"start": v(-17.19, -139.73) * mm, "mid": v(-18.62, -143.13) * mm, "end": v(-19.36, -146.74) * mm});
            skArc(sketch, "E1063", {"start": v(-19.36, -146.74) * mm, "mid": v(-19.6, -151.29) * mm, "end": v(-19.38, -155.84) * mm});
            skArc(sketch, "E1064", {"start": v(-19.38, -155.84) * mm, "mid": v(-18.63, -160.8) * mm, "end": v(-17.4, -165.67) * mm});
            skArc(sketch, "E1065", {"start": v(-17.4, -165.67) * mm, "mid": v(-15.72, -170.4) * mm, "end": v(-13.58, -174.93) * mm});
            skArc(sketch, "E1066", {"start": v(-13.58, -174.93) * mm, "mid": v(-12.42, -177) * mm, "end": v(-11.15, -179.02) * mm});
            skArc(sketch, "E1067", {"start": v(-11.15, -179.02) * mm, "mid": v(-9.94, -180.73) * mm, "end": v(-8.62, -182.35) * mm});
            skArc(sketch, "E1068", {"start": v(-8.62, -182.35) * mm, "mid": v(-8.15, -182.7) * mm, "end": v(-7.58, -182.82) * mm});
            skArc(sketch, "E1069", {"start": v(-7.58, -182.82) * mm, "mid": v(-7.23, -182.63) * mm, "end": v(-7.18, -182.24) * mm});
            skArc(sketch, "E1070", {"start": v(-7.18, -182.24) * mm, "mid": v(-7.8, -180.38) * mm, "end": v(-8.24, -178.47) * mm});
            skArc(sketch, "E1071", {"start": v(-8.24, -178.47) * mm, "mid": v(-8.62, -176.15) * mm, "end": v(-8.89, -173.82) * mm});
            skArc(sketch, "E1072", {"start": v(-8.89, -173.82) * mm, "mid": v(-9.04, -171.47) * mm, "end": v(-9.07, -169.12) * mm});
            skArc(sketch, "E1073", {"start": v(-9.07, -169.12) * mm, "mid": v(-8.97, -167.15) * mm, "end": v(-8.7, -165.2) * mm});
            skArc(sketch, "E1074", {"start": v(-8.7, -165.2) * mm, "mid": v(-8.44, -164) * mm, "end": v(-8.1, -162.8) * mm});
            skArc(sketch, "E1075", {"start": v(-8.1, -162.8) * mm, "mid": v(-7.57, -161.18) * mm, "end": v(-7, -159.58) * mm});
            skArc(sketch, "E1076", {"start": v(-7, -159.58) * mm, "mid": v(-6.33, -157.86) * mm, "end": v(-5.62, -156.15) * mm});
            skArc(sketch, "E1077", {"start": v(-5.62, -156.15) * mm, "mid": v(-4.92, -154.58) * mm, "end": v(-4.17, -153.03) * mm});
            skLineSegment(sketch, "E1078", {"start": v(-4.17, -153.03) * mm, "end": v(-0.54, -145.82) * mm});
            skLineSegment(sketch, "E1079", {"start": v(-0.54, -145.82) * mm, "end": v(-3.62, -141.93) * mm});
            skArc(sketch, "E1080", {"start": v(-3.62, -141.93) * mm, "mid": v(-5.27, -139.89) * mm, "end": v(-6.95, -137.87) * mm});
            skArc(sketch, "E1081", {"start": v(-6.95, -137.87) * mm, "mid": v(-7.65, -137.23) * mm, "end": v(-8.49, -136.76) * mm});
            skArc(sketch, "E1082", {"start": v(-8.49, -136.76) * mm, "mid": v(-9.16, -136.7) * mm, "end": v(-9.76, -136.99) * mm});
            skArc(sketch, "E1083", {"start": v(-9.76, -136.99) * mm, "mid": v(-10.58, -137.84) * mm, "end": v(-11.3, -138.8) * mm});
            skArc(sketch, "E1084", {"start": v(-66.78, -219.74) * mm, "mid": v(-66.82, -220.28) * mm, "end": v(-66.86, -220.82) * mm});
            skArc(sketch, "E1085", {"start": v(-66.86, -220.82) * mm, "mid": v(-66.92, -221.42) * mm, "end": v(-66.98, -222.02) * mm});
            skArc(sketch, "E1086", {"start": v(-66.98, -222.02) * mm, "mid": v(-67.05, -222.58) * mm, "end": v(-67.12, -223.14) * mm});
            skArc(sketch, "E1087", {"start": v(-67.12, -223.14) * mm, "mid": v(-67.19, -223.56) * mm, "end": v(-67.26, -223.98) * mm});
            skArc(sketch, "E1088", {"start": v(-67.26, -223.98) * mm, "mid": v(-67.31, -224.33) * mm, "end": v(-67.33, -224.69) * mm});
            skArc(sketch, "E1089", {"start": v(-67.33, -224.69) * mm, "mid": v(-67.31, -225.03) * mm, "end": v(-67.26, -225.36) * mm});
            skArc(sketch, "E1090", {"start": v(-67.26, -225.36) * mm, "mid": v(-67.19, -225.64) * mm, "end": v(-67.08, -225.9) * mm});
            skArc(sketch, "E1091", {"start": v(-67.08, -225.9) * mm, "mid": v(-66.96, -226.09) * mm, "end": v(-66.8, -226.22) * mm});
            skArc(sketch, "E1092", {"start": v(-66.8, -226.22) * mm, "mid": v(-66.37, -226.27) * mm, "end": v(-66.07, -225.95) * mm});
            skArc(sketch, "E1093", {"start": v(-66.07, -225.95) * mm, "mid": v(-65.78, -224.88) * mm, "end": v(-65.6, -223.79) * mm});
            skArc(sketch, "E1094", {"start": v(-65.6, -223.79) * mm, "mid": v(-65.48, -222.46) * mm, "end": v(-65.47, -221.14) * mm});
            skArc(sketch, "E1095", {"start": v(-65.47, -221.14) * mm, "mid": v(-65.6, -220.1) * mm, "end": v(-65.9, -219.12) * mm});
            skArc(sketch, "E1096", {"start": v(-65.9, -219.12) * mm, "mid": v(-66.1, -218.6) * mm, "end": v(-66.33, -218.07) * mm});
            skArc(sketch, "E1097", {"start": v(-66.33, -218.07) * mm, "mid": v(-66.42, -218) * mm, "end": v(-66.53, -218.02) * mm});
            skArc(sketch, "E1098", {"start": v(-66.53, -218.02) * mm, "mid": v(-66.63, -218.13) * mm, "end": v(-66.68, -218.28) * mm});
            skArc(sketch, "E1099", {"start": v(-66.68, -218.28) * mm, "mid": v(-66.73, -219) * mm, "end": v(-66.78, -219.74) * mm});
            skArc(sketch, "E1100", {"start": v(-10.6, -222.24) * mm, "mid": v(-10.62, -223.54) * mm, "end": v(-10.62, -224.83) * mm});
            skArc(sketch, "E1101", {"start": v(-10.62, -224.83) * mm, "mid": v(-10.59, -225.35) * mm, "end": v(-10.47, -225.85) * mm});
            skArc(sketch, "E1102", {"start": v(-10.47, -225.85) * mm, "mid": v(-10.34, -226) * mm, "end": v(-10.15, -225.96) * mm});
            skArc(sketch, "E1103", {"start": v(-10.15, -225.96) * mm, "mid": v(-9.87, -225.72) * mm, "end": v(-9.66, -225.42) * mm});
            skArc(sketch, "E1104", {"start": v(-9.66, -225.42) * mm, "mid": v(-9.32, -224.86) * mm, "end": v(-8.96, -224.31) * mm});
            skArc(sketch, "E1105", {"start": v(-8.96, -224.31) * mm, "mid": v(-8.78, -224.15) * mm, "end": v(-8.55, -224.1) * mm});
            skArc(sketch, "E1106", {"start": v(-8.55, -224.1) * mm, "mid": v(-8.31, -224.15) * mm, "end": v(-8.12, -224.3) * mm});
            skArc(sketch, "E1107", {"start": v(-8.12, -224.3) * mm, "mid": v(-7.66, -224.85) * mm, "end": v(-7.22, -225.42) * mm});
            skArc(sketch, "E1108", {"start": v(-7.22, -225.42) * mm, "mid": v(-6.96, -225.74) * mm, "end": v(-6.68, -226.04) * mm});
            skArc(sketch, "E1109", {"start": v(-6.68, -226.04) * mm, "mid": v(-6.47, -226.22) * mm, "end": v(-6.23, -226.35) * mm});
            skArc(sketch, "E1110", {"start": v(-6.23, -226.35) * mm, "mid": v(-6.09, -226.38) * mm, "end": v(-5.95, -226.32) * mm});
            skArc(sketch, "E1111", {"start": v(-5.95, -226.32) * mm, "mid": v(-5.85, -226.2) * mm, "end": v(-5.8, -226.05) * mm});
            skArc(sketch, "E1112", {"start": v(-5.8, -226.05) * mm, "mid": v(-5.82, -225.8) * mm, "end": v(-5.87, -225.54) * mm});
            skArc(sketch, "E1113", {"start": v(-5.87, -225.54) * mm, "mid": v(-5.97, -225.27) * mm, "end": v(-6.1, -225.01) * mm});
            skArc(sketch, "E1114", {"start": v(-6.1, -225.01) * mm, "mid": v(-6.25, -224.76) * mm, "end": v(-6.44, -224.54) * mm});
            skArc(sketch, "E1115", {"start": v(-6.44, -224.54) * mm, "mid": v(-6.63, -224.35) * mm, "end": v(-6.84, -224.2) * mm});
            skArc(sketch, "E1116", {"start": v(-6.84, -224.2) * mm, "mid": v(-7.05, -224.03) * mm, "end": v(-7.2, -223.83) * mm});
            skArc(sketch, "E1117", {"start": v(-7.2, -223.83) * mm, "mid": v(-7.34, -223.56) * mm, "end": v(-7.42, -223.28) * mm});
            skArc(sketch, "E1118", {"start": v(-7.42, -223.28) * mm, "mid": v(-7.47, -222.96) * mm, "end": v(-7.47, -222.63) * mm});
            skArc(sketch, "E1119", {"start": v(-7.47, -222.63) * mm, "mid": v(-7.42, -222.3) * mm, "end": v(-7.32, -222) * mm});
            skArc(sketch, "E1120", {"start": v(-7.32, -222) * mm, "mid": v(-7.17, -221.6) * mm, "end": v(-7.04, -221.19) * mm});
            skArc(sketch, "E1121", {"start": v(-7.04, -221.19) * mm, "mid": v(-7.05, -221.07) * mm, "end": v(-7.13, -221) * mm});
            skArc(sketch, "E1122", {"start": v(-7.13, -221) * mm, "mid": v(-7.26, -220.98) * mm, "end": v(-7.39, -221.03) * mm});
            skArc(sketch, "E1123", {"start": v(-7.39, -221.03) * mm, "mid": v(-7.79, -221.34) * mm, "end": v(-8.18, -221.66) * mm});
            skArc(sketch, "E1124", {"start": v(-8.18, -221.66) * mm, "mid": v(-8.55, -221.93) * mm, "end": v(-8.95, -222.16) * mm});
            skArc(sketch, "E1125", {"start": v(-8.95, -222.16) * mm, "mid": v(-9.2, -222.2) * mm, "end": v(-9.43, -222.1) * mm});
            skArc(sketch, "E1126", {"start": v(-9.43, -222.1) * mm, "mid": v(-9.65, -221.85) * mm, "end": v(-9.77, -221.54) * mm});
            skArc(sketch, "E1127", {"start": v(-9.77, -221.54) * mm, "mid": v(-9.93, -220.8) * mm, "end": v(-10.05, -220.05) * mm});
            skArc(sketch, "E1128", {"start": v(-10.05, -220.05) * mm, "mid": v(-10.12, -219.72) * mm, "end": v(-10.23, -219.4) * mm});
            skArc(sketch, "E1129", {"start": v(-10.23, -219.4) * mm, "mid": v(-10.31, -219.35) * mm, "end": v(-10.4, -219.41) * mm});
            skArc(sketch, "E1130", {"start": v(-10.4, -219.41) * mm, "mid": v(-10.48, -219.86) * mm, "end": v(-10.52, -220.32) * mm});
            skArc(sketch, "E1131", {"start": v(-10.52, -220.32) * mm, "mid": v(-10.56, -221.28) * mm, "end": v(-10.6, -222.24) * mm});
            skArc(sketch, "E1132", {"start": v(38.38, -220.95) * mm, "mid": v(37.76, -221.94) * mm, "end": v(37.16, -222.94) * mm});
            skArc(sketch, "E1133", {"start": v(37.16, -222.94) * mm, "mid": v(36.98, -223.35) * mm, "end": v(36.88, -223.78) * mm});
            skArc(sketch, "E1134", {"start": v(36.88, -223.78) * mm, "mid": v(36.94, -224.06) * mm, "end": v(37.14, -224.27) * mm});
            skArc(sketch, "E1135", {"start": v(37.14, -224.27) * mm, "mid": v(37.56, -224.47) * mm, "end": v(38, -224.6) * mm});
            skArc(sketch, "E1136", {"start": v(38, -224.6) * mm, "mid": v(38.36, -224.7) * mm, "end": v(38.7, -224.81) * mm});
            skArc(sketch, "E1137", {"start": v(38.7, -224.81) * mm, "mid": v(39.06, -224.97) * mm, "end": v(39.4, -225.15) * mm});
            skArc(sketch, "E1138", {"start": v(39.4, -225.15) * mm, "mid": v(39.7, -225.33) * mm, "end": v(39.98, -225.54) * mm});
            skArc(sketch, "E1139", {"start": v(39.98, -225.54) * mm, "mid": v(40.18, -225.72) * mm, "end": v(40.34, -225.94) * mm});
            skArc(sketch, "E1140", {"start": v(40.34, -225.94) * mm, "mid": v(40.46, -226.09) * mm, "end": v(40.62, -226.2) * mm});
            skArc(sketch, "E1141", {"start": v(40.62, -226.2) * mm, "mid": v(40.77, -226.24) * mm, "end": v(40.93, -226.22) * mm});
            skArc(sketch, "E1142", {"start": v(40.93, -226.22) * mm, "mid": v(41.1, -226.12) * mm, "end": v(41.24, -225.97) * mm});
            skArc(sketch, "E1143", {"start": v(41.24, -225.97) * mm, "mid": v(41.38, -225.73) * mm, "end": v(41.5, -225.48) * mm});
            skArc(sketch, "E1144", {"start": v(41.5, -225.48) * mm, "mid": v(41.6, -225.16) * mm, "end": v(41.64, -224.83) * mm});
            skArc(sketch, "E1145", {"start": v(41.64, -224.83) * mm, "mid": v(41.65, -224.45) * mm, "end": v(41.62, -224.06) * mm});
            skArc(sketch, "E1146", {"start": v(41.62, -224.06) * mm, "mid": v(41.55, -223.67) * mm, "end": v(41.45, -223.3) * mm});
            skArc(sketch, "E1147", {"start": v(41.45, -223.3) * mm, "mid": v(41.32, -222.96) * mm, "end": v(41.15, -222.65) * mm});
            skArc(sketch, "E1148", {"start": v(41.15, -222.65) * mm, "mid": v(40.94, -222.33) * mm, "end": v(40.72, -222.02) * mm});
            skArc(sketch, "E1149", {"start": v(40.72, -222.02) * mm, "mid": v(40.6, -221.92) * mm, "end": v(40.46, -221.86) * mm});
            skArc(sketch, "E1150", {"start": v(40.46, -221.86) * mm, "mid": v(40.35, -221.88) * mm, "end": v(40.3, -221.98) * mm});
            skArc(sketch, "E1151", {"start": v(40.3, -221.98) * mm, "mid": v(40.26, -222.23) * mm, "end": v(40.24, -222.49) * mm});
            skArc(sketch, "E1152", {"start": v(40.24, -222.49) * mm, "mid": v(40.22, -222.73) * mm, "end": v(40.15, -222.96) * mm});
            skArc(sketch, "E1153", {"start": v(40.15, -222.96) * mm, "mid": v(40.05, -223.18) * mm, "end": v(39.9, -223.37) * mm});
            skArc(sketch, "E1154", {"start": v(39.9, -223.37) * mm, "mid": v(39.73, -223.52) * mm, "end": v(39.54, -223.64) * mm});
            skArc(sketch, "E1155", {"start": v(39.54, -223.64) * mm, "mid": v(39.33, -223.71) * mm, "end": v(39.11, -223.74) * mm});
            skArc(sketch, "E1156", {"start": v(39.11, -223.74) * mm, "mid": v(38.92, -223.68) * mm, "end": v(38.8, -223.53) * mm});
            skArc(sketch, "E1157", {"start": v(38.8, -223.53) * mm, "mid": v(38.75, -223.28) * mm, "end": v(38.77, -223.03) * mm});
            skArc(sketch, "E1158", {"start": v(38.77, -223.03) * mm, "mid": v(38.89, -222.6) * mm, "end": v(39.07, -222.21) * mm});
            skArc(sketch, "E1159", {"start": v(39.07, -222.21) * mm, "mid": v(39.37, -221.67) * mm, "end": v(39.7, -221.15) * mm});
            skArc(sketch, "E1160", {"start": v(39.7, -221.15) * mm, "mid": v(40, -220.64) * mm, "end": v(40.3, -220.13) * mm});
            skArc(sketch, "E1161", {"start": v(40.3, -220.13) * mm, "mid": v(40.54, -219.67) * mm, "end": v(40.75, -219.2) * mm});
            skArc(sketch, "E1162", {"start": v(40.75, -219.2) * mm, "mid": v(40.9, -218.81) * mm, "end": v(41.01, -218.43) * mm});
            skArc(sketch, "E1163", {"start": v(41.01, -218.43) * mm, "mid": v(41.02, -218.26) * mm, "end": v(40.93, -218.1) * mm});
            skArc(sketch, "E1164", {"start": v(40.93, -218.1) * mm, "mid": v(40.79, -218.05) * mm, "end": v(40.64, -218.1) * mm});
            skArc(sketch, "E1165", {"start": v(40.64, -218.1) * mm, "mid": v(40.31, -218.42) * mm, "end": v(40, -218.75) * mm});
            skArc(sketch, "E1166", {"start": v(40, -218.75) * mm, "mid": v(39.6, -219.23) * mm, "end": v(39.22, -219.72) * mm});
            skArc(sketch, "E1167", {"start": v(39.22, -219.72) * mm, "mid": v(38.79, -220.32) * mm, "end": v(38.38, -220.95) * mm});
            skArc(sketch, "E1168", {"start": v(59.77, -218.67) * mm, "mid": v(59.67, -218.85) * mm, "end": v(59.61, -219.05) * mm});
            skArc(sketch, "E1169", {"start": v(59.61, -219.05) * mm, "mid": v(59.63, -219.17) * mm, "end": v(59.7, -219.27) * mm});
            skArc(sketch, "E1170", {"start": v(59.7, -219.27) * mm, "mid": v(59.86, -219.32) * mm, "end": v(60.02, -219.32) * mm});
            skArc(sketch, "E1171", {"start": v(60.02, -219.32) * mm, "mid": v(60.3, -219.25) * mm, "end": v(60.57, -219.16) * mm});
            skArc(sketch, "E1172", {"start": v(60.57, -219.16) * mm, "mid": v(61.14, -219.03) * mm, "end": v(61.73, -219.05) * mm});
            skArc(sketch, "E1173", {"start": v(61.73, -219.05) * mm, "mid": v(62.22, -219.25) * mm, "end": v(62.6, -219.6) * mm});
            skArc(sketch, "E1174", {"start": v(62.6, -219.6) * mm, "mid": v(62.79, -220.04) * mm, "end": v(62.75, -220.5) * mm});
            skArc(sketch, "E1175", {"start": v(62.75, -220.5) * mm, "mid": v(62.52, -220.95) * mm, "end": v(62.14, -221.3) * mm});
            skArc(sketch, "E1176", {"start": v(62.14, -221.3) * mm, "mid": v(61.9, -221.46) * mm, "end": v(61.68, -221.66) * mm});
            skArc(sketch, "E1177", {"start": v(61.68, -221.66) * mm, "mid": v(61.58, -221.82) * mm, "end": v(61.55, -222) * mm});
            skArc(sketch, "E1178", {"start": v(61.55, -222) * mm, "mid": v(61.6, -222.2) * mm, "end": v(61.72, -222.36) * mm});
            skArc(sketch, "E1179", {"start": v(61.72, -222.36) * mm, "mid": v(61.98, -222.57) * mm, "end": v(62.25, -222.75) * mm});
            skArc(sketch, "E1180", {"start": v(62.25, -222.75) * mm, "mid": v(62.65, -223.13) * mm, "end": v(62.89, -223.63) * mm});
            skArc(sketch, "E1181", {"start": v(62.89, -223.63) * mm, "mid": v(62.91, -224.17) * mm, "end": v(62.72, -224.68) * mm});
            skArc(sketch, "E1182", {"start": v(62.72, -224.68) * mm, "mid": v(62.33, -225.11) * mm, "end": v(61.8, -225.38) * mm});
            skArc(sketch, "E1183", {"start": v(61.8, -225.38) * mm, "mid": v(61.21, -225.46) * mm, "end": v(60.62, -225.34) * mm});
            skArc(sketch, "E1184", {"start": v(60.62, -225.34) * mm, "mid": v(60.36, -225.26) * mm, "end": v(60.09, -225.2) * mm});
            skArc(sketch, "E1185", {"start": v(60.09, -225.2) * mm, "mid": v(59.86, -225.21) * mm, "end": v(59.64, -225.26) * mm});
            skArc(sketch, "E1186", {"start": v(59.64, -225.26) * mm, "mid": v(59.47, -225.35) * mm, "end": v(59.34, -225.49) * mm});
            skArc(sketch, "E1187", {"start": v(59.34, -225.49) * mm, "mid": v(59.25, -225.65) * mm, "end": v(59.23, -225.84) * mm});
            skArc(sketch, "E1188", {"start": v(59.23, -225.84) * mm, "mid": v(59.27, -226.04) * mm, "end": v(59.4, -226.2) * mm});
            skArc(sketch, "E1189", {"start": v(59.4, -226.2) * mm, "mid": v(59.63, -226.37) * mm, "end": v(59.89, -226.48) * mm});
            skArc(sketch, "E1190", {"start": v(59.89, -226.48) * mm, "mid": v(60.25, -226.57) * mm, "end": v(60.61, -226.6) * mm});
            skArc(sketch, "E1191", {"start": v(60.61, -226.6) * mm, "mid": v(61.05, -226.6) * mm, "end": v(61.48, -226.56) * mm});
            skArc(sketch, "E1192", {"start": v(61.48, -226.56) * mm, "mid": v(62.07, -226.43) * mm, "end": v(62.65, -226.2) * mm});
            skArc(sketch, "E1193", {"start": v(62.65, -226.2) * mm, "mid": v(63.03, -225.94) * mm, "end": v(63.31, -225.57) * mm});
            skArc(sketch, "E1194", {"start": v(63.31, -225.57) * mm, "mid": v(63.54, -225.01) * mm, "end": v(63.64, -224.43) * mm});
            skArc(sketch, "E1195", {"start": v(63.64, -224.43) * mm, "mid": v(63.7, -223.34) * mm, "end": v(63.73, -222.25) * mm});
            skArc(sketch, "E1196", {"start": v(63.73, -222.25) * mm, "mid": v(63.7, -221.3) * mm, "end": v(63.64, -220.34) * mm});
            skArc(sketch, "E1197", {"start": v(63.64, -220.34) * mm, "mid": v(63.54, -219.7) * mm, "end": v(63.35, -219.1) * mm});
            skArc(sketch, "E1198", {"start": v(63.35, -219.1) * mm, "mid": v(63.14, -218.68) * mm, "end": v(62.84, -218.33) * mm});
            skArc(sketch, "E1199", {"start": v(62.84, -218.33) * mm, "mid": v(62.48, -218.09) * mm, "end": v(62.07, -217.95) * mm});
            skArc(sketch, "E1200", {"start": v(62.07, -217.95) * mm, "mid": v(61.73, -217.9) * mm, "end": v(61.39, -217.9) * mm});
            skArc(sketch, "E1201", {"start": v(61.39, -217.9) * mm, "mid": v(61.04, -217.94) * mm, "end": v(60.7, -218.03) * mm});
            skArc(sketch, "E1202", {"start": v(60.7, -218.03) * mm, "mid": v(60.41, -218.14) * mm, "end": v(60.14, -218.3) * mm});
            skArc(sketch, "E1203", {"start": v(60.14, -218.3) * mm, "mid": v(59.93, -218.46) * mm, "end": v(59.77, -218.67) * mm});
            skArc(sketch, "E1204", {"start": v(67.23, -218.85) * mm, "mid": v(66.79, -219.17) * mm, "end": v(66.35, -219.49) * mm});
            skArc(sketch, "E1205", {"start": v(66.35, -219.49) * mm, "mid": v(66.3, -219.55) * mm, "end": v(66.31, -219.63) * mm});
            skArc(sketch, "E1206", {"start": v(66.31, -219.63) * mm, "mid": v(66.36, -219.68) * mm, "end": v(66.44, -219.7) * mm});
            skArc(sketch, "E1207", {"start": v(66.44, -219.7) * mm, "mid": v(66.94, -219.53) * mm, "end": v(67.44, -219.38) * mm});
            skArc(sketch, "E1208", {"start": v(67.44, -219.38) * mm, "mid": v(68.13, -219.25) * mm, "end": v(68.82, -219.28) * mm});
            skArc(sketch, "E1209", {"start": v(68.82, -219.28) * mm, "mid": v(69.36, -219.5) * mm, "end": v(69.78, -219.9) * mm});
            skArc(sketch, "E1210", {"start": v(69.78, -219.9) * mm, "mid": v(69.96, -220.4) * mm, "end": v(69.88, -220.9) * mm});
            skArc(sketch, "E1211", {"start": v(69.88, -220.9) * mm, "mid": v(69.57, -221.43) * mm, "end": v(69.1, -221.83) * mm});
            skArc(sketch, "E1212", {"start": v(69.1, -221.83) * mm, "mid": v(68.79, -222.04) * mm, "end": v(68.48, -222.26) * mm});
            skArc(sketch, "E1213", {"start": v(68.48, -222.26) * mm, "mid": v(68.38, -222.37) * mm, "end": v(68.33, -222.51) * mm});
            skArc(sketch, "E1214", {"start": v(68.33, -222.51) * mm, "mid": v(68.35, -222.62) * mm, "end": v(68.44, -222.67) * mm});
            skArc(sketch, "E1215", {"start": v(68.44, -222.67) * mm, "mid": v(68.7, -222.7) * mm, "end": v(68.98, -222.72) * mm});
            skArc(sketch, "E1216", {"start": v(68.98, -222.72) * mm, "mid": v(69.22, -222.76) * mm, "end": v(69.45, -222.85) * mm});
            skArc(sketch, "E1217", {"start": v(69.45, -222.85) * mm, "mid": v(69.67, -223.01) * mm, "end": v(69.86, -223.2) * mm});
            skArc(sketch, "E1218", {"start": v(69.86, -223.2) * mm, "mid": v(70.02, -223.46) * mm, "end": v(70.13, -223.74) * mm});
            skArc(sketch, "E1219", {"start": v(70.13, -223.74) * mm, "mid": v(70.2, -224.04) * mm, "end": v(70.23, -224.35) * mm});
            skArc(sketch, "E1220", {"start": v(70.23, -224.35) * mm, "mid": v(70.2, -224.71) * mm, "end": v(70.1, -225.06) * mm});
            skArc(sketch, "E1221", {"start": v(70.1, -225.06) * mm, "mid": v(69.95, -225.3) * mm, "end": v(69.73, -225.47) * mm});
            skArc(sketch, "E1222", {"start": v(69.73, -225.47) * mm, "mid": v(69.42, -225.57) * mm, "end": v(69.09, -225.59) * mm});
            skArc(sketch, "E1223", {"start": v(69.09, -225.59) * mm, "mid": v(68.58, -225.52) * mm, "end": v(68.08, -225.41) * mm});
            skArc(sketch, "E1224", {"start": v(68.08, -225.41) * mm, "mid": v(67.58, -225.29) * mm, "end": v(67.08, -225.18) * mm});
            skArc(sketch, "E1225", {"start": v(67.08, -225.18) * mm, "mid": v(66.88, -225.17) * mm, "end": v(66.69, -225.23) * mm});
            skArc(sketch, "E1226", {"start": v(66.69, -225.23) * mm, "mid": v(66.6, -225.33) * mm, "end": v(66.62, -225.45) * mm});
            skArc(sketch, "E1227", {"start": v(66.62, -225.45) * mm, "mid": v(66.8, -225.7) * mm, "end": v(67.01, -225.93) * mm});
            skArc(sketch, "E1228", {"start": v(67.01, -225.93) * mm, "mid": v(67.7, -226.42) * mm, "end": v(68.5, -226.7) * mm});
            skArc(sketch, "E1229", {"start": v(68.5, -226.7) * mm, "mid": v(69.22, -226.64) * mm, "end": v(69.84, -226.27) * mm});
            skArc(sketch, "E1230", {"start": v(69.84, -226.27) * mm, "mid": v(70.42, -225.52) * mm, "end": v(70.75, -224.63) * mm});
            skArc(sketch, "E1231", {"start": v(70.75, -224.63) * mm, "mid": v(70.92, -223.38) * mm, "end": v(70.94, -222.12) * mm});
            skArc(sketch, "E1232", {"start": v(70.94, -222.12) * mm, "mid": v(70.82, -220.85) * mm, "end": v(70.61, -219.6) * mm});
            skArc(sketch, "E1233", {"start": v(70.61, -219.6) * mm, "mid": v(70.35, -218.9) * mm, "end": v(69.89, -218.34) * mm});
            skArc(sketch, "E1234", {"start": v(69.89, -218.34) * mm, "mid": v(69.36, -218.07) * mm, "end": v(68.78, -218.1) * mm});
            skArc(sketch, "E1235", {"start": v(68.78, -218.1) * mm, "mid": v(67.97, -218.4) * mm, "end": v(67.23, -218.85) * mm});
            skArc(sketch, "E1236", {"start": v(74.4, -218.6) * mm, "mid": v(74.1, -218.86) * mm, "end": v(73.88, -219.18) * mm});
            skArc(sketch, "E1237", {"start": v(73.88, -219.18) * mm, "mid": v(73.68, -219.65) * mm, "end": v(73.53, -220.15) * mm});
            skArc(sketch, "E1238", {"start": v(73.53, -220.15) * mm, "mid": v(73.41, -220.77) * mm, "end": v(73.36, -221.4) * mm});
            skArc(sketch, "E1239", {"start": v(73.36, -221.4) * mm, "mid": v(73.36, -222.12) * mm, "end": v(73.4, -222.84) * mm});
            skArc(sketch, "E1240", {"start": v(73.4, -222.84) * mm, "mid": v(73.51, -223.76) * mm, "end": v(73.67, -224.67) * mm});
            skArc(sketch, "E1241", {"start": v(73.67, -224.67) * mm, "mid": v(73.84, -225.17) * mm, "end": v(74.12, -225.62) * mm});
            skArc(sketch, "E1242", {"start": v(74.12, -225.62) * mm, "mid": v(74.47, -225.92) * mm, "end": v(74.9, -226.09) * mm});
            skArc(sketch, "E1243", {"start": v(74.9, -226.09) * mm, "mid": v(75.56, -226.2) * mm, "end": v(76.23, -226.24) * mm});
            skArc(sketch, "E1244", {"start": v(76.23, -226.24) * mm, "mid": v(76.9, -226.2) * mm, "end": v(77.55, -226.09) * mm});
            skArc(sketch, "E1245", {"start": v(77.55, -226.09) * mm, "mid": v(77.98, -225.92) * mm, "end": v(78.33, -225.62) * mm});
            skArc(sketch, "E1246", {"start": v(78.33, -225.62) * mm, "mid": v(78.61, -225.17) * mm, "end": v(78.78, -224.67) * mm});
            skArc(sketch, "E1247", {"start": v(78.78, -224.67) * mm, "mid": v(78.94, -223.76) * mm, "end": v(79.05, -222.84) * mm});
            skArc(sketch, "E1248", {"start": v(79.05, -222.84) * mm, "mid": v(79.09, -221.83) * mm, "end": v(79, -220.82) * mm});
            skArc(sketch, "E1249", {"start": v(79, -220.82) * mm, "mid": v(78.82, -219.98) * mm, "end": v(78.47, -219.2) * mm});
            skArc(sketch, "E1250", {"start": v(78.47, -219.2) * mm, "mid": v(78.05, -218.61) * mm, "end": v(77.5, -218.15) * mm});
            skArc(sketch, "E1251", {"start": v(77.5, -218.15) * mm, "mid": v(76.9, -217.87) * mm, "end": v(76.23, -217.77) * mm});
            skArc(sketch, "E1252", {"start": v(76.23, -217.77) * mm, "mid": v(76.09, -217.78) * mm, "end": v(75.95, -217.82) * mm});
            skArc(sketch, "E1253", {"start": v(75.95, -217.82) * mm, "mid": v(75.72, -217.91) * mm, "end": v(75.48, -218.01) * mm});
            skArc(sketch, "E1254", {"start": v(75.48, -218.01) * mm, "mid": v(75.21, -218.15) * mm, "end": v(74.95, -218.29) * mm});
            skArc(sketch, "E1255", {"start": v(74.95, -218.29) * mm, "mid": v(74.67, -218.44) * mm, "end": v(74.4, -218.6) * mm});
            skArc(sketch, "E1256", {"start": v(77.73, -222.32) * mm, "mid": v(77.7, -222.96) * mm, "end": v(77.64, -223.6) * mm});
            skArc(sketch, "E1257", {"start": v(77.64, -223.6) * mm, "mid": v(77.53, -224.06) * mm, "end": v(77.35, -224.5) * mm});
            skArc(sketch, "E1258", {"start": v(77.35, -224.5) * mm, "mid": v(77.15, -224.8) * mm, "end": v(76.88, -225.04) * mm});
            skArc(sketch, "E1259", {"start": v(76.88, -225.04) * mm, "mid": v(76.57, -225.19) * mm, "end": v(76.24, -225.24) * mm});
            skArc(sketch, "E1260", {"start": v(76.24, -225.24) * mm, "mid": v(75.67, -225.12) * mm, "end": v(75.2, -224.78) * mm});
            skArc(sketch, "E1261", {"start": v(75.2, -224.78) * mm, "mid": v(74.77, -224.21) * mm, "end": v(74.48, -223.55) * mm});
            skArc(sketch, "E1262", {"start": v(74.48, -223.55) * mm, "mid": v(74.3, -222.71) * mm, "end": v(74.27, -221.85) * mm});
            skArc(sketch, "E1263", {"start": v(74.27, -221.85) * mm, "mid": v(74.39, -220.96) * mm, "end": v(74.64, -220.1) * mm});
            skArc(sketch, "E1264", {"start": v(74.64, -220.1) * mm, "mid": v(74.98, -219.5) * mm, "end": v(75.5, -219.06) * mm});
            skArc(sketch, "E1265", {"start": v(75.5, -219.06) * mm, "mid": v(76.02, -218.92) * mm, "end": v(76.54, -219.1) * mm});
            skArc(sketch, "E1266", {"start": v(76.54, -219.1) * mm, "mid": v(77.08, -219.64) * mm, "end": v(77.43, -220.33) * mm});
            skArc(sketch, "E1267", {"start": v(77.43, -220.33) * mm, "mid": v(77.65, -221.32) * mm, "end": v(77.73, -222.32) * mm});
            skArc(sketch, "E1268", {"start": v(81.93, -218.37) * mm, "mid": v(81.5, -218.96) * mm, "end": v(81.25, -219.64) * mm});
            skArc(sketch, "E1269", {"start": v(81.25, -219.64) * mm, "mid": v(81.2, -220.45) * mm, "end": v(81.3, -221.26) * mm});
            skArc(sketch, "E1270", {"start": v(81.3, -221.26) * mm, "mid": v(81.6, -222.01) * mm, "end": v(82.03, -222.69) * mm});
            skArc(sketch, "E1271", {"start": v(82.03, -222.69) * mm, "mid": v(82.57, -223.16) * mm, "end": v(83.23, -223.45) * mm});
            skArc(sketch, "E1272", {"start": v(83.23, -223.45) * mm, "mid": v(83.61, -223.57) * mm, "end": v(84, -223.72) * mm});
            skArc(sketch, "E1273", {"start": v(84, -223.72) * mm, "mid": v(84.33, -223.9) * mm, "end": v(84.64, -224.11) * mm});
            skArc(sketch, "E1274", {"start": v(84.64, -224.11) * mm, "mid": v(84.87, -224.32) * mm, "end": v(85.08, -224.55) * mm});
            skArc(sketch, "E1275", {"start": v(85.08, -224.55) * mm, "mid": v(85.19, -224.75) * mm, "end": v(85.23, -224.97) * mm});
            skArc(sketch, "E1276", {"start": v(85.23, -224.97) * mm, "mid": v(85.18, -225.16) * mm, "end": v(85.06, -225.3) * mm});
            skArc(sketch, "E1277", {"start": v(85.06, -225.3) * mm, "mid": v(84.84, -225.43) * mm, "end": v(84.6, -225.51) * mm});
            skArc(sketch, "E1278", {"start": v(84.6, -225.51) * mm, "mid": v(84.25, -225.56) * mm, "end": v(83.9, -225.55) * mm});
            skArc(sketch, "E1279", {"start": v(83.9, -225.55) * mm, "mid": v(83.49, -225.5) * mm, "end": v(83.08, -225.41) * mm});
            skArc(sketch, "E1280", {"start": v(83.08, -225.41) * mm, "mid": v(82.58, -225.29) * mm, "end": v(82.08, -225.18) * mm});
            skArc(sketch, "E1281", {"start": v(82.08, -225.18) * mm, "mid": v(81.88, -225.17) * mm, "end": v(81.69, -225.23) * mm});
            skArc(sketch, "E1282", {"start": v(81.69, -225.23) * mm, "mid": v(81.6, -225.33) * mm, "end": v(81.62, -225.45) * mm});
            skArc(sketch, "E1283", {"start": v(81.62, -225.45) * mm, "mid": v(81.8, -225.7) * mm, "end": v(82.01, -225.93) * mm});
            skArc(sketch, "E1284", {"start": v(82.01, -225.93) * mm, "mid": v(82.72, -226.44) * mm, "end": v(83.55, -226.71) * mm});
            skArc(sketch, "E1285", {"start": v(83.55, -226.71) * mm, "mid": v(84.31, -226.66) * mm, "end": v(84.96, -226.27) * mm});
            skArc(sketch, "E1286", {"start": v(84.96, -226.27) * mm, "mid": v(85.56, -225.48) * mm, "end": v(85.9, -224.56) * mm});
            skArc(sketch, "E1287", {"start": v(85.9, -224.56) * mm, "mid": v(86.05, -223.29) * mm, "end": v(86.04, -222) * mm});
            skArc(sketch, "E1288", {"start": v(86.04, -222) * mm, "mid": v(85.87, -220.84) * mm, "end": v(85.55, -219.7) * mm});
            skArc(sketch, "E1289", {"start": v(85.55, -219.7) * mm, "mid": v(85.14, -218.88) * mm, "end": v(84.53, -218.19) * mm});
            skArc(sketch, "E1290", {"start": v(84.53, -218.19) * mm, "mid": v(83.93, -217.84) * mm, "end": v(83.24, -217.76) * mm});
            skArc(sketch, "E1291", {"start": v(83.24, -217.76) * mm, "mid": v(82.53, -217.95) * mm, "end": v(81.93, -218.37) * mm});
            skArc(sketch, "E1292", {"start": v(85.23, -221.3) * mm, "mid": v(85.2, -221.58) * mm, "end": v(85.11, -221.85) * mm});
            skArc(sketch, "E1293", {"start": v(85.11, -221.85) * mm, "mid": v(84.97, -222.1) * mm, "end": v(84.79, -222.31) * mm});
            skArc(sketch, "E1294", {"start": v(84.79, -222.31) * mm, "mid": v(84.56, -222.5) * mm, "end": v(84.3, -222.63) * mm});
            skArc(sketch, "E1295", {"start": v(84.3, -222.63) * mm, "mid": v(84.02, -222.71) * mm, "end": v(83.73, -222.74) * mm});
            skArc(sketch, "E1296", {"start": v(83.73, -222.74) * mm, "mid": v(83.24, -222.65) * mm, "end": v(82.82, -222.4) * mm});
            skArc(sketch, "E1297", {"start": v(82.82, -222.4) * mm, "mid": v(82.49, -222) * mm, "end": v(82.28, -221.53) * mm});
            skArc(sketch, "E1298", {"start": v(82.28, -221.53) * mm, "mid": v(82.21, -220.97) * mm, "end": v(82.3, -220.41) * mm});
            skArc(sketch, "E1299", {"start": v(82.3, -220.41) * mm, "mid": v(82.52, -219.88) * mm, "end": v(82.87, -219.43) * mm});
            skArc(sketch, "E1300", {"start": v(82.87, -219.43) * mm, "mid": v(83.2, -219.2) * mm, "end": v(83.6, -219.12) * mm});
            skArc(sketch, "E1301", {"start": v(83.6, -219.12) * mm, "mid": v(84.02, -219.18) * mm, "end": v(84.4, -219.39) * mm});
            skArc(sketch, "E1302", {"start": v(84.4, -219.39) * mm, "mid": v(84.75, -219.75) * mm, "end": v(85, -220.2) * mm});
            skArc(sketch, "E1303", {"start": v(85, -220.2) * mm, "mid": v(85.17, -220.74) * mm, "end": v(85.23, -221.3) * mm});
            skArc(sketch, "E1304", {"start": v(95.62, -219.15) * mm, "mid": v(95.5, -219.52) * mm, "end": v(95.43, -219.89) * mm});
            skArc(sketch, "E1305", {"start": v(95.43, -219.89) * mm, "mid": v(95.37, -220.44) * mm, "end": v(95.33, -220.99) * mm});
            skArc(sketch, "E1306", {"start": v(95.33, -220.99) * mm, "mid": v(95.31, -221.6) * mm, "end": v(95.32, -222.21) * mm});
            skArc(sketch, "E1307", {"start": v(95.32, -222.21) * mm, "mid": v(95.35, -222.8) * mm, "end": v(95.4, -223.4) * mm});
            skArc(sketch, "E1308", {"start": v(95.4, -223.4) * mm, "mid": v(95.67, -224.51) * mm, "end": v(96.19, -225.52) * mm});
            skArc(sketch, "E1309", {"start": v(96.19, -225.52) * mm, "mid": v(96.85, -226.15) * mm, "end": v(97.73, -226.42) * mm});
            skArc(sketch, "E1310", {"start": v(97.73, -226.42) * mm, "mid": v(98.54, -226.26) * mm, "end": v(99.15, -225.7) * mm});
            skArc(sketch, "E1311", {"start": v(99.15, -225.7) * mm, "mid": v(99.58, -224.76) * mm, "end": v(99.73, -223.74) * mm});
            skArc(sketch, "E1312", {"start": v(99.73, -223.74) * mm, "mid": v(99.7, -223.16) * mm, "end": v(99.63, -222.58) * mm});
            skArc(sketch, "E1313", {"start": v(99.63, -222.58) * mm, "mid": v(99.51, -222.2) * mm, "end": v(99.31, -221.85) * mm});
            skArc(sketch, "E1314", {"start": v(99.31, -221.85) * mm, "mid": v(99.06, -221.61) * mm, "end": v(98.75, -221.47) * mm});
            skArc(sketch, "E1315", {"start": v(98.75, -221.47) * mm, "mid": v(98.34, -221.39) * mm, "end": v(97.93, -221.38) * mm});
            skArc(sketch, "E1316", {"start": v(97.93, -221.38) * mm, "mid": v(97.6, -221.4) * mm, "end": v(97.27, -221.36) * mm});
            skArc(sketch, "E1317", {"start": v(97.27, -221.36) * mm, "mid": v(97, -221.28) * mm, "end": v(96.77, -221.15) * mm});
            skArc(sketch, "E1318", {"start": v(96.77, -221.15) * mm, "mid": v(96.62, -221) * mm, "end": v(96.52, -220.8) * mm});
            skArc(sketch, "E1319", {"start": v(96.52, -220.8) * mm, "mid": v(96.5, -220.6) * mm, "end": v(96.53, -220.38) * mm});
            skArc(sketch, "E1320", {"start": v(96.53, -220.38) * mm, "mid": v(96.65, -220.16) * mm, "end": v(96.82, -219.97) * mm});
            skArc(sketch, "E1321", {"start": v(96.82, -219.97) * mm, "mid": v(97.06, -219.8) * mm, "end": v(97.33, -219.67) * mm});
            skArc(sketch, "E1322", {"start": v(97.33, -219.67) * mm, "mid": v(97.65, -219.57) * mm, "end": v(97.98, -219.52) * mm});
            skArc(sketch, "E1323", {"start": v(97.98, -219.52) * mm, "mid": v(98.33, -219.51) * mm, "end": v(98.68, -219.55) * mm});
            skArc(sketch, "E1324", {"start": v(98.68, -219.55) * mm, "mid": v(99.01, -219.6) * mm, "end": v(99.35, -219.62) * mm});
            skArc(sketch, "E1325", {"start": v(99.35, -219.62) * mm, "mid": v(99.56, -219.58) * mm, "end": v(99.76, -219.49) * mm});
            skArc(sketch, "E1326", {"start": v(99.76, -219.49) * mm, "mid": v(99.86, -219.36) * mm, "end": v(99.9, -219.2) * mm});
            skArc(sketch, "E1327", {"start": v(99.9, -219.2) * mm, "mid": v(99.86, -219) * mm, "end": v(99.77, -218.8) * mm});
            skArc(sketch, "E1328", {"start": v(99.77, -218.8) * mm, "mid": v(99.37, -218.33) * mm, "end": v(98.85, -218) * mm});
            skArc(sketch, "E1329", {"start": v(98.85, -218) * mm, "mid": v(98.23, -217.8) * mm, "end": v(97.58, -217.78) * mm});
            skArc(sketch, "E1330", {"start": v(97.58, -217.78) * mm, "mid": v(96.95, -217.92) * mm, "end": v(96.37, -218.2) * mm});
            skArc(sketch, "E1331", {"start": v(96.37, -218.2) * mm, "mid": v(95.92, -218.62) * mm, "end": v(95.62, -219.15) * mm});
            skArc(sketch, "E1332", {"start": v(99.23, -224.3) * mm, "mid": v(99.2, -224.58) * mm, "end": v(99.11, -224.85) * mm});
            skArc(sketch, "E1333", {"start": v(99.11, -224.85) * mm, "mid": v(98.97, -225.1) * mm, "end": v(98.79, -225.31) * mm});
            skArc(sketch, "E1334", {"start": v(98.79, -225.31) * mm, "mid": v(98.56, -225.5) * mm, "end": v(98.3, -225.63) * mm});
            skArc(sketch, "E1335", {"start": v(98.3, -225.63) * mm, "mid": v(98.02, -225.71) * mm, "end": v(97.73, -225.74) * mm});
            skArc(sketch, "E1336", {"start": v(97.73, -225.74) * mm, "mid": v(97.24, -225.65) * mm, "end": v(96.82, -225.4) * mm});
            skArc(sketch, "E1337", {"start": v(96.82, -225.4) * mm, "mid": v(96.49, -225) * mm, "end": v(96.28, -224.53) * mm});
            skArc(sketch, "E1338", {"start": v(96.28, -224.53) * mm, "mid": v(96.21, -223.97) * mm, "end": v(96.3, -223.41) * mm});
            skArc(sketch, "E1339", {"start": v(96.3, -223.41) * mm, "mid": v(96.52, -222.88) * mm, "end": v(96.87, -222.43) * mm});
            skArc(sketch, "E1340", {"start": v(96.87, -222.43) * mm, "mid": v(97.2, -222.2) * mm, "end": v(97.6, -222.12) * mm});
            skArc(sketch, "E1341", {"start": v(97.6, -222.12) * mm, "mid": v(98.02, -222.18) * mm, "end": v(98.4, -222.39) * mm});
            skArc(sketch, "E1342", {"start": v(98.4, -222.39) * mm, "mid": v(98.75, -222.75) * mm, "end": v(99, -223.2) * mm});
            skArc(sketch, "E1343", {"start": v(99, -223.2) * mm, "mid": v(99.17, -223.74) * mm, "end": v(99.23, -224.3) * mm});
            skArc(sketch, "E1344", {"start": v(-53.06, -219.42) * mm, "mid": v(-53.3, -220.04) * mm, "end": v(-53.35, -220.7) * mm});
            skArc(sketch, "E1345", {"start": v(-53.35, -220.7) * mm, "mid": v(-53.22, -222.1) * mm, "end": v(-53.03, -223.5) * mm});
            skArc(sketch, "E1346", {"start": v(-53.03, -223.5) * mm, "mid": v(-52.78, -224.88) * mm, "end": v(-52.5, -226.26) * mm});
            skArc(sketch, "E1347", {"start": v(-52.5, -226.26) * mm, "mid": v(-52.28, -226.6) * mm, "end": v(-51.9, -226.74) * mm});
            skArc(sketch, "E1348", {"start": v(-51.9, -226.74) * mm, "mid": v(-51.56, -226.6) * mm, "end": v(-51.42, -226.27) * mm});
            skArc(sketch, "E1349", {"start": v(-51.42, -226.27) * mm, "mid": v(-51.4, -224.74) * mm, "end": v(-51.42, -223.2) * mm});
            skArc(sketch, "E1350", {"start": v(-51.42, -223.2) * mm, "mid": v(-51.48, -221.68) * mm, "end": v(-51.58, -220.16) * mm});
            skArc(sketch, "E1351", {"start": v(-51.58, -220.16) * mm, "mid": v(-51.73, -219.59) * mm, "end": v(-52.07, -219.1) * mm});
            skArc(sketch, "E1352", {"start": v(-52.07, -219.1) * mm, "mid": v(-52.18, -219.03) * mm, "end": v(-52.3, -218.98) * mm});
            skArc(sketch, "E1353", {"start": v(-52.3, -218.98) * mm, "mid": v(-52.44, -218.97) * mm, "end": v(-52.57, -219) * mm});
            skArc(sketch, "E1354", {"start": v(-52.57, -219) * mm, "mid": v(-52.7, -219.05) * mm, "end": v(-52.83, -219.15) * mm});
            skArc(sketch, "E1355", {"start": v(-52.83, -219.15) * mm, "mid": v(-52.95, -219.28) * mm, "end": v(-53.06, -219.42) * mm});
            skArc(sketch, "E1356", {"start": v(-48.97, -219.9) * mm, "mid": v(-49.18, -220.78) * mm, "end": v(-49.2, -221.68) * mm});
            skArc(sketch, "E1357", {"start": v(-49.2, -221.68) * mm, "mid": v(-49.03, -222.77) * mm, "end": v(-48.74, -223.83) * mm});
            skArc(sketch, "E1358", {"start": v(-48.74, -223.83) * mm, "mid": v(-48.35, -224.78) * mm, "end": v(-47.85, -225.68) * mm});
            skArc(sketch, "E1359", {"start": v(-47.85, -225.68) * mm, "mid": v(-47.38, -226.19) * mm, "end": v(-46.75, -226.49) * mm});
            skArc(sketch, "E1360", {"start": v(-46.75, -226.49) * mm, "mid": v(-46.33, -226.6) * mm, "end": v(-45.91, -226.7) * mm});
            skArc(sketch, "E1361", {"start": v(-45.91, -226.7) * mm, "mid": v(-45.84, -226.7) * mm, "end": v(-45.8, -226.63) * mm});
            skArc(sketch, "E1362", {"start": v(-45.8, -226.63) * mm, "mid": v(-45.82, -226.55) * mm, "end": v(-45.87, -226.48) * mm});
            skArc(sketch, "E1363", {"start": v(-45.87, -226.48) * mm, "mid": v(-46.27, -226.2) * mm, "end": v(-46.67, -225.92) * mm});
            skArc(sketch, "E1364", {"start": v(-46.67, -225.92) * mm, "mid": v(-46.94, -225.68) * mm, "end": v(-47.16, -225.4) * mm});
            skArc(sketch, "E1365", {"start": v(-47.16, -225.4) * mm, "mid": v(-47.36, -225.03) * mm, "end": v(-47.5, -224.64) * mm});
            skArc(sketch, "E1366", {"start": v(-47.5, -224.64) * mm, "mid": v(-47.6, -224.22) * mm, "end": v(-47.64, -223.79) * mm});
            skArc(sketch, "E1367", {"start": v(-47.64, -223.79) * mm, "mid": v(-47.62, -223.37) * mm, "end": v(-47.54, -222.95) * mm});
            skArc(sketch, "E1368", {"start": v(-47.54, -222.95) * mm, "mid": v(-47.39, -222.11) * mm, "end": v(-47.36, -221.26) * mm});
            skArc(sketch, "E1369", {"start": v(-47.36, -221.26) * mm, "mid": v(-47.48, -220.48) * mm, "end": v(-47.74, -219.74) * mm});
            skArc(sketch, "E1370", {"start": v(-47.74, -219.74) * mm, "mid": v(-48, -219.47) * mm, "end": v(-48.37, -219.4) * mm});
            skArc(sketch, "E1371", {"start": v(-48.37, -219.4) * mm, "mid": v(-48.74, -219.57) * mm, "end": v(-48.97, -219.9) * mm});
            skArc(sketch, "E1372", {"start": v(-27.97, -219.9) * mm, "mid": v(-28.18, -220.78) * mm, "end": v(-28.2, -221.68) * mm});
            skArc(sketch, "E1373", {"start": v(-28.2, -221.68) * mm, "mid": v(-28.03, -222.77) * mm, "end": v(-27.74, -223.83) * mm});
            skArc(sketch, "E1374", {"start": v(-27.74, -223.83) * mm, "mid": v(-27.35, -224.78) * mm, "end": v(-26.85, -225.68) * mm});
            skArc(sketch, "E1375", {"start": v(-26.85, -225.68) * mm, "mid": v(-26.38, -226.19) * mm, "end": v(-25.75, -226.49) * mm});
            skArc(sketch, "E1376", {"start": v(-25.75, -226.49) * mm, "mid": v(-25.33, -226.6) * mm, "end": v(-24.91, -226.7) * mm});
            skArc(sketch, "E1377", {"start": v(-24.91, -226.7) * mm, "mid": v(-24.84, -226.7) * mm, "end": v(-24.8, -226.63) * mm});
            skArc(sketch, "E1378", {"start": v(-24.8, -226.63) * mm, "mid": v(-24.82, -226.55) * mm, "end": v(-24.87, -226.48) * mm});
            skArc(sketch, "E1379", {"start": v(-24.87, -226.48) * mm, "mid": v(-25.27, -226.2) * mm, "end": v(-25.67, -225.92) * mm});
            skArc(sketch, "E1380", {"start": v(-25.67, -225.92) * mm, "mid": v(-25.94, -225.68) * mm, "end": v(-26.16, -225.4) * mm});
            skArc(sketch, "E1381", {"start": v(-26.16, -225.4) * mm, "mid": v(-26.36, -225.03) * mm, "end": v(-26.5, -224.64) * mm});
            skArc(sketch, "E1382", {"start": v(-26.5, -224.64) * mm, "mid": v(-26.6, -224.22) * mm, "end": v(-26.64, -223.79) * mm});
            skArc(sketch, "E1383", {"start": v(-26.64, -223.79) * mm, "mid": v(-26.62, -223.37) * mm, "end": v(-26.54, -222.95) * mm});
            skArc(sketch, "E1384", {"start": v(-26.54, -222.95) * mm, "mid": v(-26.39, -222.11) * mm, "end": v(-26.36, -221.26) * mm});
            skArc(sketch, "E1385", {"start": v(-26.36, -221.26) * mm, "mid": v(-26.48, -220.48) * mm, "end": v(-26.74, -219.74) * mm});
            skArc(sketch, "E1386", {"start": v(-26.74, -219.74) * mm, "mid": v(-27, -219.47) * mm, "end": v(-27.37, -219.4) * mm});
            skArc(sketch, "E1387", {"start": v(-27.37, -219.4) * mm, "mid": v(-27.74, -219.57) * mm, "end": v(-27.97, -219.9) * mm});
            skArc(sketch, "E1388", {"start": v(45.78, -220.96) * mm, "mid": v(45.18, -221.87) * mm, "end": v(44.6, -222.8) * mm});
            skArc(sketch, "E1389", {"start": v(44.6, -222.8) * mm, "mid": v(44.39, -223.33) * mm, "end": v(44.3, -223.9) * mm});
            skArc(sketch, "E1390", {"start": v(44.3, -223.9) * mm, "mid": v(44.4, -224.26) * mm, "end": v(44.69, -224.5) * mm});
            skArc(sketch, "E1391", {"start": v(44.69, -224.5) * mm, "mid": v(45.2, -224.68) * mm, "end": v(45.73, -224.74) * mm});
            skArc(sketch, "E1392", {"start": v(45.73, -224.74) * mm, "mid": v(46.02, -224.76) * mm, "end": v(46.3, -224.83) * mm});
            skArc(sketch, "E1393", {"start": v(46.3, -224.83) * mm, "mid": v(46.56, -224.95) * mm, "end": v(46.8, -225.1) * mm});
            skArc(sketch, "E1394", {"start": v(46.8, -225.1) * mm, "mid": v(46.98, -225.3) * mm, "end": v(47.13, -225.51) * mm});
            skArc(sketch, "E1395", {"start": v(47.13, -225.51) * mm, "mid": v(47.22, -225.74) * mm, "end": v(47.26, -225.99) * mm});
            skArc(sketch, "E1396", {"start": v(47.26, -225.99) * mm, "mid": v(47.29, -226.15) * mm, "end": v(47.36, -226.3) * mm});
            skArc(sketch, "E1397", {"start": v(47.36, -226.3) * mm, "mid": v(47.47, -226.36) * mm, "end": v(47.59, -226.34) * mm});
            skArc(sketch, "E1398", {"start": v(47.59, -226.34) * mm, "mid": v(47.77, -226.22) * mm, "end": v(47.93, -226.05) * mm});
            skArc(sketch, "E1399", {"start": v(47.93, -226.05) * mm, "mid": v(48.14, -225.75) * mm, "end": v(48.34, -225.44) * mm});
            skArc(sketch, "E1400", {"start": v(48.34, -225.44) * mm, "mid": v(48.57, -225) * mm, "end": v(48.75, -224.53) * mm});
            skArc(sketch, "E1401", {"start": v(48.75, -224.53) * mm, "mid": v(48.85, -224.13) * mm, "end": v(48.87, -223.73) * mm});
            skArc(sketch, "E1402", {"start": v(48.87, -223.73) * mm, "mid": v(48.82, -223.34) * mm, "end": v(48.7, -222.98) * mm});
            skArc(sketch, "E1403", {"start": v(48.7, -222.98) * mm, "mid": v(48.48, -222.59) * mm, "end": v(48.22, -222.23) * mm});
            skArc(sketch, "E1404", {"start": v(48.22, -222.23) * mm, "mid": v(48, -221.93) * mm, "end": v(47.82, -221.61) * mm});
            skArc(sketch, "E1405", {"start": v(47.82, -221.61) * mm, "mid": v(47.68, -221.28) * mm, "end": v(47.59, -220.93) * mm});
            skArc(sketch, "E1406", {"start": v(47.59, -220.93) * mm, "mid": v(47.54, -220.6) * mm, "end": v(47.54, -220.28) * mm});
            skArc(sketch, "E1407", {"start": v(47.54, -220.28) * mm, "mid": v(47.59, -220.02) * mm, "end": v(47.7, -219.78) * mm});
            skArc(sketch, "E1408", {"start": v(47.7, -219.78) * mm, "mid": v(47.9, -219.39) * mm, "end": v(48.03, -218.96) * mm});
            skArc(sketch, "E1409", {"start": v(48.03, -218.96) * mm, "mid": v(47.96, -218.8) * mm, "end": v(47.79, -218.8) * mm});
            skArc(sketch, "E1410", {"start": v(47.79, -218.8) * mm, "mid": v(47.3, -219.15) * mm, "end": v(46.87, -219.57) * mm});
            skArc(sketch, "E1411", {"start": v(46.87, -219.57) * mm, "mid": v(46.3, -220.25) * mm, "end": v(45.78, -220.96) * mm});
            skArc(sketch, "E1412", {"start": v(47.23, -222.74) * mm, "mid": v(47.2, -222.93) * mm, "end": v(47.14, -223.12) * mm});
            skArc(sketch, "E1413", {"start": v(47.14, -223.12) * mm, "mid": v(47.05, -223.3) * mm, "end": v(46.91, -223.44) * mm});
            skArc(sketch, "E1414", {"start": v(46.91, -223.44) * mm, "mid": v(46.75, -223.57) * mm, "end": v(46.57, -223.66) * mm});
            skArc(sketch, "E1415", {"start": v(46.57, -223.66) * mm, "mid": v(46.37, -223.72) * mm, "end": v(46.17, -223.74) * mm});
            skArc(sketch, "E1416", {"start": v(46.17, -223.74) * mm, "mid": v(45.98, -223.72) * mm, "end": v(45.81, -223.66) * mm});
            skArc(sketch, "E1417", {"start": v(45.81, -223.66) * mm, "mid": v(45.69, -223.57) * mm, "end": v(45.6, -223.44) * mm});
            skArc(sketch, "E1418", {"start": v(45.6, -223.44) * mm, "mid": v(45.56, -223.28) * mm, "end": v(45.57, -223.12) * mm});
            skArc(sketch, "E1419", {"start": v(45.57, -223.12) * mm, "mid": v(45.63, -222.92) * mm, "end": v(45.73, -222.74) * mm});
            skArc(sketch, "E1420", {"start": v(45.73, -222.74) * mm, "mid": v(45.85, -222.54) * mm, "end": v(46, -222.35) * mm});
            skArc(sketch, "E1421", {"start": v(46, -222.35) * mm, "mid": v(46.14, -222.19) * mm, "end": v(46.3, -222.03) * mm});
            skArc(sketch, "E1422", {"start": v(46.3, -222.03) * mm, "mid": v(46.43, -221.91) * mm, "end": v(46.57, -221.8) * mm});
            skArc(sketch, "E1423", {"start": v(46.57, -221.8) * mm, "mid": v(46.67, -221.75) * mm, "end": v(46.78, -221.74) * mm});
            skArc(sketch, "E1424", {"start": v(46.78, -221.74) * mm, "mid": v(46.88, -221.76) * mm, "end": v(46.95, -221.81) * mm});
            skArc(sketch, "E1425", {"start": v(46.95, -221.81) * mm, "mid": v(47.03, -221.92) * mm, "end": v(47.1, -222.03) * mm});
            skArc(sketch, "E1426", {"start": v(47.1, -222.03) * mm, "mid": v(47.15, -222.2) * mm, "end": v(47.2, -222.35) * mm});
            skArc(sketch, "E1427", {"start": v(47.2, -222.35) * mm, "mid": v(47.22, -222.55) * mm, "end": v(47.23, -222.74) * mm});
            skArc(sketch, "E1428", {"start": v(52.86, -221.17) * mm, "mid": v(52.19, -222.23) * mm, "end": v(51.54, -223.3) * mm});
            skArc(sketch, "E1429", {"start": v(51.54, -223.3) * mm, "mid": v(51.37, -223.7) * mm, "end": v(51.35, -224.15) * mm});
            skArc(sketch, "E1430", {"start": v(51.35, -224.15) * mm, "mid": v(51.49, -224.46) * mm, "end": v(51.78, -224.61) * mm});
            skArc(sketch, "E1431", {"start": v(51.78, -224.61) * mm, "mid": v(52.5, -224.7) * mm, "end": v(53.23, -224.74) * mm});
            skArc(sketch, "E1432", {"start": v(53.23, -224.74) * mm, "mid": v(53.61, -224.76) * mm, "end": v(54, -224.83) * mm});
            skArc(sketch, "E1433", {"start": v(54, -224.83) * mm, "mid": v(54.33, -224.94) * mm, "end": v(54.64, -225.1) * mm});
            skArc(sketch, "E1434", {"start": v(54.64, -225.1) * mm, "mid": v(54.88, -225.29) * mm, "end": v(55.08, -225.51) * mm});
            skArc(sketch, "E1435", {"start": v(55.08, -225.51) * mm, "mid": v(55.2, -225.74) * mm, "end": v(55.24, -225.99) * mm});
            skArc(sketch, "E1436", {"start": v(55.24, -225.99) * mm, "mid": v(55.26, -226.24) * mm, "end": v(55.3, -226.5) * mm});
            skArc(sketch, "E1437", {"start": v(55.3, -226.5) * mm, "mid": v(55.35, -226.6) * mm, "end": v(55.46, -226.61) * mm});
            skArc(sketch, "E1438", {"start": v(55.46, -226.61) * mm, "mid": v(55.6, -226.56) * mm, "end": v(55.72, -226.45) * mm});
            skArc(sketch, "E1439", {"start": v(55.72, -226.45) * mm, "mid": v(55.94, -226.15) * mm, "end": v(56.15, -225.83) * mm});
            skArc(sketch, "E1440", {"start": v(56.15, -225.83) * mm, "mid": v(56.32, -225.52) * mm, "end": v(56.45, -225.18) * mm});
            skArc(sketch, "E1441", {"start": v(56.45, -225.18) * mm, "mid": v(56.55, -224.8) * mm, "end": v(56.62, -224.41) * mm});
            skArc(sketch, "E1442", {"start": v(56.62, -224.41) * mm, "mid": v(56.65, -224.03) * mm, "end": v(56.64, -223.64) * mm});
            skArc(sketch, "E1443", {"start": v(56.64, -223.64) * mm, "mid": v(56.6, -223.31) * mm, "end": v(56.5, -223) * mm});
            skArc(sketch, "E1444", {"start": v(56.5, -223) * mm, "mid": v(56.35, -222.64) * mm, "end": v(56.18, -222.3) * mm});
            skArc(sketch, "E1445", {"start": v(56.18, -222.3) * mm, "mid": v(56.06, -222.17) * mm, "end": v(55.9, -222.1) * mm});
            skArc(sketch, "E1446", {"start": v(55.9, -222.1) * mm, "mid": v(55.72, -222.14) * mm, "end": v(55.59, -222.24) * mm});
            skArc(sketch, "E1447", {"start": v(55.59, -222.24) * mm, "mid": v(55.35, -222.55) * mm, "end": v(55.14, -222.87) * mm});
            skArc(sketch, "E1448", {"start": v(55.14, -222.87) * mm, "mid": v(54.97, -223.1) * mm, "end": v(54.78, -223.32) * mm});
            skArc(sketch, "E1449", {"start": v(54.78, -223.32) * mm, "mid": v(54.59, -223.48) * mm, "end": v(54.37, -223.6) * mm});
            skArc(sketch, "E1450", {"start": v(54.37, -223.6) * mm, "mid": v(54.17, -223.64) * mm, "end": v(53.97, -223.64) * mm});
            skArc(sketch, "E1451", {"start": v(53.97, -223.64) * mm, "mid": v(53.79, -223.6) * mm, "end": v(53.64, -223.48) * mm});
            skArc(sketch, "E1452", {"start": v(53.64, -223.48) * mm, "mid": v(53.52, -223.3) * mm, "end": v(53.47, -223.1) * mm});
            skArc(sketch, "E1453", {"start": v(53.47, -223.1) * mm, "mid": v(53.47, -222.82) * mm, "end": v(53.52, -222.54) * mm});
            skArc(sketch, "E1454", {"start": v(53.52, -222.54) * mm, "mid": v(53.63, -222.2) * mm, "end": v(53.79, -221.88) * mm});
            skArc(sketch, "E1455", {"start": v(53.79, -221.88) * mm, "mid": v(54, -221.55) * mm, "end": v(54.23, -221.24) * mm});
            skArc(sketch, "E1456", {"start": v(54.23, -221.24) * mm, "mid": v(54.46, -220.93) * mm, "end": v(54.68, -220.6) * mm});
            skArc(sketch, "E1457", {"start": v(54.68, -220.6) * mm, "mid": v(54.85, -220.3) * mm, "end": v(54.98, -220) * mm});
            skArc(sketch, "E1458", {"start": v(54.98, -220) * mm, "mid": v(55.06, -219.74) * mm, "end": v(55.1, -219.49) * mm});
            skArc(sketch, "E1459", {"start": v(55.1, -219.49) * mm, "mid": v(55.1, -219.32) * mm, "end": v(55, -219.18) * mm});
            skArc(sketch, "E1460", {"start": v(55, -219.18) * mm, "mid": v(54.86, -219.11) * mm, "end": v(54.7, -219.15) * mm});
            skArc(sketch, "E1461", {"start": v(54.7, -219.15) * mm, "mid": v(54.42, -219.34) * mm, "end": v(54.17, -219.56) * mm});
            skArc(sketch, "E1462", {"start": v(54.17, -219.56) * mm, "mid": v(53.83, -219.9) * mm, "end": v(53.52, -220.25) * mm});
            skArc(sketch, "E1463", {"start": v(53.52, -220.25) * mm, "mid": v(53.18, -220.7) * mm, "end": v(52.86, -221.17) * mm});
            skArc(sketch, "E1464", {"start": v(89.73, -222.74) * mm, "mid": v(89.74, -223.82) * mm, "end": v(89.8, -224.9) * mm});
            skArc(sketch, "E1465", {"start": v(89.8, -224.9) * mm, "mid": v(89.9, -225.46) * mm, "end": v(90.1, -225.98) * mm});
            skArc(sketch, "E1466", {"start": v(90.1, -225.98) * mm, "mid": v(90.35, -226.3) * mm, "end": v(90.7, -226.5) * mm});
            skArc(sketch, "E1467", {"start": v(90.7, -226.5) * mm, "mid": v(91.2, -226.63) * mm, "end": v(91.73, -226.66) * mm});
            skArc(sketch, "E1468", {"start": v(91.73, -226.66) * mm, "mid": v(92.08, -226.64) * mm, "end": v(92.43, -226.6) * mm});
            skArc(sketch, "E1469", {"start": v(92.43, -226.6) * mm, "mid": v(92.6, -226.55) * mm, "end": v(92.77, -226.45) * mm});
            skArc(sketch, "E1470", {"start": v(92.77, -226.45) * mm, "mid": v(92.82, -226.37) * mm, "end": v(92.78, -226.27) * mm});
            skArc(sketch, "E1471", {"start": v(92.78, -226.27) * mm, "mid": v(92.64, -226.16) * mm, "end": v(92.48, -226.08) * mm});
            skArc(sketch, "E1472", {"start": v(92.48, -226.08) * mm, "mid": v(92.2, -225.9) * mm, "end": v(92, -225.65) * mm});
            skArc(sketch, "E1473", {"start": v(92, -225.65) * mm, "mid": v(91.77, -225.2) * mm, "end": v(91.6, -224.72) * mm});
            skArc(sketch, "E1474", {"start": v(91.6, -224.72) * mm, "mid": v(91.43, -224.11) * mm, "end": v(91.32, -223.5) * mm});
            skArc(sketch, "E1475", {"start": v(91.32, -223.5) * mm, "mid": v(91.25, -222.83) * mm, "end": v(91.23, -222.15) * mm});
            skArc(sketch, "E1476", {"start": v(91.23, -222.15) * mm, "mid": v(91.21, -221.5) * mm, "end": v(91.17, -220.84) * mm});
            skArc(sketch, "E1477", {"start": v(91.17, -220.84) * mm, "mid": v(91.1, -220.3) * mm, "end": v(91, -219.74) * mm});
            skArc(sketch, "E1478", {"start": v(91, -219.74) * mm, "mid": v(90.9, -219.34) * mm, "end": v(90.77, -218.94) * mm});
            skArc(sketch, "E1479", {"start": v(90.77, -218.94) * mm, "mid": v(90.65, -218.8) * mm, "end": v(90.48, -218.74) * mm});
            skArc(sketch, "E1480", {"start": v(90.48, -218.74) * mm, "mid": v(90.3, -218.8) * mm, "end": v(90.18, -218.95) * mm});
            skArc(sketch, "E1481", {"start": v(90.18, -218.95) * mm, "mid": v(90.05, -219.43) * mm, "end": v(89.95, -219.91) * mm});
            skArc(sketch, "E1482", {"start": v(89.95, -219.91) * mm, "mid": v(89.84, -220.56) * mm, "end": v(89.78, -221.2) * mm});
            skArc(sketch, "E1483", {"start": v(89.78, -221.2) * mm, "mid": v(89.74, -221.97) * mm, "end": v(89.73, -222.74) * mm});
            skArc(sketch, "E1484", {"start": v(-22.7, -220.7) * mm, "mid": v(-22.96, -220.9) * mm, "end": v(-23.16, -221.16) * mm});
            skArc(sketch, "E1485", {"start": v(-23.16, -221.16) * mm, "mid": v(-23.34, -221.54) * mm, "end": v(-23.48, -221.94) * mm});
            skArc(sketch, "E1486", {"start": v(-23.48, -221.94) * mm, "mid": v(-23.6, -222.4) * mm, "end": v(-23.65, -222.88) * mm});
            skArc(sketch, "E1487", {"start": v(-23.65, -222.88) * mm, "mid": v(-23.65, -223.37) * mm, "end": v(-23.61, -223.85) * mm});
            skArc(sketch, "E1488", {"start": v(-23.61, -223.85) * mm, "mid": v(-23.33, -224.83) * mm, "end": v(-22.79, -225.69) * mm});
            skArc(sketch, "E1489", {"start": v(-22.79, -225.69) * mm, "mid": v(-22.1, -226.2) * mm, "end": v(-21.26, -226.35) * mm});
            skArc(sketch, "E1490", {"start": v(-21.26, -226.35) * mm, "mid": v(-20.41, -226.12) * mm, "end": v(-19.74, -225.54) * mm});
            skArc(sketch, "E1491", {"start": v(-19.74, -225.54) * mm, "mid": v(-19.23, -224.63) * mm, "end": v(-18.97, -223.62) * mm});
            skArc(sketch, "E1492", {"start": v(-18.97, -223.62) * mm, "mid": v(-18.95, -222.72) * mm, "end": v(-19.1, -221.83) * mm});
            skArc(sketch, "E1493", {"start": v(-19.1, -221.83) * mm, "mid": v(-19.4, -221.16) * mm, "end": v(-19.9, -220.61) * mm});
            skArc(sketch, "E1494", {"start": v(-19.9, -220.61) * mm, "mid": v(-20.52, -220.3) * mm, "end": v(-21.2, -220.21) * mm});
            skArc(sketch, "E1495", {"start": v(-21.2, -220.21) * mm, "mid": v(-21.98, -220.36) * mm, "end": v(-22.7, -220.7) * mm});
            skArc(sketch, "E1496", {"start": v(-19.77, -223.8) * mm, "mid": v(-19.8, -224.17) * mm, "end": v(-19.89, -224.54) * mm});
            skArc(sketch, "E1497", {"start": v(-19.89, -224.54) * mm, "mid": v(-20.02, -224.87) * mm, "end": v(-20.21, -225.17) * mm});
            skArc(sketch, "E1498", {"start": v(-20.21, -225.17) * mm, "mid": v(-20.44, -225.4) * mm, "end": v(-20.7, -225.59) * mm});
            skArc(sketch, "E1499", {"start": v(-20.7, -225.59) * mm, "mid": v(-20.98, -225.7) * mm, "end": v(-21.27, -225.74) * mm});
            skArc(sketch, "E1500", {"start": v(-21.27, -225.74) * mm, "mid": v(-21.78, -225.62) * mm, "end": v(-22.18, -225.28) * mm});
            skArc(sketch, "E1501", {"start": v(-22.18, -225.28) * mm, "mid": v(-22.52, -224.7) * mm, "end": v(-22.72, -224.05) * mm});
            skArc(sketch, "E1502", {"start": v(-22.72, -224.05) * mm, "mid": v(-22.8, -223.3) * mm, "end": v(-22.73, -222.56) * mm});
            skArc(sketch, "E1503", {"start": v(-22.73, -222.56) * mm, "mid": v(-22.52, -221.95) * mm, "end": v(-22.13, -221.43) * mm});
            skArc(sketch, "E1504", {"start": v(-22.13, -221.43) * mm, "mid": v(-21.78, -221.2) * mm, "end": v(-21.35, -221.11) * mm});
            skArc(sketch, "E1505", {"start": v(-21.35, -221.11) * mm, "mid": v(-20.92, -221.2) * mm, "end": v(-20.56, -221.44) * mm});
            skArc(sketch, "E1506", {"start": v(-20.56, -221.44) * mm, "mid": v(-20.2, -221.9) * mm, "end": v(-19.97, -222.43) * mm});
            skArc(sketch, "E1507", {"start": v(-19.97, -222.43) * mm, "mid": v(-19.82, -223.1) * mm, "end": v(-19.77, -223.8) * mm});
            skArc(sketch, "E1508", {"start": v(-15.61, -220.62) * mm, "mid": v(-16.22, -221.19) * mm, "end": v(-16.57, -221.95) * mm});
            skArc(sketch, "E1509", {"start": v(-16.57, -221.95) * mm, "mid": v(-16.7, -222.93) * mm, "end": v(-16.6, -223.9) * mm});
            skArc(sketch, "E1510", {"start": v(-16.6, -223.9) * mm, "mid": v(-16.26, -224.84) * mm, "end": v(-15.72, -225.66) * mm});
            skArc(sketch, "E1511", {"start": v(-15.72, -225.66) * mm, "mid": v(-15.07, -226.18) * mm, "end": v(-14.27, -226.42) * mm});
            skArc(sketch, "E1512", {"start": v(-14.27, -226.42) * mm, "mid": v(-13.68, -226.48) * mm, "end": v(-13.09, -226.54) * mm});
            skArc(sketch, "E1513", {"start": v(-13.09, -226.54) * mm, "mid": v(-13.03, -226.53) * mm, "end": v(-12.99, -226.49) * mm});
            skArc(sketch, "E1514", {"start": v(-12.99, -226.49) * mm, "mid": v(-12.99, -226.44) * mm, "end": v(-13.02, -226.4) * mm});
            skArc(sketch, "E1515", {"start": v(-13.02, -226.4) * mm, "mid": v(-13.55, -226.25) * mm, "end": v(-14.08, -226.1) * mm});
            skArc(sketch, "E1516", {"start": v(-14.08, -226.1) * mm, "mid": v(-14.74, -225.74) * mm, "end": v(-15.2, -225.15) * mm});
            skArc(sketch, "E1517", {"start": v(-15.2, -225.15) * mm, "mid": v(-15.5, -224.3) * mm, "end": v(-15.58, -223.4) * mm});
            skArc(sketch, "E1518", {"start": v(-15.58, -223.4) * mm, "mid": v(-15.43, -222.63) * mm, "end": v(-15.06, -221.94) * mm});
            skArc(sketch, "E1519", {"start": v(-15.06, -221.94) * mm, "mid": v(-14.55, -221.56) * mm, "end": v(-13.93, -221.51) * mm});
            skArc(sketch, "E1520", {"start": v(-13.93, -221.51) * mm, "mid": v(-13.7, -221.54) * mm, "end": v(-13.47, -221.54) * mm});
            skArc(sketch, "E1521", {"start": v(-13.47, -221.54) * mm, "mid": v(-13.32, -221.5) * mm, "end": v(-13.2, -221.4) * mm});
            skArc(sketch, "E1522", {"start": v(-13.2, -221.4) * mm, "mid": v(-13.12, -221.28) * mm, "end": v(-13.12, -221.13) * mm});
            skArc(sketch, "E1523", {"start": v(-13.12, -221.13) * mm, "mid": v(-13.17, -220.94) * mm, "end": v(-13.26, -220.76) * mm});
            skArc(sketch, "E1524", {"start": v(-13.26, -220.76) * mm, "mid": v(-13.5, -220.38) * mm, "end": v(-13.77, -220) * mm});
            skArc(sketch, "E1525", {"start": v(-13.77, -220) * mm, "mid": v(-13.9, -219.88) * mm, "end": v(-14.09, -219.83) * mm});
            skArc(sketch, "E1526", {"start": v(-14.09, -219.83) * mm, "mid": v(-14.3, -219.85) * mm, "end": v(-14.49, -219.93) * mm});
            skArc(sketch, "E1527", {"start": v(-14.49, -219.93) * mm, "mid": v(-15.05, -220.27) * mm, "end": v(-15.61, -220.62) * mm});
            skArc(sketch, "E1528", {"start": v(-0.65, -221.02) * mm, "mid": v(-1.16, -221.66) * mm, "end": v(-1.51, -222.4) * mm});
            skArc(sketch, "E1529", {"start": v(-1.51, -222.4) * mm, "mid": v(-1.7, -223.21) * mm, "end": v(-1.72, -224.06) * mm});
            skArc(sketch, "E1530", {"start": v(-1.72, -224.06) * mm, "mid": v(-1.57, -224.82) * mm, "end": v(-1.25, -225.53) * mm});
            skArc(sketch, "E1531", {"start": v(-1.25, -225.53) * mm, "mid": v(-0.8, -226.05) * mm, "end": v(-0.2, -226.4) * mm});
            skArc(sketch, "E1532", {"start": v(-0.2, -226.4) * mm, "mid": v(0.13, -226.5) * mm, "end": v(0.47, -226.55) * mm});
            skArc(sketch, "E1533", {"start": v(0.47, -226.55) * mm, "mid": v(0.84, -226.56) * mm, "end": v(1.2, -226.52) * mm});
            skArc(sketch, "E1534", {"start": v(1.2, -226.52) * mm, "mid": v(1.55, -226.44) * mm, "end": v(1.89, -226.32) * mm});
            skArc(sketch, "E1535", {"start": v(1.89, -226.32) * mm, "mid": v(2.16, -226.16) * mm, "end": v(2.4, -225.96) * mm});
            skArc(sketch, "E1536", {"start": v(2.4, -225.96) * mm, "mid": v(2.6, -225.74) * mm, "end": v(2.77, -225.5) * mm});
            skArc(sketch, "E1537", {"start": v(2.77, -225.5) * mm, "mid": v(2.8, -225.35) * mm, "end": v(2.74, -225.21) * mm});
            skArc(sketch, "E1538", {"start": v(2.74, -225.21) * mm, "mid": v(2.59, -225.1) * mm, "end": v(2.4, -225.06) * mm});
            skArc(sketch, "E1539", {"start": v(2.4, -225.06) * mm, "mid": v(1.99, -225.06) * mm, "end": v(1.58, -225.08) * mm});
            skArc(sketch, "E1540", {"start": v(1.58, -225.08) * mm, "mid": v(1.17, -225.08) * mm, "end": v(0.77, -225.02) * mm});
            skArc(sketch, "E1541", {"start": v(0.77, -225.02) * mm, "mid": v(0.46, -224.9) * mm, "end": v(0.19, -224.7) * mm});
            skArc(sketch, "E1542", {"start": v(0.19, -224.7) * mm, "mid": v(-0.02, -224.43) * mm, "end": v(-0.16, -224.1) * mm});
            skArc(sketch, "E1543", {"start": v(-0.16, -224.1) * mm, "mid": v(-0.25, -223.68) * mm, "end": v(-0.27, -223.24) * mm});
            skArc(sketch, "E1544", {"start": v(-0.27, -223.24) * mm, "mid": v(-0.25, -222.8) * mm, "end": v(-0.17, -222.37) * mm});
            skArc(sketch, "E1545", {"start": v(-0.17, -222.37) * mm, "mid": v(-0.04, -222.06) * mm, "end": v(0.16, -221.8) * mm});
            skArc(sketch, "E1546", {"start": v(0.16, -221.8) * mm, "mid": v(0.41, -221.62) * mm, "end": v(0.7, -221.53) * mm});
            skArc(sketch, "E1547", {"start": v(0.7, -221.53) * mm, "mid": v(1.1, -221.5) * mm, "end": v(1.48, -221.53) * mm});
            skArc(sketch, "E1548", {"start": v(1.48, -221.53) * mm, "mid": v(2.12, -221.62) * mm, "end": v(2.77, -221.67) * mm});
            skArc(sketch, "E1549", {"start": v(2.77, -221.67) * mm, "mid": v(3.02, -221.6) * mm, "end": v(3.17, -221.39) * mm});
            skArc(sketch, "E1550", {"start": v(3.17, -221.39) * mm, "mid": v(3.17, -221.14) * mm, "end": v(3, -220.95) * mm});
            skArc(sketch, "E1551", {"start": v(3, -220.95) * mm, "mid": v(2.43, -220.67) * mm, "end": v(1.85, -220.42) * mm});
            skArc(sketch, "E1552", {"start": v(1.85, -220.42) * mm, "mid": v(1.55, -220.34) * mm, "end": v(1.24, -220.3) * mm});
            skArc(sketch, "E1553", {"start": v(1.24, -220.3) * mm, "mid": v(0.89, -220.32) * mm, "end": v(0.54, -220.38) * mm});
            skArc(sketch, "E1554", {"start": v(0.54, -220.38) * mm, "mid": v(0.2, -220.48) * mm, "end": v(-0.12, -220.63) * mm});
            skArc(sketch, "E1555", {"start": v(-0.12, -220.63) * mm, "mid": v(-0.4, -220.8) * mm, "end": v(-0.65, -221.02) * mm});
            skArc(sketch, "E1556", {"start": v(14.9, -223.03) * mm, "mid": v(15.19, -224.5) * mm, "end": v(15.48, -225.97) * mm});
            skArc(sketch, "E1557", {"start": v(15.48, -225.97) * mm, "mid": v(15.58, -226.2) * mm, "end": v(15.77, -226.36) * mm});
            skArc(sketch, "E1558", {"start": v(15.77, -226.36) * mm, "mid": v(15.94, -226.36) * mm, "end": v(16.05, -226.22) * mm});
            skArc(sketch, "E1559", {"start": v(16.05, -226.22) * mm, "mid": v(16.24, -225.02) * mm, "end": v(16.43, -223.82) * mm});
            skArc(sketch, "E1560", {"start": v(16.43, -223.82) * mm, "mid": v(16.5, -223.18) * mm, "end": v(16.53, -222.53) * mm});
            skArc(sketch, "E1561", {"start": v(16.53, -222.53) * mm, "mid": v(16.5, -222) * mm, "end": v(16.4, -221.48) * mm});
            skArc(sketch, "E1562", {"start": v(16.4, -221.48) * mm, "mid": v(16.28, -221.1) * mm, "end": v(16.09, -220.73) * mm});
            skArc(sketch, "E1563", {"start": v(16.09, -220.73) * mm, "mid": v(15.87, -220.49) * mm, "end": v(15.58, -220.32) * mm});
            skArc(sketch, "E1564", {"start": v(15.58, -220.32) * mm, "mid": v(15.3, -220.27) * mm, "end": v(15.03, -220.3) * mm});
            skArc(sketch, "E1565", {"start": v(15.03, -220.3) * mm, "mid": v(14.83, -220.43) * mm, "end": v(14.71, -220.65) * mm});
            skArc(sketch, "E1566", {"start": v(14.71, -220.65) * mm, "mid": v(14.65, -221.06) * mm, "end": v(14.66, -221.48) * mm});
            skArc(sketch, "E1567", {"start": v(14.66, -221.48) * mm, "mid": v(14.77, -222.26) * mm, "end": v(14.9, -223.03) * mm});
            skArc(sketch, "E1568", {"start": v(-101.66, -222.24) * mm, "mid": v(-101.66, -222.68) * mm, "end": v(-101.62, -223.11) * mm});
            skArc(sketch, "E1569", {"start": v(-101.62, -223.11) * mm, "mid": v(-101.55, -223.6) * mm, "end": v(-101.44, -224.08) * mm});
            skArc(sketch, "E1570", {"start": v(-101.44, -224.08) * mm, "mid": v(-101.32, -224.55) * mm, "end": v(-101.16, -225) * mm});
            skArc(sketch, "E1571", {"start": v(-101.16, -225) * mm, "mid": v(-101, -225.37) * mm, "end": v(-100.81, -225.71) * mm});
            skArc(sketch, "E1572", {"start": v(-100.81, -225.71) * mm, "mid": v(-100.57, -226.06) * mm, "end": v(-100.29, -226.37) * mm});
            skArc(sketch, "E1573", {"start": v(-100.29, -226.37) * mm, "mid": v(-100.1, -226.47) * mm, "end": v(-99.89, -226.44) * mm});
            skArc(sketch, "E1574", {"start": v(-99.89, -226.44) * mm, "mid": v(-99.66, -226.27) * mm, "end": v(-99.5, -226.04) * mm});
            skArc(sketch, "E1575", {"start": v(-99.5, -226.04) * mm, "mid": v(-99.23, -225.42) * mm, "end": v(-98.99, -224.79) * mm});
            skLineSegment(sketch, "E1576", {"start": v(-98.99, -224.79) * mm, "end": v(-98.1, -222.39) * mm});
            skLineSegment(sketch, "E1577", {"start": v(-98.1, -222.39) * mm, "end": v(-97.48, -224.77) * mm});
            skArc(sketch, "E1578", {"start": v(-97.48, -224.77) * mm, "mid": v(-97.35, -225.2) * mm, "end": v(-97.2, -225.64) * mm});
            skArc(sketch, "E1579", {"start": v(-97.2, -225.64) * mm, "mid": v(-97.04, -225.96) * mm, "end": v(-96.86, -226.27) * mm});
            skArc(sketch, "E1580", {"start": v(-96.86, -226.27) * mm, "mid": v(-96.7, -226.44) * mm, "end": v(-96.52, -226.57) * mm});
            skArc(sketch, "E1581", {"start": v(-96.52, -226.57) * mm, "mid": v(-96.37, -226.6) * mm, "end": v(-96.24, -226.53) * mm});
            skArc(sketch, "E1582", {"start": v(-96.24, -226.53) * mm, "mid": v(-96.12, -226.34) * mm, "end": v(-96.09, -226.12) * mm});
            skArc(sketch, "E1583", {"start": v(-96.09, -226.12) * mm, "mid": v(-96.14, -225.7) * mm, "end": v(-96.23, -225.28) * mm});
            skArc(sketch, "E1584", {"start": v(-96.23, -225.28) * mm, "mid": v(-96.37, -224.76) * mm, "end": v(-96.56, -224.25) * mm});
            skArc(sketch, "E1585", {"start": v(-96.56, -224.25) * mm, "mid": v(-96.8, -223.69) * mm, "end": v(-97.07, -223.14) * mm});
            skLineSegment(sketch, "E1586", {"start": v(-97.07, -223.14) * mm, "end": v(-98.52, -220.37) * mm});
            skLineSegment(sketch, "E1587", {"start": v(-98.52, -220.37) * mm, "end": v(-99.32, -222.8) * mm});
            skLineSegment(sketch, "E1588", {"start": v(-99.32, -222.8) * mm, "end": v(-100.13, -225.24) * mm});
            skLineSegment(sketch, "E1589", {"start": v(-100.13, -225.24) * mm, "end": v(-100.85, -222.74) * mm});
            skArc(sketch, "E1590", {"start": v(-100.85, -222.74) * mm, "mid": v(-101.05, -222.05) * mm, "end": v(-101.26, -221.37) * mm});
            skArc(sketch, "E1591", {"start": v(-101.26, -221.37) * mm, "mid": v(-101.33, -221.23) * mm, "end": v(-101.45, -221.13) * mm});
            skArc(sketch, "E1592", {"start": v(-101.45, -221.13) * mm, "mid": v(-101.54, -221.12) * mm, "end": v(-101.6, -221.2) * mm});
            skArc(sketch, "E1593", {"start": v(-101.6, -221.2) * mm, "mid": v(-101.63, -221.72) * mm, "end": v(-101.66, -222.24) * mm});
            skArc(sketch, "E1594", {"start": v(-95.7, -222.32) * mm, "mid": v(-95.67, -222.7) * mm, "end": v(-95.64, -223.07) * mm});
            skArc(sketch, "E1595", {"start": v(-95.64, -223.07) * mm, "mid": v(-95.6, -223.23) * mm, "end": v(-95.5, -223.36) * mm});
            skArc(sketch, "E1596", {"start": v(-95.5, -223.36) * mm, "mid": v(-95.4, -223.4) * mm, "end": v(-95.31, -223.34) * mm});
            skArc(sketch, "E1597", {"start": v(-95.31, -223.34) * mm, "mid": v(-95.2, -223.14) * mm, "end": v(-95.1, -222.93) * mm});
            skArc(sketch, "E1598", {"start": v(-95.1, -222.93) * mm, "mid": v(-95, -222.66) * mm, "end": v(-94.94, -222.38) * mm});
            skArc(sketch, "E1599", {"start": v(-94.94, -222.38) * mm, "mid": v(-94.9, -222.1) * mm, "end": v(-94.9, -221.82) * mm});
            skArc(sketch, "E1600", {"start": v(-94.9, -221.82) * mm, "mid": v(-94.92, -221.58) * mm, "end": v(-94.98, -221.34) * mm});
            skArc(sketch, "E1601", {"start": v(-94.98, -221.34) * mm, "mid": v(-95.05, -221.16) * mm, "end": v(-95.17, -221) * mm});
            skArc(sketch, "E1602", {"start": v(-95.17, -221) * mm, "mid": v(-95.27, -220.95) * mm, "end": v(-95.39, -220.96) * mm});
            skArc(sketch, "E1603", {"start": v(-95.39, -220.96) * mm, "mid": v(-95.5, -221.03) * mm, "end": v(-95.57, -221.14) * mm});
            skArc(sketch, "E1604", {"start": v(-95.57, -221.14) * mm, "mid": v(-95.65, -221.38) * mm, "end": v(-95.68, -221.62) * mm});
            skArc(sketch, "E1605", {"start": v(-95.68, -221.62) * mm, "mid": v(-95.7, -221.97) * mm, "end": v(-95.7, -222.32) * mm});
            skArc(sketch, "E1606", {"start": v(-93.26, -222.19) * mm, "mid": v(-92.7, -223.98) * mm, "end": v(-92.1, -225.76) * mm});
            skArc(sketch, "E1607", {"start": v(-92.1, -225.76) * mm, "mid": v(-91.93, -226.1) * mm, "end": v(-91.66, -226.37) * mm});
            skArc(sketch, "E1608", {"start": v(-91.66, -226.37) * mm, "mid": v(-91.4, -226.42) * mm, "end": v(-91.18, -226.27) * mm});
            skArc(sketch, "E1609", {"start": v(-91.18, -226.27) * mm, "mid": v(-90.64, -225.34) * mm, "end": v(-90.12, -224.4) * mm});
            skArc(sketch, "E1610", {"start": v(-90.12, -224.4) * mm, "mid": v(-89.84, -223.84) * mm, "end": v(-89.58, -223.27) * mm});
            skArc(sketch, "E1611", {"start": v(-89.58, -223.27) * mm, "mid": v(-89.39, -222.76) * mm, "end": v(-89.22, -222.23) * mm});
            skArc(sketch, "E1612", {"start": v(-89.22, -222.23) * mm, "mid": v(-89.12, -221.81) * mm, "end": v(-89.05, -221.39) * mm});
            skArc(sketch, "E1613", {"start": v(-89.05, -221.39) * mm, "mid": v(-89.07, -221.18) * mm, "end": v(-89.17, -221) * mm});
            skArc(sketch, "E1614", {"start": v(-89.17, -221) * mm, "mid": v(-89.31, -220.94) * mm, "end": v(-89.46, -220.97) * mm});
            skArc(sketch, "E1615", {"start": v(-89.46, -220.97) * mm, "mid": v(-89.67, -221.13) * mm, "end": v(-89.85, -221.31) * mm});
            skArc(sketch, "E1616", {"start": v(-89.85, -221.31) * mm, "mid": v(-90.08, -221.63) * mm, "end": v(-90.28, -221.96) * mm});
            skArc(sketch, "E1617", {"start": v(-90.28, -221.96) * mm, "mid": v(-90.5, -222.4) * mm, "end": v(-90.69, -222.84) * mm});
            skArc(sketch, "E1618", {"start": v(-90.69, -222.84) * mm, "mid": v(-90.9, -223.37) * mm, "end": v(-91.14, -223.9) * mm});
            skArc(sketch, "E1619", {"start": v(-91.14, -223.9) * mm, "mid": v(-91.26, -224.1) * mm, "end": v(-91.43, -224.24) * mm});
            skArc(sketch, "E1620", {"start": v(-91.43, -224.24) * mm, "mid": v(-91.55, -224.26) * mm, "end": v(-91.63, -224.17) * mm});
            skArc(sketch, "E1621", {"start": v(-91.63, -224.17) * mm, "mid": v(-91.68, -223.86) * mm, "end": v(-91.71, -223.55) * mm});
            skArc(sketch, "E1622", {"start": v(-91.71, -223.55) * mm, "mid": v(-91.74, -223.2) * mm, "end": v(-91.8, -222.85) * mm});
            skArc(sketch, "E1623", {"start": v(-91.8, -222.85) * mm, "mid": v(-91.91, -222.5) * mm, "end": v(-92.05, -222.17) * mm});
            skArc(sketch, "E1624", {"start": v(-92.05, -222.17) * mm, "mid": v(-92.2, -221.88) * mm, "end": v(-92.38, -221.6) * mm});
            skArc(sketch, "E1625", {"start": v(-92.38, -221.6) * mm, "mid": v(-92.55, -221.4) * mm, "end": v(-92.76, -221.24) * mm});
            skArc(sketch, "E1626", {"start": v(-92.76, -221.24) * mm, "mid": v(-92.92, -221.17) * mm, "end": v(-93.1, -221.14) * mm});
            skArc(sketch, "E1627", {"start": v(-93.1, -221.14) * mm, "mid": v(-93.23, -221.17) * mm, "end": v(-93.32, -221.26) * mm});
            skArc(sketch, "E1628", {"start": v(-93.32, -221.26) * mm, "mid": v(-93.38, -221.44) * mm, "end": v(-93.39, -221.62) * mm});
            skArc(sketch, "E1629", {"start": v(-93.39, -221.62) * mm, "mid": v(-93.34, -221.9) * mm, "end": v(-93.26, -222.19) * mm});
            skArc(sketch, "E1630", {"start": v(-84.14, -223.24) * mm, "mid": v(-83.89, -224.35) * mm, "end": v(-83.62, -225.45) * mm});
            skArc(sketch, "E1631", {"start": v(-83.62, -225.45) * mm, "mid": v(-83.44, -225.97) * mm, "end": v(-83.2, -226.46) * mm});
            skArc(sketch, "E1632", {"start": v(-83.2, -226.46) * mm, "mid": v(-83, -226.65) * mm, "end": v(-82.74, -226.72) * mm});
            skArc(sketch, "E1633", {"start": v(-82.74, -226.72) * mm, "mid": v(-82.45, -226.66) * mm, "end": v(-82.2, -226.5) * mm});
            skArc(sketch, "E1634", {"start": v(-82.2, -226.5) * mm, "mid": v(-82.08, -226.31) * mm, "end": v(-82.07, -226.1) * mm});
            skArc(sketch, "E1635", {"start": v(-82.07, -226.1) * mm, "mid": v(-82.14, -225.67) * mm, "end": v(-82.25, -225.25) * mm});
            skArc(sketch, "E1636", {"start": v(-82.25, -225.25) * mm, "mid": v(-82.43, -224.72) * mm, "end": v(-82.64, -224.2) * mm});
            skArc(sketch, "E1637", {"start": v(-82.64, -224.2) * mm, "mid": v(-82.9, -223.63) * mm, "end": v(-83.2, -223.08) * mm});
            skLineSegment(sketch, "E1638", {"start": v(-83.2, -223.08) * mm, "end": v(-84.78, -220.24) * mm});
            skLineSegment(sketch, "E1639", {"start": v(-84.78, -220.24) * mm, "end": v(-84.14, -223.24) * mm});
            skArc(sketch, "E1640", {"start": v(-81.77, -222.24) * mm, "mid": v(-81.76, -222.53) * mm, "end": v(-81.7, -222.81) * mm});
            skArc(sketch, "E1641", {"start": v(-81.7, -222.81) * mm, "mid": v(-81.61, -223.06) * mm, "end": v(-81.48, -223.3) * mm});
            skArc(sketch, "E1642", {"start": v(-81.48, -223.3) * mm, "mid": v(-81.33, -223.48) * mm, "end": v(-81.16, -223.62) * mm});
            skArc(sketch, "E1643", {"start": v(-81.16, -223.62) * mm, "mid": v(-80.97, -223.7) * mm, "end": v(-80.77, -223.74) * mm});
            skArc(sketch, "E1644", {"start": v(-80.77, -223.74) * mm, "mid": v(-80.58, -223.7) * mm, "end": v(-80.4, -223.62) * mm});
            skArc(sketch, "E1645", {"start": v(-80.4, -223.62) * mm, "mid": v(-80.21, -223.48) * mm, "end": v(-80.07, -223.3) * mm});
            skArc(sketch, "E1646", {"start": v(-80.07, -223.3) * mm, "mid": v(-79.94, -223.06) * mm, "end": v(-79.85, -222.81) * mm});
            skArc(sketch, "E1647", {"start": v(-79.85, -222.81) * mm, "mid": v(-79.8, -222.53) * mm, "end": v(-79.77, -222.24) * mm});
            skArc(sketch, "E1648", {"start": v(-79.77, -222.24) * mm, "mid": v(-79.8, -221.95) * mm, "end": v(-79.85, -221.66) * mm});
            skArc(sketch, "E1649", {"start": v(-79.85, -221.66) * mm, "mid": v(-79.94, -221.41) * mm, "end": v(-80.07, -221.18) * mm});
            skArc(sketch, "E1650", {"start": v(-80.07, -221.18) * mm, "mid": v(-80.21, -221) * mm, "end": v(-80.4, -220.85) * mm});
            skArc(sketch, "E1651", {"start": v(-80.4, -220.85) * mm, "mid": v(-80.58, -220.77) * mm, "end": v(-80.77, -220.74) * mm});
            skArc(sketch, "E1652", {"start": v(-80.77, -220.74) * mm, "mid": v(-80.97, -220.77) * mm, "end": v(-81.16, -220.85) * mm});
            skArc(sketch, "E1653", {"start": v(-81.16, -220.85) * mm, "mid": v(-81.33, -221) * mm, "end": v(-81.48, -221.18) * mm});
            skArc(sketch, "E1654", {"start": v(-81.48, -221.18) * mm, "mid": v(-81.61, -221.41) * mm, "end": v(-81.7, -221.66) * mm});
            skArc(sketch, "E1655", {"start": v(-81.7, -221.66) * mm, "mid": v(-81.76, -221.95) * mm, "end": v(-81.77, -222.24) * mm});
            skArc(sketch, "E1656", {"start": v(-78.65, -223.36) * mm, "mid": v(-78.87, -223.88) * mm, "end": v(-79.07, -224.4) * mm});
            skArc(sketch, "E1657", {"start": v(-79.07, -224.4) * mm, "mid": v(-79.22, -224.89) * mm, "end": v(-79.35, -225.37) * mm});
            skArc(sketch, "E1658", {"start": v(-79.35, -225.37) * mm, "mid": v(-79.42, -225.76) * mm, "end": v(-79.47, -226.15) * mm});
            skArc(sketch, "E1659", {"start": v(-79.47, -226.15) * mm, "mid": v(-79.44, -226.34) * mm, "end": v(-79.34, -226.5) * mm});
            skArc(sketch, "E1660", {"start": v(-79.34, -226.5) * mm, "mid": v(-79.2, -226.56) * mm, "end": v(-79.07, -226.51) * mm});
            skArc(sketch, "E1661", {"start": v(-79.07, -226.51) * mm, "mid": v(-78.86, -226.3) * mm, "end": v(-78.67, -226.05) * mm});
            skArc(sketch, "E1662", {"start": v(-78.67, -226.05) * mm, "mid": v(-78.43, -225.67) * mm, "end": v(-78.22, -225.27) * mm});
            skArc(sketch, "E1663", {"start": v(-78.22, -225.27) * mm, "mid": v(-77.98, -224.76) * mm, "end": v(-77.77, -224.24) * mm});
            skArc(sketch, "E1664", {"start": v(-77.77, -224.24) * mm, "mid": v(-77.34, -223.06) * mm, "end": v(-76.94, -221.86) * mm});
            skArc(sketch, "E1665", {"start": v(-76.94, -221.86) * mm, "mid": v(-76.93, -221.5) * mm, "end": v(-77.11, -221.16) * mm});
            skArc(sketch, "E1666", {"start": v(-77.11, -221.16) * mm, "mid": v(-77.37, -221.08) * mm, "end": v(-77.6, -221.24) * mm});
            skArc(sketch, "E1667", {"start": v(-77.6, -221.24) * mm, "mid": v(-78.14, -222.3) * mm, "end": v(-78.65, -223.36) * mm});
            skArc(sketch, "E1668", {"start": v(-72.77, -221.37) * mm, "mid": v(-72.75, -221.57) * mm, "end": v(-72.68, -221.76) * mm});
            skArc(sketch, "E1669", {"start": v(-72.68, -221.76) * mm, "mid": v(-72.47, -222.11) * mm, "end": v(-72.26, -222.46) * mm});
            skArc(sketch, "E1670", {"start": v(-72.26, -222.46) * mm, "mid": v(-71.99, -222.87) * mm, "end": v(-71.7, -223.26) * mm});
            skArc(sketch, "E1671", {"start": v(-71.7, -223.26) * mm, "mid": v(-71.37, -223.68) * mm, "end": v(-71.02, -224.08) * mm});
            skArc(sketch, "E1672", {"start": v(-71.02, -224.08) * mm, "mid": v(-70.45, -224.73) * mm, "end": v(-69.89, -225.4) * mm});
            skArc(sketch, "E1673", {"start": v(-69.89, -225.4) * mm, "mid": v(-69.8, -225.54) * mm, "end": v(-69.77, -225.7) * mm});
            skArc(sketch, "E1674", {"start": v(-69.77, -225.7) * mm, "mid": v(-69.82, -225.8) * mm, "end": v(-69.93, -225.81) * mm});
            skArc(sketch, "E1675", {"start": v(-69.93, -225.81) * mm, "mid": v(-70.48, -225.63) * mm, "end": v(-71.02, -225.44) * mm});
            skArc(sketch, "E1676", {"start": v(-71.02, -225.44) * mm, "mid": v(-71.36, -225.34) * mm, "end": v(-71.7, -225.26) * mm});
            skArc(sketch, "E1677", {"start": v(-71.7, -225.26) * mm, "mid": v(-71.98, -225.24) * mm, "end": v(-72.26, -225.27) * mm});
            skArc(sketch, "E1678", {"start": v(-72.26, -225.27) * mm, "mid": v(-72.46, -225.34) * mm, "end": v(-72.63, -225.45) * mm});
            skArc(sketch, "E1679", {"start": v(-72.63, -225.45) * mm, "mid": v(-72.74, -225.6) * mm, "end": v(-72.77, -225.77) * mm});
            skArc(sketch, "E1680", {"start": v(-72.77, -225.77) * mm, "mid": v(-72.66, -226.17) * mm, "end": v(-72.36, -226.46) * mm});
            skArc(sketch, "E1681", {"start": v(-72.36, -226.46) * mm, "mid": v(-71.85, -226.66) * mm, "end": v(-71.31, -226.71) * mm});
            skArc(sketch, "E1682", {"start": v(-71.31, -226.71) * mm, "mid": v(-70.68, -226.63) * mm, "end": v(-70.07, -226.41) * mm});
            skArc(sketch, "E1683", {"start": v(-70.07, -226.41) * mm, "mid": v(-69.6, -226.1) * mm, "end": v(-69.23, -225.66) * mm});
            skArc(sketch, "E1684", {"start": v(-69.23, -225.66) * mm, "mid": v(-69.12, -225.4) * mm, "end": v(-69.12, -225.1) * mm});
            skArc(sketch, "E1685", {"start": v(-69.12, -225.1) * mm, "mid": v(-69.22, -224.7) * mm, "end": v(-69.38, -224.32) * mm});
            skArc(sketch, "E1686", {"start": v(-69.38, -224.32) * mm, "mid": v(-69.62, -223.87) * mm, "end": v(-69.91, -223.45) * mm});
            skArc(sketch, "E1687", {"start": v(-69.91, -223.45) * mm, "mid": v(-70.27, -223.02) * mm, "end": v(-70.67, -222.62) * mm});
            skArc(sketch, "E1688", {"start": v(-70.67, -222.62) * mm, "mid": v(-71.07, -222.26) * mm, "end": v(-71.48, -221.92) * mm});
            skArc(sketch, "E1689", {"start": v(-71.48, -221.92) * mm, "mid": v(-71.8, -221.67) * mm, "end": v(-72.16, -221.44) * mm});
            skArc(sketch, "E1690", {"start": v(-72.16, -221.44) * mm, "mid": v(-72.38, -221.33) * mm, "end": v(-72.61, -221.25) * mm});
            skArc(sketch, "E1691", {"start": v(-72.61, -221.25) * mm, "mid": v(-72.72, -221.27) * mm, "end": v(-72.77, -221.37) * mm});
            skArc(sketch, "E1692", {"start": v(-63.15, -223.44) * mm, "mid": v(-62.92, -224.65) * mm, "end": v(-62.66, -225.86) * mm});
            skArc(sketch, "E1693", {"start": v(-62.66, -225.86) * mm, "mid": v(-62.5, -226.24) * mm, "end": v(-62.21, -226.54) * mm});
            skArc(sketch, "E1694", {"start": v(-62.21, -226.54) * mm, "mid": v(-61.98, -226.57) * mm, "end": v(-61.85, -226.38) * mm});
            skArc(sketch, "E1695", {"start": v(-61.85, -226.38) * mm, "mid": v(-61.8, -225.42) * mm, "end": v(-61.77, -224.46) * mm});
            skArc(sketch, "E1696", {"start": v(-61.77, -224.46) * mm, "mid": v(-61.8, -223.94) * mm, "end": v(-61.84, -223.42) * mm});
            skArc(sketch, "E1697", {"start": v(-61.84, -223.42) * mm, "mid": v(-61.93, -222.93) * mm, "end": v(-62.05, -222.45) * mm});
            skArc(sketch, "E1698", {"start": v(-62.05, -222.45) * mm, "mid": v(-62.18, -222.06) * mm, "end": v(-62.35, -221.68) * mm});
            skArc(sketch, "E1699", {"start": v(-62.35, -221.68) * mm, "mid": v(-62.5, -221.45) * mm, "end": v(-62.71, -221.28) * mm});
            skArc(sketch, "E1700", {"start": v(-62.71, -221.28) * mm, "mid": v(-62.87, -221.24) * mm, "end": v(-63.03, -221.3) * mm});
            skArc(sketch, "E1701", {"start": v(-63.03, -221.3) * mm, "mid": v(-63.16, -221.45) * mm, "end": v(-63.24, -221.65) * mm});
            skArc(sketch, "E1702", {"start": v(-63.24, -221.65) * mm, "mid": v(-63.29, -222.02) * mm, "end": v(-63.29, -222.4) * mm});
            skArc(sketch, "E1703", {"start": v(-63.29, -222.4) * mm, "mid": v(-63.23, -222.92) * mm, "end": v(-63.15, -223.44) * mm});
            skArc(sketch, "E1704", {"start": v(-60.61, -223.24) * mm, "mid": v(-60.5, -223.97) * mm, "end": v(-60.33, -224.68) * mm});
            skArc(sketch, "E1705", {"start": v(-60.33, -224.68) * mm, "mid": v(-60.14, -225.19) * mm, "end": v(-59.85, -225.64) * mm});
            skArc(sketch, "E1706", {"start": v(-59.85, -225.64) * mm, "mid": v(-59.51, -225.98) * mm, "end": v(-59.1, -226.24) * mm});
            skArc(sketch, "E1707", {"start": v(-59.1, -226.24) * mm, "mid": v(-58.57, -226.44) * mm, "end": v(-58.02, -226.56) * mm});
            skArc(sketch, "E1708", {"start": v(-58.02, -226.56) * mm, "mid": v(-57.41, -226.61) * mm, "end": v(-56.8, -226.6) * mm});
            skArc(sketch, "E1709", {"start": v(-56.8, -226.6) * mm, "mid": v(-56.46, -226.5) * mm, "end": v(-56.19, -226.25) * mm});
            skArc(sketch, "E1710", {"start": v(-56.19, -226.25) * mm, "mid": v(-55.99, -225.86) * mm, "end": v(-55.91, -225.43) * mm});
            skArc(sketch, "E1711", {"start": v(-55.91, -225.43) * mm, "mid": v(-55.9, -224.5) * mm, "end": v(-55.92, -223.56) * mm});
            skArc(sketch, "E1712", {"start": v(-55.92, -223.56) * mm, "mid": v(-55.98, -222.44) * mm, "end": v(-56.03, -221.33) * mm});
            skArc(sketch, "E1713", {"start": v(-56.03, -221.33) * mm, "mid": v(-56.05, -221.23) * mm, "end": v(-56.11, -221.15) * mm});
            skArc(sketch, "E1714", {"start": v(-56.11, -221.15) * mm, "mid": v(-56.17, -221.14) * mm, "end": v(-56.21, -221.18) * mm});
            skArc(sketch, "E1715", {"start": v(-56.21, -221.18) * mm, "mid": v(-56.35, -222.11) * mm, "end": v(-56.5, -223.05) * mm});
            skArc(sketch, "E1716", {"start": v(-56.5, -223.05) * mm, "mid": v(-56.7, -223.9) * mm, "end": v(-57.05, -224.72) * mm});
            skArc(sketch, "E1717", {"start": v(-57.05, -224.72) * mm, "mid": v(-57.47, -225.19) * mm, "end": v(-58.05, -225.42) * mm});
            skArc(sketch, "E1718", {"start": v(-58.05, -225.42) * mm, "mid": v(-58.57, -225.33) * mm, "end": v(-58.93, -224.96) * mm});
            skArc(sketch, "E1719", {"start": v(-58.93, -224.96) * mm, "mid": v(-59.2, -224.23) * mm, "end": v(-59.29, -223.47) * mm});
            skArc(sketch, "E1720", {"start": v(-59.29, -223.47) * mm, "mid": v(-59.3, -223.14) * mm, "end": v(-59.35, -222.8) * mm});
            skArc(sketch, "E1721", {"start": v(-59.35, -222.8) * mm, "mid": v(-59.43, -222.45) * mm, "end": v(-59.54, -222.1) * mm});
            skArc(sketch, "E1722", {"start": v(-59.54, -222.1) * mm, "mid": v(-59.66, -221.8) * mm, "end": v(-59.8, -221.49) * mm});
            skArc(sketch, "E1723", {"start": v(-59.8, -221.49) * mm, "mid": v(-59.95, -221.26) * mm, "end": v(-60.13, -221.06) * mm});
            skArc(sketch, "E1724", {"start": v(-60.13, -221.06) * mm, "mid": v(-60.26, -221) * mm, "end": v(-60.4, -221.04) * mm});
            skArc(sketch, "E1725", {"start": v(-60.4, -221.04) * mm, "mid": v(-60.53, -221.18) * mm, "end": v(-60.6, -221.36) * mm});
            skArc(sketch, "E1726", {"start": v(-60.6, -221.36) * mm, "mid": v(-60.67, -221.75) * mm, "end": v(-60.69, -222.14) * mm});
            skArc(sketch, "E1727", {"start": v(-60.69, -222.14) * mm, "mid": v(-60.66, -222.69) * mm, "end": v(-60.61, -223.24) * mm});
            skArc(sketch, "E1728", {"start": v(-44.41, -222.24) * mm, "mid": v(-44.65, -223.32) * mm, "end": v(-44.57, -224.43) * mm});
            skArc(sketch, "E1729", {"start": v(-44.57, -224.43) * mm, "mid": v(-44.16, -225.44) * mm, "end": v(-43.46, -226.26) * mm});
            skArc(sketch, "E1730", {"start": v(-43.46, -226.26) * mm, "mid": v(-42.66, -226.68) * mm, "end": v(-41.76, -226.74) * mm});
            skArc(sketch, "E1731", {"start": v(-41.76, -226.74) * mm, "mid": v(-40.91, -226.4) * mm, "end": v(-40.28, -225.75) * mm});
            skArc(sketch, "E1732", {"start": v(-40.28, -225.75) * mm, "mid": v(-40.2, -225.59) * mm, "end": v(-40.16, -225.41) * mm});
            skArc(sketch, "E1733", {"start": v(-40.16, -225.41) * mm, "mid": v(-40.18, -225.3) * mm, "end": v(-40.27, -225.2) * mm});
            skArc(sketch, "E1734", {"start": v(-40.27, -225.2) * mm, "mid": v(-40.43, -225.16) * mm, "end": v(-40.6, -225.16) * mm});
            skArc(sketch, "E1735", {"start": v(-40.6, -225.16) * mm, "mid": v(-40.86, -225.23) * mm, "end": v(-41.12, -225.32) * mm});
            skArc(sketch, "E1736", {"start": v(-41.12, -225.32) * mm, "mid": v(-41.42, -225.4) * mm, "end": v(-41.73, -225.45) * mm});
            skArc(sketch, "E1737", {"start": v(-41.73, -225.45) * mm, "mid": v(-42.03, -225.45) * mm, "end": v(-42.34, -225.4) * mm});
            skArc(sketch, "E1738", {"start": v(-42.34, -225.4) * mm, "mid": v(-42.61, -225.3) * mm, "end": v(-42.87, -225.17) * mm});
            skArc(sketch, "E1739", {"start": v(-42.87, -225.17) * mm, "mid": v(-43.07, -225) * mm, "end": v(-43.23, -224.8) * mm});
            skArc(sketch, "E1740", {"start": v(-43.23, -224.8) * mm, "mid": v(-43.31, -224.6) * mm, "end": v(-43.33, -224.39) * mm});
            skArc(sketch, "E1741", {"start": v(-43.33, -224.39) * mm, "mid": v(-43.26, -224.2) * mm, "end": v(-43.13, -224.04) * mm});
            skArc(sketch, "E1742", {"start": v(-43.13, -224.04) * mm, "mid": v(-42.89, -223.9) * mm, "end": v(-42.62, -223.8) * mm});
            skArc(sketch, "E1743", {"start": v(-42.62, -223.8) * mm, "mid": v(-42.23, -223.76) * mm, "end": v(-41.83, -223.74) * mm});
            skArc(sketch, "E1744", {"start": v(-41.83, -223.74) * mm, "mid": v(-41.43, -223.71) * mm, "end": v(-41.03, -223.63) * mm});
            skArc(sketch, "E1745", {"start": v(-41.03, -223.63) * mm, "mid": v(-40.69, -223.5) * mm, "end": v(-40.37, -223.3) * mm});
            skArc(sketch, "E1746", {"start": v(-40.37, -223.3) * mm, "mid": v(-40.12, -223.09) * mm, "end": v(-39.93, -222.82) * mm});
            skArc(sketch, "E1747", {"start": v(-39.93, -222.82) * mm, "mid": v(-39.81, -222.54) * mm, "end": v(-39.77, -222.24) * mm});
            skArc(sketch, "E1748", {"start": v(-39.77, -222.24) * mm, "mid": v(-39.8, -221.95) * mm, "end": v(-39.85, -221.66) * mm});
            skArc(sketch, "E1749", {"start": v(-39.85, -221.66) * mm, "mid": v(-39.95, -221.41) * mm, "end": v(-40.09, -221.18) * mm});
            skArc(sketch, "E1750", {"start": v(-40.09, -221.18) * mm, "mid": v(-40.24, -221) * mm, "end": v(-40.43, -220.85) * mm});
            skArc(sketch, "E1751", {"start": v(-40.43, -220.85) * mm, "mid": v(-40.62, -220.77) * mm, "end": v(-40.83, -220.74) * mm});
            skArc(sketch, "E1752", {"start": v(-40.83, -220.74) * mm, "mid": v(-41.02, -220.76) * mm, "end": v(-41.19, -220.82) * mm});
            skArc(sketch, "E1753", {"start": v(-41.19, -220.82) * mm, "mid": v(-41.31, -220.9) * mm, "end": v(-41.4, -221.03) * mm});
            skArc(sketch, "E1754", {"start": v(-41.4, -221.03) * mm, "mid": v(-41.44, -221.2) * mm, "end": v(-41.43, -221.36) * mm});
            skArc(sketch, "E1755", {"start": v(-41.43, -221.36) * mm, "mid": v(-41.37, -221.55) * mm, "end": v(-41.27, -221.74) * mm});
            skArc(sketch, "E1756", {"start": v(-41.27, -221.74) * mm, "mid": v(-41.2, -221.92) * mm, "end": v(-41.17, -222.12) * mm});
            skArc(sketch, "E1757", {"start": v(-41.17, -222.12) * mm, "mid": v(-41.21, -222.3) * mm, "end": v(-41.31, -222.44) * mm});
            skArc(sketch, "E1758", {"start": v(-41.31, -222.44) * mm, "mid": v(-41.5, -222.58) * mm, "end": v(-41.7, -222.66) * mm});
            skArc(sketch, "E1759", {"start": v(-41.7, -222.66) * mm, "mid": v(-41.98, -222.72) * mm, "end": v(-42.27, -222.74) * mm});
            skArc(sketch, "E1760", {"start": v(-42.27, -222.74) * mm, "mid": v(-42.56, -222.72) * mm, "end": v(-42.85, -222.66) * mm});
            skArc(sketch, "E1761", {"start": v(-42.85, -222.66) * mm, "mid": v(-43.06, -222.58) * mm, "end": v(-43.24, -222.44) * mm});
            skArc(sketch, "E1762", {"start": v(-43.24, -222.44) * mm, "mid": v(-43.34, -222.3) * mm, "end": v(-43.38, -222.12) * mm});
            skArc(sketch, "E1763", {"start": v(-43.38, -222.12) * mm, "mid": v(-43.35, -221.92) * mm, "end": v(-43.27, -221.74) * mm});
            skArc(sketch, "E1764", {"start": v(-43.27, -221.74) * mm, "mid": v(-43.17, -221.55) * mm, "end": v(-43.08, -221.35) * mm});
            skArc(sketch, "E1765", {"start": v(-43.08, -221.35) * mm, "mid": v(-43.03, -221.2) * mm, "end": v(-43.01, -221.03) * mm});
            skArc(sketch, "E1766", {"start": v(-43.01, -221.03) * mm, "mid": v(-43.03, -220.92) * mm, "end": v(-43.08, -220.82) * mm});
            skArc(sketch, "E1767", {"start": v(-43.08, -220.82) * mm, "mid": v(-43.15, -220.76) * mm, "end": v(-43.25, -220.74) * mm});
            skArc(sketch, "E1768", {"start": v(-43.25, -220.74) * mm, "mid": v(-43.39, -220.76) * mm, "end": v(-43.51, -220.84) * mm});
            skArc(sketch, "E1769", {"start": v(-43.51, -220.84) * mm, "mid": v(-43.68, -221) * mm, "end": v(-43.83, -221.18) * mm});
            skArc(sketch, "E1770", {"start": v(-43.83, -221.18) * mm, "mid": v(-44, -221.41) * mm, "end": v(-44.15, -221.66) * mm});
            skArc(sketch, "E1771", {"start": v(-44.15, -221.66) * mm, "mid": v(-44.29, -221.95) * mm, "end": v(-44.41, -222.24) * mm});
            skArc(sketch, "E1772", {"start": v(-37.64, -223.99) * mm, "mid": v(-37.6, -224.95) * mm, "end": v(-37.55, -225.9) * mm});
            skArc(sketch, "E1773", {"start": v(-37.55, -225.9) * mm, "mid": v(-37.52, -226.05) * mm, "end": v(-37.44, -226.19) * mm});
            skArc(sketch, "E1774", {"start": v(-37.44, -226.19) * mm, "mid": v(-37.37, -226.21) * mm, "end": v(-37.31, -226.16) * mm});
            skArc(sketch, "E1775", {"start": v(-37.31, -226.16) * mm, "mid": v(-37.17, -225.45) * mm, "end": v(-37.04, -224.74) * mm});
            skArc(sketch, "E1776", {"start": v(-37.04, -224.74) * mm, "mid": v(-36.92, -224.23) * mm, "end": v(-36.77, -223.73) * mm});
            skArc(sketch, "E1777", {"start": v(-36.77, -223.73) * mm, "mid": v(-36.59, -223.23) * mm, "end": v(-36.37, -222.76) * mm});
            skArc(sketch, "E1778", {"start": v(-36.37, -222.76) * mm, "mid": v(-36.15, -222.35) * mm, "end": v(-35.9, -221.96) * mm});
            skArc(sketch, "E1779", {"start": v(-35.9, -221.96) * mm, "mid": v(-35.68, -221.7) * mm, "end": v(-35.42, -221.5) * mm});
            skArc(sketch, "E1780", {"start": v(-35.42, -221.5) * mm, "mid": v(-35.22, -221.36) * mm, "end": v(-35.04, -221.19) * mm});
            skArc(sketch, "E1781", {"start": v(-35.04, -221.19) * mm, "mid": v(-34.99, -221.07) * mm, "end": v(-35.03, -220.95) * mm});
            skArc(sketch, "E1782", {"start": v(-35.03, -220.95) * mm, "mid": v(-35.15, -220.85) * mm, "end": v(-35.31, -220.8) * mm});
            skArc(sketch, "E1783", {"start": v(-35.31, -220.8) * mm, "mid": v(-35.67, -220.77) * mm, "end": v(-36.02, -220.75) * mm});
            skArc(sketch, "E1784", {"start": v(-36.02, -220.75) * mm, "mid": v(-36.45, -220.8) * mm, "end": v(-36.85, -220.93) * mm});
            skArc(sketch, "E1785", {"start": v(-36.85, -220.93) * mm, "mid": v(-37.16, -221.14) * mm, "end": v(-37.37, -221.43) * mm});
            skArc(sketch, "E1786", {"start": v(-37.37, -221.43) * mm, "mid": v(-37.55, -221.9) * mm, "end": v(-37.62, -222.38) * mm});
            skArc(sketch, "E1787", {"start": v(-37.62, -222.38) * mm, "mid": v(-37.65, -223.18) * mm, "end": v(-37.64, -223.99) * mm});
            skArc(sketch, "E1788", {"start": v(-33.77, -221.78) * mm, "mid": v(-33.75, -222) * mm, "end": v(-33.66, -222.21) * mm});
            skArc(sketch, "E1789", {"start": v(-33.66, -222.21) * mm, "mid": v(-33.51, -222.45) * mm, "end": v(-33.33, -222.67) * mm});
            skArc(sketch, "E1790", {"start": v(-33.33, -222.67) * mm, "mid": v(-33.1, -222.89) * mm, "end": v(-32.85, -223.08) * mm});
            skArc(sketch, "E1791", {"start": v(-32.85, -223.08) * mm, "mid": v(-32.57, -223.24) * mm, "end": v(-32.27, -223.38) * mm});
            skArc(sketch, "E1792", {"start": v(-32.27, -223.38) * mm, "mid": v(-31.98, -223.5) * mm, "end": v(-31.7, -223.67) * mm});
            skArc(sketch, "E1793", {"start": v(-31.7, -223.67) * mm, "mid": v(-31.45, -223.86) * mm, "end": v(-31.21, -224.08) * mm});
            skArc(sketch, "E1794", {"start": v(-31.21, -224.08) * mm, "mid": v(-31.04, -224.3) * mm, "end": v(-30.88, -224.53) * mm});
            skArc(sketch, "E1795", {"start": v(-30.88, -224.53) * mm, "mid": v(-30.8, -224.73) * mm, "end": v(-30.77, -224.95) * mm});
            skArc(sketch, "E1796", {"start": v(-30.77, -224.95) * mm, "mid": v(-30.8, -225.13) * mm, "end": v(-30.9, -225.28) * mm});
            skArc(sketch, "E1797", {"start": v(-30.9, -225.28) * mm, "mid": v(-31.05, -225.4) * mm, "end": v(-31.23, -225.48) * mm});
            skArc(sketch, "E1798", {"start": v(-31.23, -225.48) * mm, "mid": v(-31.48, -225.52) * mm, "end": v(-31.73, -225.51) * mm});
            skArc(sketch, "E1799", {"start": v(-31.73, -225.51) * mm, "mid": v(-32.03, -225.45) * mm, "end": v(-32.33, -225.36) * mm});
            skArc(sketch, "E1800", {"start": v(-32.33, -225.36) * mm, "mid": v(-32.61, -225.26) * mm, "end": v(-32.9, -225.18) * mm});
            skArc(sketch, "E1801", {"start": v(-32.9, -225.18) * mm, "mid": v(-33.09, -225.17) * mm, "end": v(-33.26, -225.21) * mm});
            skArc(sketch, "E1802", {"start": v(-33.26, -225.21) * mm, "mid": v(-33.35, -225.3) * mm, "end": v(-33.38, -225.41) * mm});
            skArc(sketch, "E1803", {"start": v(-33.38, -225.41) * mm, "mid": v(-33.34, -225.59) * mm, "end": v(-33.27, -225.75) * mm});
            skArc(sketch, "E1804", {"start": v(-33.27, -225.75) * mm, "mid": v(-32.9, -226.2) * mm, "end": v(-32.4, -226.5) * mm});
            skArc(sketch, "E1805", {"start": v(-32.4, -226.5) * mm, "mid": v(-31.8, -226.68) * mm, "end": v(-31.19, -226.7) * mm});
            skArc(sketch, "E1806", {"start": v(-31.19, -226.7) * mm, "mid": v(-30.65, -226.58) * mm, "end": v(-30.18, -226.3) * mm});
            skArc(sketch, "E1807", {"start": v(-30.18, -226.3) * mm, "mid": v(-29.88, -225.93) * mm, "end": v(-29.77, -225.46) * mm});
            skArc(sketch, "E1808", {"start": v(-29.77, -225.46) * mm, "mid": v(-29.8, -225.15) * mm, "end": v(-29.91, -224.85) * mm});
            skArc(sketch, "E1809", {"start": v(-29.91, -224.85) * mm, "mid": v(-30.12, -224.44) * mm, "end": v(-30.36, -224.05) * mm});
            skArc(sketch, "E1810", {"start": v(-30.36, -224.05) * mm, "mid": v(-30.67, -223.63) * mm, "end": v(-31, -223.22) * mm});
            skArc(sketch, "E1811", {"start": v(-31, -223.22) * mm, "mid": v(-31.38, -222.83) * mm, "end": v(-31.77, -222.47) * mm});
            skArc(sketch, "E1812", {"start": v(-31.77, -222.47) * mm, "mid": v(-32.15, -222.17) * mm, "end": v(-32.54, -221.88) * mm});
            skArc(sketch, "E1813", {"start": v(-32.54, -221.88) * mm, "mid": v(-32.85, -221.7) * mm, "end": v(-33.19, -221.56) * mm});
            skArc(sketch, "E1814", {"start": v(-33.19, -221.56) * mm, "mid": v(-33.4, -221.52) * mm, "end": v(-33.6, -221.55) * mm});
            skArc(sketch, "E1815", {"start": v(-33.6, -221.55) * mm, "mid": v(-33.72, -221.63) * mm, "end": v(-33.77, -221.78) * mm});
            skArc(sketch, "E1816", {"start": v(4.59, -222.24) * mm, "mid": v(4.37, -223.04) * mm, "end": v(4.3, -223.88) * mm});
            skArc(sketch, "E1817", {"start": v(4.3, -223.88) * mm, "mid": v(4.41, -224.64) * mm, "end": v(4.7, -225.35) * mm});
            skArc(sketch, "E1818", {"start": v(4.7, -225.35) * mm, "mid": v(5.14, -225.93) * mm, "end": v(5.72, -226.37) * mm});
            skArc(sketch, "E1819", {"start": v(5.72, -226.37) * mm, "mid": v(6.4, -226.64) * mm, "end": v(7.13, -226.74) * mm});
            skArc(sketch, "E1820", {"start": v(7.13, -226.74) * mm, "mid": v(7.9, -226.6) * mm, "end": v(8.57, -226.2) * mm});
            skArc(sketch, "E1821", {"start": v(8.57, -226.2) * mm, "mid": v(9.2, -225.53) * mm, "end": v(9.68, -224.73) * mm});
            skArc(sketch, "E1822", {"start": v(9.68, -224.73) * mm, "mid": v(9.97, -223.87) * mm, "end": v(10.06, -222.96) * mm});
            skArc(sketch, "E1823", {"start": v(10.06, -222.96) * mm, "mid": v(9.9, -222.23) * mm, "end": v(9.5, -221.6) * mm});
            skArc(sketch, "E1824", {"start": v(9.5, -221.6) * mm, "mid": v(9.32, -221.48) * mm, "end": v(9.12, -221.4) * mm});
            skArc(sketch, "E1825", {"start": v(9.12, -221.4) * mm, "mid": v(8.96, -221.43) * mm, "end": v(8.83, -221.53) * mm});
            skArc(sketch, "E1826", {"start": v(8.83, -221.53) * mm, "mid": v(8.72, -221.78) * mm, "end": v(8.66, -222.05) * mm});
            skArc(sketch, "E1827", {"start": v(8.66, -222.05) * mm, "mid": v(8.64, -222.5) * mm, "end": v(8.64, -222.95) * mm});
            skArc(sketch, "E1828", {"start": v(8.64, -222.95) * mm, "mid": v(8.63, -223.43) * mm, "end": v(8.58, -223.9) * mm});
            skArc(sketch, "E1829", {"start": v(8.58, -223.9) * mm, "mid": v(8.47, -224.27) * mm, "end": v(8.3, -224.62) * mm});
            skArc(sketch, "E1830", {"start": v(8.3, -224.62) * mm, "mid": v(8.1, -224.88) * mm, "end": v(7.83, -225.07) * mm});
            skArc(sketch, "E1831", {"start": v(7.83, -225.07) * mm, "mid": v(7.54, -225.2) * mm, "end": v(7.23, -225.24) * mm});
            skArc(sketch, "E1832", {"start": v(7.23, -225.24) * mm, "mid": v(6.9, -225.2) * mm, "end": v(6.61, -225.08) * mm});
            skArc(sketch, "E1833", {"start": v(6.61, -225.08) * mm, "mid": v(6.36, -224.9) * mm, "end": v(6.18, -224.65) * mm});
            skArc(sketch, "E1834", {"start": v(6.18, -224.65) * mm, "mid": v(6.03, -224.31) * mm, "end": v(5.96, -223.95) * mm});
            skArc(sketch, "E1835", {"start": v(5.96, -223.95) * mm, "mid": v(5.94, -223.47) * mm, "end": v(5.96, -222.99) * mm});
            skArc(sketch, "E1836", {"start": v(5.96, -222.99) * mm, "mid": v(6.03, -222.19) * mm, "end": v(6.04, -221.38) * mm});
            skArc(sketch, "E1837", {"start": v(6.04, -221.38) * mm, "mid": v(5.95, -221.05) * mm, "end": v(5.7, -220.81) * mm});
            skArc(sketch, "E1838", {"start": v(5.7, -220.81) * mm, "mid": v(5.42, -220.78) * mm, "end": v(5.2, -220.96) * mm});
            skArc(sketch, "E1839", {"start": v(5.2, -220.96) * mm, "mid": v(4.87, -221.58) * mm, "end": v(4.59, -222.24) * mm});
            skArc(sketch, "E1840", {"start": v(11.23, -223.74) * mm, "mid": v(11.23, -224.31) * mm, "end": v(11.25, -224.89) * mm});
            skArc(sketch, "E1841", {"start": v(11.25, -224.89) * mm, "mid": v(11.29, -225.37) * mm, "end": v(11.34, -225.86) * mm});
            skArc(sketch, "E1842", {"start": v(11.34, -225.86) * mm, "mid": v(11.4, -226.23) * mm, "end": v(11.46, -226.61) * mm});
            skArc(sketch, "E1843", {"start": v(11.46, -226.61) * mm, "mid": v(11.51, -226.7) * mm, "end": v(11.61, -226.74) * mm});
            skArc(sketch, "E1844", {"start": v(11.61, -226.74) * mm, "mid": v(11.72, -226.7) * mm, "end": v(11.78, -226.61) * mm});
            skArc(sketch, "E1845", {"start": v(11.78, -226.61) * mm, "mid": v(11.9, -226.24) * mm, "end": v(12.01, -225.86) * mm});
            skArc(sketch, "E1846", {"start": v(12.01, -225.86) * mm, "mid": v(12.14, -225.37) * mm, "end": v(12.24, -224.89) * mm});
            skArc(sketch, "E1847", {"start": v(12.24, -224.89) * mm, "mid": v(12.35, -224.31) * mm, "end": v(12.44, -223.74) * mm});
            skArc(sketch, "E1848", {"start": v(12.44, -223.74) * mm, "mid": v(12.5, -223.16) * mm, "end": v(12.55, -222.59) * mm});
            skArc(sketch, "E1849", {"start": v(12.55, -222.59) * mm, "mid": v(12.55, -222.1) * mm, "end": v(12.5, -221.62) * mm});
            skArc(sketch, "E1850", {"start": v(12.5, -221.62) * mm, "mid": v(12.44, -221.27) * mm, "end": v(12.34, -220.94) * mm});
            skArc(sketch, "E1851", {"start": v(12.34, -220.94) * mm, "mid": v(12.23, -220.8) * mm, "end": v(12.05, -220.74) * mm});
            skArc(sketch, "E1852", {"start": v(12.05, -220.74) * mm, "mid": v(11.87, -220.8) * mm, "end": v(11.73, -220.93) * mm});
            skArc(sketch, "E1853", {"start": v(11.73, -220.93) * mm, "mid": v(11.58, -221.27) * mm, "end": v(11.47, -221.62) * mm});
            skArc(sketch, "E1854", {"start": v(11.47, -221.62) * mm, "mid": v(11.36, -222.1) * mm, "end": v(11.29, -222.59) * mm});
            skArc(sketch, "E1855", {"start": v(11.29, -222.59) * mm, "mid": v(11.24, -223.16) * mm, "end": v(11.23, -223.74) * mm});
            skArc(sketch, "E1856", {"start": v(19.01, -223.74) * mm, "mid": v(19.21, -225.02) * mm, "end": v(19.43, -226.3) * mm});
            skArc(sketch, "E1857", {"start": v(19.43, -226.3) * mm, "mid": v(19.57, -226.54) * mm, "end": v(19.83, -226.63) * mm});
            skArc(sketch, "E1858", {"start": v(19.83, -226.63) * mm, "mid": v(20.07, -226.53) * mm, "end": v(20.18, -226.3) * mm});
            skArc(sketch, "E1859", {"start": v(20.18, -226.3) * mm, "mid": v(20.21, -225.02) * mm, "end": v(20.23, -223.74) * mm});
            skArc(sketch, "E1860", {"start": v(20.23, -223.74) * mm, "mid": v(20.21, -223.16) * mm, "end": v(20.17, -222.59) * mm});
            skArc(sketch, "E1861", {"start": v(20.17, -222.59) * mm, "mid": v(20.1, -222.1) * mm, "end": v(19.98, -221.62) * mm});
            skArc(sketch, "E1862", {"start": v(19.98, -221.62) * mm, "mid": v(19.87, -221.27) * mm, "end": v(19.72, -220.93) * mm});
            skArc(sketch, "E1863", {"start": v(19.72, -220.93) * mm, "mid": v(19.59, -220.8) * mm, "end": v(19.4, -220.74) * mm});
            skArc(sketch, "E1864", {"start": v(19.4, -220.74) * mm, "mid": v(19.22, -220.8) * mm, "end": v(19.11, -220.94) * mm});
            skArc(sketch, "E1865", {"start": v(19.11, -220.94) * mm, "mid": v(19, -221.27) * mm, "end": v(18.94, -221.62) * mm});
            skArc(sketch, "E1866", {"start": v(18.94, -221.62) * mm, "mid": v(18.9, -222.1) * mm, "end": v(18.9, -222.59) * mm});
            skArc(sketch, "E1867", {"start": v(18.9, -222.59) * mm, "mid": v(18.94, -223.16) * mm, "end": v(19.01, -223.74) * mm});
            skArc(sketch, "E1868", {"start": v(-88.77, -225.24) * mm, "mid": v(-88.76, -225.53) * mm, "end": v(-88.7, -225.81) * mm});
            skArc(sketch, "E1869", {"start": v(-88.7, -225.81) * mm, "mid": v(-88.61, -226.06) * mm, "end": v(-88.48, -226.3) * mm});
            skArc(sketch, "E1870", {"start": v(-88.48, -226.3) * mm, "mid": v(-88.33, -226.48) * mm, "end": v(-88.16, -226.62) * mm});
            skArc(sketch, "E1871", {"start": v(-88.16, -226.62) * mm, "mid": v(-87.97, -226.7) * mm, "end": v(-87.77, -226.74) * mm});
            skArc(sketch, "E1872", {"start": v(-87.77, -226.74) * mm, "mid": v(-87.58, -226.7) * mm, "end": v(-87.4, -226.62) * mm});
            skArc(sketch, "E1873", {"start": v(-87.4, -226.62) * mm, "mid": v(-87.21, -226.48) * mm, "end": v(-87.07, -226.3) * mm});
            skArc(sketch, "E1874", {"start": v(-87.07, -226.3) * mm, "mid": v(-86.94, -226.06) * mm, "end": v(-86.85, -225.81) * mm});
            skArc(sketch, "E1875", {"start": v(-86.85, -225.81) * mm, "mid": v(-86.8, -225.53) * mm, "end": v(-86.77, -225.24) * mm});
            skArc(sketch, "E1876", {"start": v(-86.77, -225.24) * mm, "mid": v(-86.8, -224.95) * mm, "end": v(-86.85, -224.66) * mm});
            skArc(sketch, "E1877", {"start": v(-86.85, -224.66) * mm, "mid": v(-86.94, -224.41) * mm, "end": v(-87.07, -224.18) * mm});
            skArc(sketch, "E1878", {"start": v(-87.07, -224.18) * mm, "mid": v(-87.21, -224) * mm, "end": v(-87.4, -223.85) * mm});
            skArc(sketch, "E1879", {"start": v(-87.4, -223.85) * mm, "mid": v(-87.58, -223.77) * mm, "end": v(-87.77, -223.74) * mm});
            skArc(sketch, "E1880", {"start": v(-87.77, -223.74) * mm, "mid": v(-87.97, -223.77) * mm, "end": v(-88.16, -223.85) * mm});
            skArc(sketch, "E1881", {"start": v(-88.16, -223.85) * mm, "mid": v(-88.33, -224) * mm, "end": v(-88.48, -224.18) * mm});
            skArc(sketch, "E1882", {"start": v(-88.48, -224.18) * mm, "mid": v(-88.61, -224.41) * mm, "end": v(-88.7, -224.66) * mm});
            skArc(sketch, "E1883", {"start": v(-88.7, -224.66) * mm, "mid": v(-88.76, -224.95) * mm, "end": v(-88.77, -225.24) * mm});
            skSolve(sketch);
        }
        {
            var Q0;
            Q0=makeQuery(id+"F0.imprint","IMPRINT",FACE,{"disambiguationData":[TD([[makeQuery(id+"F0.imprint","IMPRINT",EDGE,{"derivedFrom":sQuery(id+"F0.wireOp",EDGE,"E0")}),1.0]])]});
            var Q1;
            Q1=makeQuery(id+"F0.imprint","IMPRINT",FACE,{"disambiguationData":[TD([[makeQuery(id+"F0.imprint","IMPRINT",EDGE,{"derivedFrom":sQuery(id+"F0.wireOp",EDGE,"E358")}),1.0]])]});
            var Q2;
            Q2=makeQuery(id+"F0.imprint","IMPRINT",FACE,{"disambiguationData":[TD([[makeQuery(id+"F0.imprint","IMPRINT",EDGE,{"derivedFrom":sQuery(id+"F0.wireOp",EDGE,"E822")}),1.0]])]});
            var Q3;
            Q3=makeQuery(id+"F0.imprint","IMPRINT",FACE,{"disambiguationData":[TD([[makeQuery(id+"F0.imprint","IMPRINT",EDGE,{"derivedFrom":sQuery(id+"F0.wireOp",EDGE,"E940")}),1.0]])]});
            var Q4;
            Q4=makeQuery(id+"F0.imprint","IMPRINT",FACE,{"disambiguationData":[TD([[makeQuery(id+"F0.imprint","IMPRINT",EDGE,{"derivedFrom":sQuery(id+"F0.wireOp",EDGE,"E990")}),1.0]])]});
            var Q5;
            Q5=makeQuery(id+"F0.imprint","IMPRINT",FACE,{"disambiguationData":[TD([[makeQuery(id+"F0.imprint","IMPRINT",EDGE,{"derivedFrom":sQuery(id+"F0.wireOp",EDGE,"E1056")}),1.0]])]});
            extrude(context, id + "F1", {"entities" : qUnion([Q0, Q1, Q2, Q3, Q4, Q5]), "depth" : 25 * mm, "offsetDistance" : 25 * mm});
        }
    });
